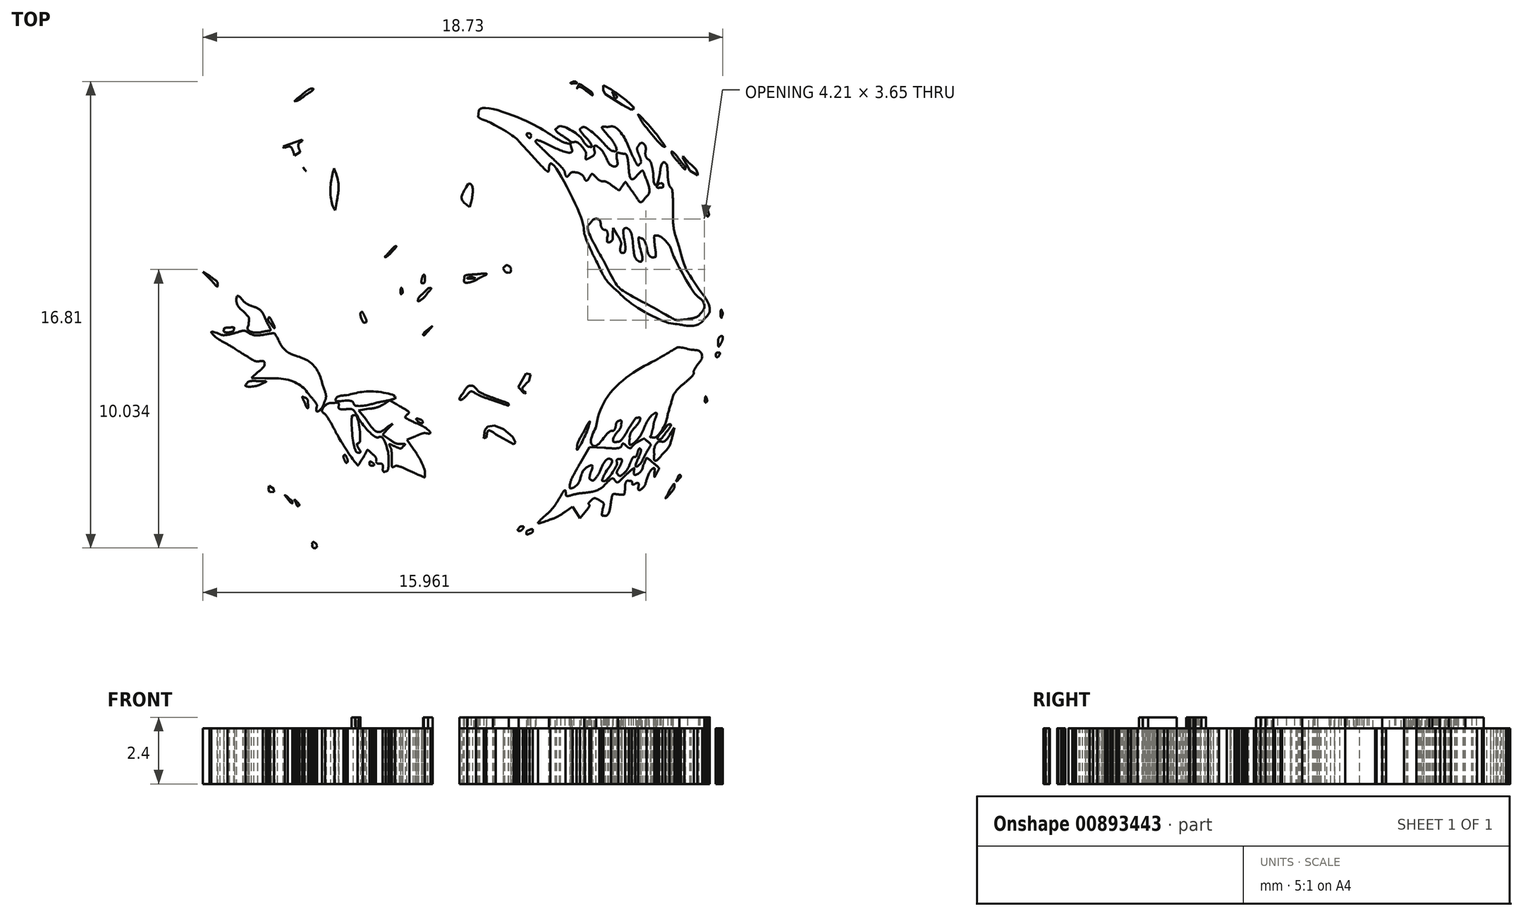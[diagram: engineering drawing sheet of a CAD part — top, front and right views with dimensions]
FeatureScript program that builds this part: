
annotation { "Feature Type Name" : "Feature", "Feature Type Description" : "" }
export const myFeature = defineFeature(function(context is Context, id is Id, definition is map)
    precondition{}
    {
        {
            var Q0;
            Q0=qCreatedBy(makeId("Top.planeOp"),FACE);
            var sketch = newSketch(context, id + "F0", { "sketchPlane" : qUnion([Q0])});
            skLineSegment(sketch, "E0", {"start": v(-1.28, 3.28) * mm, "end": v(-1.3, 2.97) * mm});
            skLineSegment(sketch, "E1", {"start": v(-1.3, 2.97) * mm, "end": v(-1.11, 3.15) * mm});
            skLineSegment(sketch, "E2", {"start": v(2.18, 4.65) * mm, "end": v(2.37, 4.86) * mm});
            skLineSegment(sketch, "E3", {"start": v(2.37, 4.86) * mm, "end": v(2.16, 5.12) * mm});
            skLineSegment(sketch, "E4", {"start": v(-1.79, -9.77) * mm, "end": v(-1.79, -9.77) * mm});
            skLineSegment(sketch, "E5", {"start": v(1.22, -9.04) * mm, "end": v(1.22, -9.04) * mm});
            skLineSegment(sketch, "E6", {"start": v(3.68, -7.03) * mm, "end": v(3.93, -6.85) * mm});
            skLineSegment(sketch, "E7", {"start": v(3.93, -6.85) * mm, "end": v(4.07, -7.06) * mm});
            skLineSegment(sketch, "E8", {"start": v(4.07, -7.06) * mm, "end": v(4.2, -7.27) * mm});
            skLineSegment(sketch, "E9", {"start": v(4.2, -7.27) * mm, "end": v(4.38, -7.05) * mm});
            skLineSegment(sketch, "E10", {"start": v(3.14, -7.31) * mm, "end": v(3.14, -7.31) * mm});
            skLineSegment(sketch, "E11", {"start": v(5.08, -4.73) * mm, "end": v(4.54, -4.7) * mm});
            skLineSegment(sketch, "E12", {"start": v(4.54, -4.7) * mm, "end": v(4.2, -5.3) * mm});
            skLineSegment(sketch, "E13", {"start": v(4.23, -5.78) * mm, "end": v(4.23, -5.78) * mm});
            skLineSegment(sketch, "E14", {"start": v(7.55, -4.24) * mm, "end": v(7.6, -4) * mm});
            skLineSegment(sketch, "E15", {"start": v(7.6, -4) * mm, "end": v(7.44, -4.26) * mm});
            skLineSegment(sketch, "E16", {"start": v(5.1, -4.32) * mm, "end": v(5.1, -4.32) * mm});
            skLineSegment(sketch, "E17", {"start": v(8.71, -2.98) * mm, "end": v(8.71, -2.98) * mm});
            skLineSegment(sketch, "E18", {"start": v(5.55, 2.93) * mm, "end": v(5.4, 3.2) * mm});
            skLineSegment(sketch, "E19", {"start": v(5.4, 3.2) * mm, "end": v(5.38, 2.98) * mm});
            skLineSegment(sketch, "E20", {"start": v(5.49, 4.23) * mm, "end": v(5.43, 4.51) * mm});
            skLineSegment(sketch, "E21", {"start": v(5.43, 4.51) * mm, "end": v(5.28, 4.32) * mm});
            skLineSegment(sketch, "E22", {"start": v(6.76, 3.08) * mm, "end": v(6.76, 3.08) * mm});
            skLineSegment(sketch, "E23", {"start": v(6.57, 4.3) * mm, "end": v(6.57, 4.3) * mm});
            skLineSegment(sketch, "E24", {"start": v(-1.13, -3.95) * mm, "end": v(-0.95, -4.13) * mm});
            skLineSegment(sketch, "E25", {"start": v(-0.95, -4.13) * mm, "end": v(-1.18, -4.32) * mm});
            skLineSegment(sketch, "E26", {"start": v(-1.8, -4.77) * mm, "end": v(-2.03, -4.44) * mm});
            skLineSegment(sketch, "E27", {"start": v(-2.03, -4.44) * mm, "end": v(-1.74, -4.32) * mm});
            skLineSegment(sketch, "E28", {"start": v(-3.4, -3.32) * mm, "end": v(-3.77, -3.38) * mm});
            skLineSegment(sketch, "E29", {"start": v(-3.77, -3.38) * mm, "end": v(-3.51, -3.7) * mm});
            skLineSegment(sketch, "E30", {"start": v(-2.74, -3.99) * mm, "end": v(-2.54, -3.86) * mm});
            skLineSegment(sketch, "E31", {"start": v(-2.54, -3.86) * mm, "end": v(-2.73, -4.06) * mm});
            skLineSegment(sketch, "E32", {"start": v(-2.73, -4.06) * mm, "end": v(-2.91, -4.26) * mm});
            skLineSegment(sketch, "E33", {"start": v(-2.91, -4.26) * mm, "end": v(-2.67, -4.42) * mm});
            skLineSegment(sketch, "E34", {"start": v(2.78, -4.13) * mm, "end": v(2.78, -4.13) * mm});
            skLineSegment(sketch, "E35", {"start": v(-1.29, -0.48) * mm, "end": v(-1.11, -0.33) * mm});
            skLineSegment(sketch, "E36", {"start": v(-1.11, -0.33) * mm, "end": v(-1.27, -0.52) * mm});
            skLineSegment(sketch, "E37", {"start": v(-1.27, -0.52) * mm, "end": v(-1.43, -0.7) * mm});
            skLineSegment(sketch, "E38", {"start": v(-1.43, -0.7) * mm, "end": v(-1.2, -0.66) * mm});
            skLineSegment(sketch, "E39", {"start": v(-2.96, -2.15) * mm, "end": v(-3.3, -2.5) * mm});
            skLineSegment(sketch, "E40", {"start": v(-3.3, -2.5) * mm, "end": v(-3.09, -2.6) * mm});
            skLineSegment(sketch, "E41", {"start": v(0.24, -4.1) * mm, "end": v(0.56, -4.33) * mm});
            skLineSegment(sketch, "E42", {"start": v(0.56, -4.33) * mm, "end": v(0.58, -4.03) * mm});
            skLineSegment(sketch, "E43", {"start": v(0.68, -3.73) * mm, "end": v(0.68, -3.73) * mm});
            skLineSegment(sketch, "E44", {"start": v(-7.4, -2) * mm, "end": v(-7.63, -2.21) * mm});
            skLineSegment(sketch, "E45", {"start": v(-7.63, -2.21) * mm, "end": v(-7.15, -2.23) * mm});
            skLineSegment(sketch, "E46", {"start": v(-5.01, -3.08) * mm, "end": v(-5.01, -3.08) * mm});
            skLineSegment(sketch, "E47", {"start": v(-3.12, -3.1) * mm, "end": v(-3.12, -3.1) * mm});
            skLineSegment(sketch, "E48", {"start": v(-3.34, -0.16) * mm, "end": v(-3.21, -0.45) * mm});
            skLineSegment(sketch, "E49", {"start": v(-3.21, -0.45) * mm, "end": v(-2.8, -0.12) * mm});
            skLineSegment(sketch, "E50", {"start": v(-5.75, 5.35) * mm, "end": v(-5.91, 5.54) * mm});
            skLineSegment(sketch, "E51", {"start": v(-5.91, 5.54) * mm, "end": v(-5.92, 5.17) * mm});
            skLineSegment(sketch, "E52", {"start": v(-4.3, -2.09) * mm, "end": v(-4.3, -2.09) * mm});
            skLineSegment(sketch, "E53", {"start": v(-1.3, 0.85) * mm, "end": v(-1.3, 0.85) * mm});
            skLineSegment(sketch, "E54", {"start": v(-2.2, 0.98) * mm, "end": v(-2.2, 0.98) * mm});
            skLineSegment(sketch, "E55", {"start": v(-9.12, 1.44) * mm, "end": v(-9.38, 1.61) * mm});
            skLineSegment(sketch, "E56", {"start": v(-9.38, 1.61) * mm, "end": v(-9.14, 1.37) * mm});
            skLineSegment(sketch, "E57", {"start": v(-9.14, 1.37) * mm, "end": v(-9.12, 1.44) * mm});
            skLineSegment(sketch, "E58", {"start": v(-5.72, 7.96) * mm, "end": v(-5.72, 7.96) * mm});
            skLineSegment(sketch, "E59", {"start": v(4.65, 8.03) * mm, "end": v(4.65, 8.03) * mm});
            skFitSpline(sketch, "E60", {"points": [v(-1.79, -9.77) * mm, v(-2.46, -9.65) * mm, v(-3.04, -9.54) * mm, v(-3.06, -9.5) * mm]});
            skFitSpline(sketch, "E61", {"points": [v(-3.06, -9.5) * mm, v(-3.12, -9.42) * mm, v(-3.76, -9.2) * mm, v(-3.94, -9.2) * mm]});
            skFitSpline(sketch, "E62", {"points": [v(-3.94, -9.2) * mm, v(-4.1, -9.2) * mm, v(-4.77, -8.83) * mm, v(-5.48, -8.36) * mm]});
            skFitSpline(sketch, "E63", {"points": [v(-5.48, -8.36) * mm, v(-6.03, -8) * mm, v(-6.95, -7.1) * mm, v(-7.14, -6.73) * mm]});
            skFitSpline(sketch, "E64", {"points": [v(-7.14, -6.73) * mm, v(-7.2, -6.6) * mm, v(-7.41, -6.36) * mm, v(-7.59, -6.21) * mm]});
            skFitSpline(sketch, "E65", {"points": [v(-7.59, -6.21) * mm, v(-7.76, -6.06) * mm, v(-7.9, -5.9) * mm, v(-7.9, -5.84) * mm]});
            skFitSpline(sketch, "E66", {"points": [v(-7.9, -5.84) * mm, v(-7.9, -5.79) * mm, v(-8.01, -5.62) * mm, v(-8.15, -5.48) * mm]});
            skFitSpline(sketch, "E67", {"points": [v(-8.15, -5.48) * mm, v(-8.28, -5.33) * mm, v(-8.38, -5.18) * mm, v(-8.38, -5.13) * mm]});
            skFitSpline(sketch, "E68", {"points": [v(-8.38, -5.13) * mm, v(-8.38, -5) * mm, v(-8.18, -5.05) * mm, v(-8.03, -5.21) * mm]});
            skFitSpline(sketch, "E69", {"points": [v(-8.03, -5.21) * mm, v(-7.83, -5.43) * mm, v(-7.76, -5.35) * mm, v(-7.83, -4.96) * mm]});
            skFitSpline(sketch, "E70", {"points": [v(-7.83, -4.96) * mm, v(-7.9, -4.6) * mm, v(-7.81, -4.47) * mm, v(-7.58, -4.6) * mm]});
            skFitSpline(sketch, "E71", {"points": [v(-7.58, -4.6) * mm, v(-7.5, -4.63) * mm, v(-7.38, -4.67) * mm, v(-7.31, -4.67) * mm]});
            skFitSpline(sketch, "E72", {"points": [v(-7.31, -4.67) * mm, v(-7.08, -4.67) * mm, v(-6.44, -4.34) * mm, v(-6.26, -4.13) * mm]});
            skFitSpline(sketch, "E73", {"points": [v(-6.26, -4.13) * mm, v(-6.16, -4.02) * mm, v(-5.98, -3.83) * mm, v(-5.87, -3.72) * mm]});
            skFitSpline(sketch, "E74", {"points": [v(-5.87, -3.72) * mm, v(-5.68, -3.53) * mm, v(-5.67, -3.49) * mm, v(-5.75, -3.29) * mm]});
            skFitSpline(sketch, "E75", {"points": [v(-5.75, -3.29) * mm, v(-5.8, -3.16) * mm, v(-5.96, -2.95) * mm, v(-6.09, -2.8) * mm]});
            skFitSpline(sketch, "E76", {"points": [v(-6.09, -2.8) * mm, v(-6.3, -2.57) * mm, v(-6.38, -2.54) * mm, v(-6.74, -2.53) * mm]});
            skFitSpline(sketch, "E77", {"points": [v(-6.74, -2.53) * mm, v(-6.97, -2.52) * mm, v(-7.37, -2.55) * mm, v(-7.64, -2.58) * mm]});
            skFitSpline(sketch, "E78", {"points": [v(-7.64, -2.58) * mm, v(-8.03, -2.63) * mm, v(-8.14, -2.62) * mm, v(-8.22, -2.52) * mm]});
            skFitSpline(sketch, "E79", {"points": [v(-8.22, -2.52) * mm, v(-8.3, -2.42) * mm, v(-8.3, -2.37) * mm, v(-8.18, -2.23) * mm]});
            skFitSpline(sketch, "E80", {"points": [v(-8.18, -2.23) * mm, v(-8.1, -2.14) * mm, v(-7.92, -2.02) * mm, v(-7.8, -1.95) * mm]});
            skFitSpline(sketch, "E81", {"points": [v(-7.8, -1.95) * mm, v(-7.57, -1.84) * mm, v(-7.57, -1.83) * mm, v(-7.7, -1.73) * mm]});
            skFitSpline(sketch, "E82", {"points": [v(-7.7, -1.73) * mm, v(-7.8, -1.67) * mm, v(-7.9, -1.62) * mm, v(-7.97, -1.62) * mm]});
            skFitSpline(sketch, "E83", {"points": [v(-7.97, -1.62) * mm, v(-8.07, -1.62) * mm, v(-8.94, -1.1) * mm, v(-9.02, -1) * mm]});
            skFitSpline(sketch, "E84", {"points": [v(-9.02, -1) * mm, v(-9.04, -0.97) * mm, v(-9.2, -0.87) * mm, v(-9.35, -0.77) * mm]});
            skFitSpline(sketch, "E85", {"points": [v(-9.35, -0.77) * mm, v(-9.8, -0.5) * mm, v(-9.68, -0.39) * mm, v(-8.94, -0.32) * mm]});
            skFitSpline(sketch, "E86", {"points": [v(-8.94, -0.32) * mm, v(-8.1, -0.25) * mm, v(-8.06, -0.21) * mm, v(-8.29, 0.18) * mm]});
            skFitSpline(sketch, "E87", {"points": [v(-8.29, 0.18) * mm, v(-8.38, 0.35) * mm, v(-8.47, 0.53) * mm, v(-8.47, 0.59) * mm]});
            skFitSpline(sketch, "E88", {"points": [v(-8.47, 0.59) * mm, v(-8.47, 0.64) * mm, v(-8.57, 0.76) * mm, v(-8.68, 0.84) * mm]});
            skFitSpline(sketch, "E89", {"points": [v(-8.68, 0.84) * mm, v(-8.9, 1) * mm, v(-8.9, 1) * mm, v(-8.79, 0.84) * mm]});
            skFitSpline(sketch, "E90", {"points": [v(-8.79, 0.84) * mm, v(-8.72, 0.76) * mm, v(-8.9, 0.92) * mm, v(-9.16, 1.2) * mm]});
            skFitSpline(sketch, "E91", {"points": [v(-9.16, 1.2) * mm, v(-9.64, 1.69) * mm, v(-9.78, 1.98) * mm, v(-9.54, 1.98) * mm]});
            skFitSpline(sketch, "E92", {"points": [v(-9.54, 1.98) * mm, v(-9.48, 1.98) * mm, v(-9.4, 1.94) * mm, v(-9.38, 1.9) * mm]});
            skFitSpline(sketch, "E93", {"points": [v(-9.38, 1.9) * mm, v(-9.3, 1.77) * mm, v(-9, 1.8) * mm, v(-9.05, 1.93) * mm]});
            skFitSpline(sketch, "E94", {"points": [v(-9.05, 1.93) * mm, v(-9.16, 2.21) * mm, v(-9.26, 3.06) * mm, v(-9.2, 3.2) * mm]});
            skFitSpline(sketch, "E95", {"points": [v(-9.2, 3.2) * mm, v(-9.15, 3.34) * mm, v(-9.02, 3.26) * mm, v(-9.02, 3.08) * mm]});
            skFitSpline(sketch, "E96", {"points": [v(-9.02, 3.08) * mm, v(-9.02, 3) * mm, v(-8.89, 2.82) * mm, v(-8.72, 2.67) * mm]});
            skFitSpline(sketch, "E97", {"points": [v(-8.72, 2.67) * mm, v(-8.33, 2.3) * mm, v(-8, 2.3) * mm, v(-7.67, 2.68) * mm]});
            skFitSpline(sketch, "E98", {"points": [v(-7.67, 2.68) * mm, v(-7.55, 2.82) * mm, v(-7.42, 2.92) * mm, v(-7.38, 2.9) * mm]});
            skFitSpline(sketch, "E99", {"points": [v(-7.38, 2.9) * mm, v(-7.33, 2.87) * mm, v(-7.3, 2.62) * mm, v(-7.29, 2.34) * mm]});
            skFitSpline(sketch, "E100", {"points": [v(-7.29, 2.34) * mm, v(-7.28, 2.06) * mm, v(-7.24, 1.75) * mm, v(-7.2, 1.64) * mm]});
            skFitSpline(sketch, "E101", {"points": [v(-7.2, 1.64) * mm, v(-7.12, 1.44) * mm, v(-6.66, 1.07) * mm, v(-6.58, 1.15) * mm]});
            skFitSpline(sketch, "E102", {"points": [v(-6.58, 1.15) * mm, v(-6.56, 1.17) * mm, v(-6.57, 1.4) * mm, v(-6.62, 1.64) * mm]});
            skFitSpline(sketch, "E103", {"points": [v(-6.62, 1.64) * mm, v(-6.67, 1.9) * mm, v(-6.72, 2.31) * mm, v(-6.73, 2.58) * mm]});
            skFitSpline(sketch, "E104", {"points": [v(-6.73, 2.58) * mm, v(-6.74, 2.9) * mm, v(-6.78, 3.04) * mm, v(-6.85, 3.02) * mm]});
            skFitSpline(sketch, "E105", {"points": [v(-6.85, 3.02) * mm, v(-6.9, 3) * mm, v(-6.96, 3.07) * mm, v(-7, 3.17) * mm]});
            skFitSpline(sketch, "E106", {"points": [v(-7, 3.17) * mm, v(-7.03, 3.27) * mm, v(-7.12, 3.42) * mm, v(-7.21, 3.52) * mm]});
            skFitSpline(sketch, "E107", {"points": [v(-7.21, 3.52) * mm, v(-7.3, 3.62) * mm, v(-7.35, 3.74) * mm, v(-7.32, 3.82) * mm]});
            skFitSpline(sketch, "E108", {"points": [v(-7.32, 3.82) * mm, v(-7.27, 3.95) * mm, v(-7.25, 3.94) * mm, v(-7.1, 3.8) * mm]});
            skFitSpline(sketch, "E109", {"points": [v(-7.1, 3.8) * mm, v(-6.67, 3.43) * mm, v(-6.63, 3.54) * mm, v(-6.96, 4.14) * mm]});
            skFitSpline(sketch, "E110", {"points": [v(-6.96, 4.14) * mm, v(-7.14, 4.47) * mm, v(-7.26, 4.75) * mm, v(-7.24, 4.77) * mm]});
            skFitSpline(sketch, "E111", {"points": [v(-7.24, 4.77) * mm, v(-7.22, 4.79) * mm, v(-7.13, 4.77) * mm, v(-7.05, 4.72) * mm]});
            skFitSpline(sketch, "E112", {"points": [v(-7.05, 4.72) * mm, v(-6.8, 4.6) * mm, v(-6.41, 4.62) * mm, v(-6.25, 4.78) * mm]});
            skFitSpline(sketch, "E113", {"points": [v(-6.25, 4.78) * mm, v(-6.07, 4.96) * mm, v(-5.97, 5.5) * mm, v(-6.08, 5.77) * mm]});
            skFitSpline(sketch, "E114", {"points": [v(-6.08, 5.77) * mm, v(-6.12, 5.89) * mm, v(-6.14, 6.01) * mm, v(-6.11, 6.05) * mm]});
            skFitSpline(sketch, "E115", {"points": [v(-6.11, 6.05) * mm, v(-6.03, 6.19) * mm, v(-5.92, 6.12) * mm, v(-5.87, 5.9) * mm]});
            skFitSpline(sketch, "E116", {"points": [v(-5.87, 5.9) * mm, v(-5.71, 5.28) * mm, v(-5.36, 5.17) * mm, v(-4.97, 5.63) * mm]});
            skFitSpline(sketch, "E117", {"points": [v(-4.97, 5.63) * mm, v(-4.74, 5.9) * mm, v(-4.73, 5.91) * mm, v(-4.73, 5.74) * mm]});
            skFitSpline(sketch, "E118", {"points": [v(-4.73, 5.74) * mm, v(-4.73, 5.63) * mm, v(-4.68, 5.43) * mm, v(-4.63, 5.28) * mm]});
            skFitSpline(sketch, "E119", {"points": [v(-4.63, 5.28) * mm, v(-4.55, 5.07) * mm, v(-4.55, 5) * mm, v(-4.64, 4.96) * mm]});
            skFitSpline(sketch, "E120", {"points": [v(-4.64, 4.96) * mm, v(-4.72, 4.9) * mm, v(-4.71, 4.88) * mm, v(-4.62, 4.85) * mm]});
            skFitSpline(sketch, "E121", {"points": [v(-4.62, 4.85) * mm, v(-4.55, 4.82) * mm, v(-4.49, 4.74) * mm, v(-4.49, 4.67) * mm]});
            skFitSpline(sketch, "E122", {"points": [v(-4.49, 4.67) * mm, v(-4.49, 4.6) * mm, v(-4.53, 4.57) * mm, v(-4.57, 4.6) * mm]});
            skFitSpline(sketch, "E123", {"points": [v(-4.57, 4.6) * mm, v(-4.61, 4.63) * mm, v(-4.63, 4.68) * mm, v(-4.6, 4.72) * mm]});
            skFitSpline(sketch, "E124", {"points": [v(-4.6, 4.72) * mm, v(-4.58, 4.76) * mm, v(-4.6, 4.8) * mm, v(-4.64, 4.8) * mm]});
            skFitSpline(sketch, "E125", {"points": [v(-4.64, 4.8) * mm, v(-4.7, 4.8) * mm, v(-4.72, 4.61) * mm, v(-4.72, 4.34) * mm]});
            skFitSpline(sketch, "E126", {"points": [v(-4.72, 4.34) * mm, v(-4.71, 3.98) * mm, v(-4.7, 3.93) * mm, v(-4.64, 4.09) * mm]});
            skFitSpline(sketch, "E127", {"points": [v(-4.64, 4.09) * mm, v(-4.59, 4.24) * mm, v(-4.58, 4.2) * mm, v(-4.6, 3.91) * mm]});
            skFitSpline(sketch, "E128", {"points": [v(-4.6, 3.91) * mm, v(-4.65, 3.5) * mm, v(-4.57, 3.44) * mm, v(-4.28, 3.7) * mm]});
            skFitSpline(sketch, "E129", {"points": [v(-4.28, 3.7) * mm, v(-4.06, 3.91) * mm, v(-3.97, 3.86) * mm, v(-3.9, 3.48) * mm]});
            skFitSpline(sketch, "E130", {"points": [v(-3.9, 3.48) * mm, v(-3.85, 3.12) * mm, v(-3.54, 2.41) * mm, v(-3.48, 2.48) * mm]});
            skFitSpline(sketch, "E131", {"points": [v(-3.48, 2.48) * mm, v(-3.45, 2.5) * mm, v(-3.34, 2.47) * mm, v(-3.24, 2.4) * mm]});
            skFitSpline(sketch, "E132", {"points": [v(-3.24, 2.4) * mm, v(-3.05, 2.28) * mm, v(-3.03, 2.29) * mm, v(-2.81, 2.5) * mm]});
            skFitSpline(sketch, "E133", {"points": [v(-2.81, 2.5) * mm, v(-2.69, 2.61) * mm, v(-2.58, 2.68) * mm, v(-2.58, 2.64) * mm]});
            skFitSpline(sketch, "E134", {"points": [v(-2.58, 2.64) * mm, v(-2.58, 2.53) * mm, v(-1.82, 3.37) * mm, v(-1.46, 3.9) * mm]});
            skFitSpline(sketch, "E135", {"points": [v(-1.46, 3.9) * mm, v(-1.27, 4.17) * mm, v(-1.07, 4.4) * mm, v(-1.01, 4.4) * mm]});
            skFitSpline(sketch, "E136", {"points": [v(-1.01, 4.4) * mm, v(-0.88, 4.4) * mm, v(-0.88, 4.4) * mm, v(-1.08, 3.96) * mm]});
            skFitSpline(sketch, "E137", {"points": [v(-1.08, 3.96) * mm, v(-1.17, 3.75) * mm, v(-1.26, 3.44) * mm, v(-1.28, 3.28) * mm]});
            skFitSpline(sketch, "E138", {"points": [v(-1.11, 3.15) * mm, v(-1, 3.25) * mm, v(-0.94, 3.36) * mm, v(-0.96, 3.38) * mm]});
            skFitSpline(sketch, "E139", {"points": [v(-0.96, 3.38) * mm, v(-1, 3.4) * mm, v(-1.03, 3.38) * mm, v(-1.05, 3.33) * mm]});
            skFitSpline(sketch, "E140", {"points": [v(-1.05, 3.33) * mm, v(-1.07, 3.27) * mm, v(-1.12, 3.23) * mm, v(-1.17, 3.23) * mm]});
            skFitSpline(sketch, "E141", {"points": [v(-1.17, 3.23) * mm, v(-1.22, 3.23) * mm, v(-1.02, 3.46) * mm, v(-0.73, 3.75) * mm]});
            skFitSpline(sketch, "E142", {"points": [v(-0.73, 3.75) * mm, v(-0.44, 4.03) * mm, v(-0.15, 4.39) * mm, v(-0.08, 4.53) * mm]});
            skFitSpline(sketch, "E143", {"points": [v(-0.08, 4.53) * mm, v(0, 4.68) * mm, v(0.1, 4.8) * mm, v(0.18, 4.8) * mm]});
            skFitSpline(sketch, "E144", {"points": [v(0.18, 4.8) * mm, v(0.27, 4.8) * mm, v(0.29, 4.77) * mm, v(0.23, 4.73) * mm]});
            skFitSpline(sketch, "E145", {"points": [v(0.23, 4.73) * mm, v(0.13, 4.67) * mm, v(-0.04, 4.37) * mm, v(-0.04, 4.27) * mm]});
            skFitSpline(sketch, "E146", {"points": [v(-0.04, 4.27) * mm, v(-0.03, 4.24) * mm, v(0.02, 4.28) * mm, v(0.08, 4.36) * mm]});
            skFitSpline(sketch, "E147", {"points": [v(0.08, 4.36) * mm, v(0.29, 4.62) * mm, v(0.38, 4.4) * mm, v(0.24, 3.97) * mm]});
            skFitSpline(sketch, "E148", {"points": [v(0.24, 3.97) * mm, v(0.07, 3.42) * mm, v(0.09, 3.24) * mm, v(0.31, 3.14) * mm]});
            skFitSpline(sketch, "E149", {"points": [v(0.31, 3.14) * mm, v(0.58, 3.02) * mm, v(0.92, 3.24) * mm, v(1.48, 3.87) * mm]});
            skFitSpline(sketch, "E150", {"points": [v(1.48, 3.87) * mm, v(1.71, 4.14) * mm, v(1.92, 4.38) * mm, v(1.95, 4.4) * mm]});
            skFitSpline(sketch, "E151", {"points": [v(1.95, 4.4) * mm, v(1.97, 4.43) * mm, v(2.07, 4.54) * mm, v(2.18, 4.65) * mm]});
            skFitSpline(sketch, "E152", {"points": [v(2.16, 5.12) * mm, v(1.77, 5.6) * mm, v(1.1, 6.12) * mm, v(0.88, 6.12) * mm]});
            skFitSpline(sketch, "E153", {"points": [v(0.88, 6.12) * mm, v(0.8, 6.12) * mm, v(0.65, 6.2) * mm, v(0.56, 6.28) * mm]});
            skFitSpline(sketch, "E154", {"points": [v(0.56, 6.28) * mm, v(0.38, 6.44) * mm, v(-0.36, 6.67) * mm, v(-1.39, 6.87) * mm]});
            skFitSpline(sketch, "E155", {"points": [v(-1.39, 6.87) * mm, v(-1.94, 6.98) * mm, v(-2.9, 6.98) * mm, v(-4.25, 6.87) * mm]});
            skFitSpline(sketch, "E156", {"points": [v(-4.25, 6.87) * mm, v(-4.64, 6.84) * mm, v(-5.54, 6.53) * mm, v(-5.7, 6.37) * mm]});
            skFitSpline(sketch, "E157", {"points": [v(-5.7, 6.37) * mm, v(-5.75, 6.32) * mm, v(-5.85, 6.28) * mm, v(-5.92, 6.28) * mm]});
            skFitSpline(sketch, "E158", {"points": [v(-5.92, 6.28) * mm, v(-5.99, 6.28) * mm, v(-6.18, 6.2) * mm, v(-6.34, 6.12) * mm]});
            skFitSpline(sketch, "E159", {"points": [v(-6.34, 6.12) * mm, v(-6.5, 6.04) * mm, v(-6.64, 5.98) * mm, v(-6.64, 6) * mm]});
            skFitSpline(sketch, "E160", {"points": [v(-6.64, 6) * mm, v(-6.64, 6.02) * mm, v(-6.91, 5.88) * mm, v(-7.25, 5.68) * mm]});
            skFitSpline(sketch, "E161", {"points": [v(-7.25, 5.68) * mm, v(-7.6, 5.48) * mm, v(-7.91, 5.32) * mm, v(-7.96, 5.3) * mm]});
            skFitSpline(sketch, "E162", {"points": [v(-7.96, 5.3) * mm, v(-8.02, 5.3) * mm, v(-8.13, 5.23) * mm, v(-8.22, 5.15) * mm]});
            skFitSpline(sketch, "E163", {"points": [v(-8.22, 5.15) * mm, v(-8.4, 5) * mm, v(-8.62, 5.03) * mm, v(-8.62, 5.21) * mm]});
            skFitSpline(sketch, "E164", {"points": [v(-8.62, 5.21) * mm, v(-8.62, 5.27) * mm, v(-8.57, 5.34) * mm, v(-8.5, 5.37) * mm]});
            skFitSpline(sketch, "E165", {"points": [v(-8.5, 5.37) * mm, v(-8.44, 5.4) * mm, v(-8.34, 5.51) * mm, v(-8.29, 5.63) * mm]});
            skFitSpline(sketch, "E166", {"points": [v(-8.29, 5.63) * mm, v(-8.15, 5.94) * mm, v(-6.9, 7.35) * mm, v(-6.34, 7.82) * mm]});
            skFitSpline(sketch, "E167", {"points": [v(-6.34, 7.82) * mm, v(-6.09, 8.03) * mm, v(-5.6, 8.34) * mm, v(-5.24, 8.5) * mm]});
            skFitSpline(sketch, "E168", {"points": [v(-5.24, 8.5) * mm, v(-4.9, 8.66) * mm, v(-4.43, 8.88) * mm, v(-4.21, 8.98) * mm]});
            skFitSpline(sketch, "E169", {"points": [v(-4.21, 8.98) * mm, v(-4, 9.08) * mm, v(-3.52, 9.25) * mm, v(-3.16, 9.37) * mm]});
            skFitSpline(sketch, "E170", {"points": [v(-3.16, 9.37) * mm, v(-2.8, 9.48) * mm, v(-2.49, 9.6) * mm, v(-2.46, 9.64) * mm]});
            skFitSpline(sketch, "E171", {"points": [v(-2.46, 9.64) * mm, v(-2.44, 9.68) * mm, v(-2.22, 9.73) * mm, v(-1.96, 9.76) * mm]});
            skFitSpline(sketch, "E172", {"points": [v(-1.96, 9.76) * mm, v(-1.71, 9.78) * mm, v(-1.24, 9.84) * mm, v(-0.91, 9.88) * mm]});
            skFitSpline(sketch, "E173", {"points": [v(-0.91, 9.88) * mm, v(0, 10) * mm, v(0.94, 10.01) * mm, v(1.04, 9.9) * mm]});
            skFitSpline(sketch, "E174", {"points": [v(1.04, 9.9) * mm, v(1.08, 9.85) * mm, v(1.33, 9.78) * mm, v(1.6, 9.76) * mm]});
            skFitSpline(sketch, "E175", {"points": [v(1.6, 9.76) * mm, v(2.12, 9.71) * mm, v(4.13, 8.98) * mm, v(4.42, 8.73) * mm]});
            skFitSpline(sketch, "E176", {"points": [v(4.42, 8.73) * mm, v(4.49, 8.67) * mm, v(4.59, 8.62) * mm, v(4.64, 8.62) * mm]});
            skFitSpline(sketch, "E177", {"points": [v(4.64, 8.62) * mm, v(4.69, 8.62) * mm, v(4.73, 8.6) * mm, v(4.73, 8.56) * mm]});
            skFitSpline(sketch, "E178", {"points": [v(4.73, 8.56) * mm, v(4.73, 8.53) * mm, v(4.86, 8.44) * mm, v(5.01, 8.36) * mm]});
            skFitSpline(sketch, "E179", {"points": [v(5.01, 8.36) * mm, v(5.19, 8.28) * mm, v(5.27, 8.2) * mm, v(5.24, 8.14) * mm]});
            skFitSpline(sketch, "E180", {"points": [v(5.24, 8.14) * mm, v(5.2, 8.09) * mm, v(5.22, 8.07) * mm, v(5.27, 8.1) * mm]});
            skFitSpline(sketch, "E181", {"points": [v(5.27, 8.1) * mm, v(5.38, 8.17) * mm, v(5.69, 8) * mm, v(5.69, 7.87) * mm]});
            skFitSpline(sketch, "E182", {"points": [v(5.69, 7.87) * mm, v(5.69, 7.77) * mm, v(5.91, 7.61) * mm, v(6.02, 7.64) * mm]});
            skFitSpline(sketch, "E183", {"points": [v(6.02, 7.64) * mm, v(6.1, 7.65) * mm, v(7.27, 6.53) * mm, v(7.8, 5.94) * mm]});
            skFitSpline(sketch, "E184", {"points": [v(7.8, 5.94) * mm, v(8.01, 5.7) * mm, v(8.18, 5.45) * mm, v(8.16, 5.4) * mm]});
            skFitSpline(sketch, "E185", {"points": [v(8.16, 5.4) * mm, v(8.15, 5.34) * mm, v(8.16, 5.33) * mm, v(8.2, 5.36) * mm]});
            skFitSpline(sketch, "E186", {"points": [v(8.2, 5.36) * mm, v(8.28, 5.44) * mm, v(8.47, 5.27) * mm, v(8.47, 5.1) * mm]});
            skFitSpline(sketch, "E187", {"points": [v(8.47, 5.1) * mm, v(8.47, 5.03) * mm, v(8.54, 4.88) * mm, v(8.63, 4.77) * mm]});
            skFitSpline(sketch, "E188", {"points": [v(8.63, 4.77) * mm, v(8.72, 4.65) * mm, v(8.8, 4.48) * mm, v(8.82, 4.38) * mm]});
            skFitSpline(sketch, "E189", {"points": [v(8.82, 4.38) * mm, v(8.83, 4.29) * mm, v(8.9, 4.12) * mm, v(8.96, 4.01) * mm]});
            skFitSpline(sketch, "E190", {"points": [v(8.96, 4.01) * mm, v(9.18, 3.7) * mm, v(9.4, 2.78) * mm, v(9.59, 1.55) * mm]});
            skFitSpline(sketch, "E191", {"points": [v(9.59, 1.55) * mm, v(9.68, 0.9) * mm, v(9.68, -0.37) * mm, v(9.57, -1.58) * mm]});
            skFitSpline(sketch, "E192", {"points": [v(9.57, -1.58) * mm, v(9.54, -2.05) * mm, v(9.5, -2.53) * mm, v(9.5, -2.63) * mm]});
            skFitSpline(sketch, "E193", {"points": [v(9.5, -2.63) * mm, v(9.5, -2.82) * mm, v(9.25, -3.66) * mm, v(9.1, -4) * mm]});
            skFitSpline(sketch, "E194", {"points": [v(9.1, -4) * mm, v(8.92, -4.36) * mm, v(8.65, -4.74) * mm, v(8.6, -4.69) * mm]});
            skFitSpline(sketch, "E195", {"points": [v(8.6, -4.69) * mm, v(8.56, -4.66) * mm, v(8.56, -4.69) * mm, v(8.59, -4.76) * mm]});
            skFitSpline(sketch, "E196", {"points": [v(8.59, -4.76) * mm, v(8.64, -4.88) * mm, v(8.1, -5.78) * mm, v(7.74, -6.2) * mm]});
            skFitSpline(sketch, "E197", {"points": [v(7.74, -6.2) * mm, v(7.64, -6.3) * mm, v(7.5, -6.5) * mm, v(7.43, -6.62) * mm]});
            skFitSpline(sketch, "E198", {"points": [v(7.43, -6.62) * mm, v(7.27, -6.9) * mm, v(6.45, -7.6) * mm, v(6.08, -7.76) * mm]});
            skFitSpline(sketch, "E199", {"points": [v(6.08, -7.76) * mm, v(5.93, -7.83) * mm, v(5.38, -8.1) * mm, v(4.85, -8.35) * mm]});
            skFitSpline(sketch, "E200", {"points": [v(4.85, -8.35) * mm, v(3.87, -8.82) * mm, v(2.98, -9.14) * mm, v(1.64, -9.48) * mm]});
            skFitSpline(sketch, "E201", {"points": [v(1.64, -9.48) * mm, v(0.95, -9.66) * mm, v(-0.54, -10) * mm, v(-0.55, -9.98) * mm]});
            skFitSpline(sketch, "E202", {"points": [v(-0.55, -9.98) * mm, v(-0.55, -9.97) * mm, v(-1.1, -9.88) * mm, v(-1.79, -9.77) * mm]});
            skFitSpline(sketch, "E203", {"points": [v(1.22, -9.04) * mm, v(2.37, -8.92) * mm, v(4.6, -8.1) * mm, v(5.55, -7.44) * mm]});
            skFitSpline(sketch, "E204", {"points": [v(5.55, -7.44) * mm, v(5.75, -7.3) * mm, v(5.88, -7.29) * mm, v(5.8, -7.41) * mm]});
            skFitSpline(sketch, "E205", {"points": [v(5.8, -7.41) * mm, v(5.76, -7.47) * mm, v(5.8, -7.47) * mm, v(5.9, -7.41) * mm]});
            skFitSpline(sketch, "E206", {"points": [v(5.9, -7.41) * mm, v(6, -7.36) * mm, v(6.1, -7.28) * mm, v(6.13, -7.23) * mm]});
            skFitSpline(sketch, "E207", {"points": [v(6.13, -7.23) * mm, v(6.17, -7.16) * mm, v(6.15, -7.17) * mm, v(6.06, -7.24) * mm]});
            skFitSpline(sketch, "E208", {"points": [v(6.06, -7.24) * mm, v(5.98, -7.3) * mm, v(5.9, -7.33) * mm, v(5.88, -7.3) * mm]});
            skFitSpline(sketch, "E209", {"points": [v(5.88, -7.3) * mm, v(5.85, -7.28) * mm, v(5.95, -7.19) * mm, v(6.1, -7.09) * mm]});
            skFitSpline(sketch, "E210", {"points": [v(6.1, -7.09) * mm, v(6.43, -6.87) * mm, v(7.43, -5.86) * mm, v(7.43, -5.75) * mm]});
            skFitSpline(sketch, "E211", {"points": [v(7.43, -5.75) * mm, v(7.43, -5.7) * mm, v(7.54, -5.54) * mm, v(7.67, -5.38) * mm]});
            skFitSpline(sketch, "E212", {"points": [v(7.67, -5.38) * mm, v(7.8, -5.22) * mm, v(7.94, -5) * mm, v(8, -4.88) * mm]});
            skFitSpline(sketch, "E213", {"points": [v(8, -4.88) * mm, v(8.05, -4.77) * mm, v(8.11, -4.69) * mm, v(8.14, -4.7) * mm]});
            skFitSpline(sketch, "E214", {"points": [v(8.14, -4.7) * mm, v(8.17, -4.72) * mm, v(8.2, -4.65) * mm, v(8.2, -4.54) * mm]});
            skFitSpline(sketch, "E215", {"points": [v(8.2, -4.54) * mm, v(8.2, -4.44) * mm, v(8.29, -4.22) * mm, v(8.37, -4.05) * mm]});
            skFitSpline(sketch, "E216", {"points": [v(8.37, -4.05) * mm, v(8.46, -3.88) * mm, v(8.56, -3.6) * mm, v(8.6, -3.44) * mm]});
            skFitSpline(sketch, "E217", {"points": [v(8.6, -3.44) * mm, v(8.64, -3.2) * mm, v(8.66, -3.17) * mm, v(8.71, -3.3) * mm]});
            skFitSpline(sketch, "E218", {"points": [v(8.71, -3.3) * mm, v(8.77, -3.45) * mm, v(8.77, -3.45) * mm, v(8.8, -3.3) * mm]});
            skFitSpline(sketch, "E219", {"points": [v(8.8, -3.3) * mm, v(8.8, -3.21) * mm, v(8.82, -2.98) * mm, v(8.83, -2.8) * mm]});
            skFitSpline(sketch, "E220", {"points": [v(8.83, -2.8) * mm, v(8.84, -2.6) * mm, v(8.87, -2.26) * mm, v(8.9, -2.05) * mm]});
            skFitSpline(sketch, "E221", {"points": [v(8.9, -2.05) * mm, v(9.06, -0.75) * mm, v(9.1, -0.01) * mm, v(9.06, 0.61) * mm]});
            skFitSpline(sketch, "E222", {"points": [v(9.06, 0.61) * mm, v(8.99, 1.6) * mm, v(8.98, 1.62) * mm, v(8.91, 1.73) * mm]});
            skFitSpline(sketch, "E223", {"points": [v(8.91, 1.73) * mm, v(8.88, 1.79) * mm, v(8.83, 2.02) * mm, v(8.81, 2.24) * mm]});
            skFitSpline(sketch, "E224", {"points": [v(8.81, 2.24) * mm, v(8.77, 2.79) * mm, v(8.74, 2.92) * mm, v(8.64, 3.18) * mm]});
            skFitSpline(sketch, "E225", {"points": [v(8.64, 3.18) * mm, v(8.59, 3.3) * mm, v(8.55, 3.44) * mm, v(8.55, 3.49) * mm]});
            skFitSpline(sketch, "E226", {"points": [v(8.55, 3.49) * mm, v(8.55, 3.66) * mm, v(7.9, 4.9) * mm, v(7.6, 5.3) * mm]});
            skFitSpline(sketch, "E227", {"points": [v(7.6, 5.3) * mm, v(6.66, 6.54) * mm, v(5.67, 7.31) * mm, v(3.58, 8.42) * mm]});
            skFitSpline(sketch, "E228", {"points": [v(3.58, 8.42) * mm, v(2.99, 8.74) * mm, v(2.53, 9.02) * mm, v(2.57, 9.06) * mm]});
            skFitSpline(sketch, "E229", {"points": [v(2.57, 9.06) * mm, v(2.6, 9.1) * mm, v(2.58, 9.1) * mm, v(2.53, 9.06) * mm]});
            skFitSpline(sketch, "E230", {"points": [v(2.53, 9.06) * mm, v(2.47, 9.03) * mm, v(2.38, 9.03) * mm, v(2.33, 9.06) * mm]});
            skFitSpline(sketch, "E231", {"points": [v(2.33, 9.06) * mm, v(2.28, 9.1) * mm, v(2.13, 9.13) * mm, v(2, 9.15) * mm]});
            skFitSpline(sketch, "E232", {"points": [v(2, 9.15) * mm, v(1.87, 9.16) * mm, v(1.72, 9.2) * mm, v(1.67, 9.25) * mm]});
            skFitSpline(sketch, "E233", {"points": [v(1.67, 9.25) * mm, v(1.62, 9.3) * mm, v(1.55, 9.3) * mm, v(1.52, 9.27) * mm]});
            skFitSpline(sketch, "E234", {"points": [v(1.52, 9.27) * mm, v(1.49, 9.24) * mm, v(1.44, 9.26) * mm, v(1.4, 9.31) * mm]});
            skFitSpline(sketch, "E235", {"points": [v(1.4, 9.31) * mm, v(1.36, 9.38) * mm, v(1, 9.4) * mm, v(0.04, 9.4) * mm]});
            skFitSpline(sketch, "E236", {"points": [v(0.04, 9.4) * mm, v(-0.68, 9.4) * mm, v(-1.42, 9.4) * mm, v(-1.61, 9.4) * mm]});
            skFitSpline(sketch, "E237", {"points": [v(-1.61, 9.4) * mm, v(-2.08, 9.41) * mm, v(-2.8, 9.21) * mm, v(-2.95, 9.04) * mm]});
            skFitSpline(sketch, "E238", {"points": [v(-2.95, 9.04) * mm, v(-3.02, 8.96) * mm, v(-3.05, 8.94) * mm, v(-3.02, 9) * mm]});
            skFitSpline(sketch, "E239", {"points": [v(-3.02, 9) * mm, v(-3, 9.05) * mm, v(-3, 9.1) * mm, v(-3.05, 9.1) * mm]});
            skFitSpline(sketch, "E240", {"points": [v(-3.05, 9.1) * mm, v(-3.1, 9.1) * mm, v(-3.14, 9.06) * mm, v(-3.14, 9.02) * mm]});
            skFitSpline(sketch, "E241", {"points": [v(-3.14, 9.02) * mm, v(-3.14, 8.98) * mm, v(-3.25, 8.93) * mm, v(-3.4, 8.9) * mm]});
            skFitSpline(sketch, "E242", {"points": [v(-3.4, 8.9) * mm, v(-3.53, 8.86) * mm, v(-3.7, 8.81) * mm, v(-3.77, 8.78) * mm]});
            skFitSpline(sketch, "E243", {"points": [v(-3.77, 8.78) * mm, v(-3.84, 8.74) * mm, v(-4.09, 8.62) * mm, v(-4.33, 8.5) * mm]});
            skFitSpline(sketch, "E244", {"points": [v(-4.33, 8.5) * mm, v(-5.13, 8.12) * mm, v(-6.52, 7.15) * mm, v(-7.14, 6.54) * mm]});
            skFitSpline(sketch, "E245", {"points": [v(-7.14, 6.54) * mm, v(-7.47, 6.2) * mm, v(-7.75, 5.9) * mm, v(-7.75, 5.87) * mm]});
            skFitSpline(sketch, "E246", {"points": [v(-7.75, 5.87) * mm, v(-7.75, 5.8) * mm, v(-7.5, 5.9) * mm, v(-7.18, 6.13) * mm]});
            skFitSpline(sketch, "E247", {"points": [v(-7.18, 6.13) * mm, v(-7.06, 6.21) * mm, v(-6.92, 6.28) * mm, v(-6.86, 6.28) * mm]});
            skFitSpline(sketch, "E248", {"points": [v(-6.86, 6.28) * mm, v(-6.8, 6.28) * mm, v(-6.63, 6.39) * mm, v(-6.48, 6.52) * mm]});
            skFitSpline(sketch, "E249", {"points": [v(-6.48, 6.52) * mm, v(-6.33, 6.64) * mm, v(-6.15, 6.75) * mm, v(-6.08, 6.75) * mm]});
            skFitSpline(sketch, "E250", {"points": [v(-6.08, 6.75) * mm, v(-6.01, 6.75) * mm, v(-5.87, 6.8) * mm, v(-5.75, 6.85) * mm]});
            skFitSpline(sketch, "E251", {"points": [v(-5.75, 6.85) * mm, v(-5.47, 7) * mm, v(-4.8, 7.2) * mm, v(-4.09, 7.33) * mm]});
            skFitSpline(sketch, "E252", {"points": [v(-4.09, 7.33) * mm, v(-3.42, 7.47) * mm, v(-1.55, 7.43) * mm, v(-1.16, 7.28) * mm]});
            skFitSpline(sketch, "E253", {"points": [v(-1.16, 7.28) * mm, v(-0.84, 7.15) * mm, v(-0.43, 7.07) * mm, v(-0.48, 7.14) * mm]});
            skFitSpline(sketch, "E254", {"points": [v(-0.48, 7.14) * mm, v(-0.5, 7.18) * mm, v(-0.33, 7.13) * mm, v(-0.1, 7.05) * mm]});
            skFitSpline(sketch, "E255", {"points": [v(-0.1, 7.05) * mm, v(0.13, 6.96) * mm, v(0.48, 6.84) * mm, v(0.68, 6.77) * mm]});
            skFitSpline(sketch, "E256", {"points": [v(0.68, 6.77) * mm, v(1.41, 6.52) * mm, v(2.22, 5.84) * mm, v(2.7, 5.08) * mm]});
            skFitSpline(sketch, "E257", {"points": [v(2.7, 5.08) * mm, v(2.8, 4.94) * mm, v(2.96, 4.72) * mm, v(3.08, 4.6) * mm]});
            skFitSpline(sketch, "E258", {"points": [v(3.08, 4.6) * mm, v(3.2, 4.47) * mm, v(3.3, 4.33) * mm, v(3.3, 4.28) * mm]});
            skFitSpline(sketch, "E259", {"points": [v(3.3, 4.28) * mm, v(3.3, 4.23) * mm, v(3.39, 4.11) * mm, v(3.5, 4.01) * mm]});
            skFitSpline(sketch, "E260", {"points": [v(3.5, 4.01) * mm, v(3.6, 3.91) * mm, v(3.7, 3.77) * mm, v(3.7, 3.69) * mm]});
            skFitSpline(sketch, "E261", {"points": [v(3.7, 3.69) * mm, v(3.7, 3.61) * mm, v(3.74, 3.53) * mm, v(3.79, 3.5) * mm]});
            skFitSpline(sketch, "E262", {"points": [v(3.79, 3.5) * mm, v(4, 3.36) * mm, v(4.42, 2.28) * mm, v(4.5, 1.6) * mm]});
            skFitSpline(sketch, "E263", {"points": [v(4.5, 1.6) * mm, v(4.55, 1.23) * mm, v(4.63, 0.88) * mm, v(4.67, 0.83) * mm]});
            skFitSpline(sketch, "E264", {"points": [v(4.67, 0.83) * mm, v(4.73, 0.76) * mm, v(4.72, 0.73) * mm, v(4.66, 0.73) * mm]});
            skFitSpline(sketch, "E265", {"points": [v(4.66, 0.73) * mm, v(4.61, 0.73) * mm, v(4.58, 0.61) * mm, v(4.58, 0.47) * mm]});
            skFitSpline(sketch, "E266", {"points": [v(4.58, 0.47) * mm, v(4.59, 0.24) * mm, v(4.6, 0.23) * mm, v(4.65, 0.42) * mm]});
            skFitSpline(sketch, "E267", {"points": [v(4.65, 0.42) * mm, v(4.74, 0.74) * mm, v(4.82, -0.75) * mm, v(4.74, -1.19) * mm]});
            skFitSpline(sketch, "E268", {"points": [v(4.74, -1.19) * mm, v(4.7, -1.4) * mm, v(4.55, -1.83) * mm, v(4.42, -2.13) * mm]});
            skFitSpline(sketch, "E269", {"points": [v(4.42, -2.13) * mm, v(4.29, -2.43) * mm, v(4.18, -2.72) * mm, v(4.18, -2.77) * mm]});
            skFitSpline(sketch, "E270", {"points": [v(4.18, -2.77) * mm, v(4.17, -3.08) * mm, v(3.04, -4.6) * mm, v(2.3, -5.3) * mm]});
            skFitSpline(sketch, "E271", {"points": [v(2.3, -5.3) * mm, v(1.6, -5.96) * mm, v(1.37, -6.15) * mm, v(1.33, -6.15) * mm]});
            skFitSpline(sketch, "E272", {"points": [v(1.33, -6.15) * mm, v(1.26, -6.15) * mm, v(0.41, -6.72) * mm, v(0.35, -6.8) * mm]});
            skFitSpline(sketch, "E273", {"points": [v(0.35, -6.8) * mm, v(0.32, -6.84) * mm, v(0.13, -6.94) * mm, v(-0.09, -7.01) * mm]});
            skFitSpline(sketch, "E274", {"points": [v(-0.09, -7.01) * mm, v(-1.38, -7.47) * mm, v(-1.7, -7.56) * mm, v(-2.13, -7.6) * mm]});
            skFitSpline(sketch, "E275", {"points": [v(-2.13, -7.6) * mm, v(-2.3, -7.6) * mm, v(-2.44, -7.63) * mm, v(-2.46, -7.65) * mm]});
            skFitSpline(sketch, "E276", {"points": [v(-2.46, -7.65) * mm, v(-2.5, -7.68) * mm, v(-2.96, -7.66) * mm, v(-3.58, -7.61) * mm]});
            skFitSpline(sketch, "E277", {"points": [v(-3.58, -7.61) * mm, v(-3.7, -7.6) * mm, v(-3.91, -7.55) * mm, v(-4.04, -7.5) * mm]});
            skFitSpline(sketch, "E278", {"points": [v(-4.04, -7.5) * mm, v(-4.16, -7.45) * mm, v(-4.33, -7.4) * mm, v(-4.42, -7.4) * mm]});
            skFitSpline(sketch, "E279", {"points": [v(-4.42, -7.4) * mm, v(-4.64, -7.4) * mm, v(-6.06, -7.04) * mm, v(-6.47, -6.88) * mm]});
            skFitSpline(sketch, "E280", {"points": [v(-6.47, -6.88) * mm, v(-6.73, -6.78) * mm, v(-6.44, -7.02) * mm, v(-5.82, -7.42) * mm]});
            skFitSpline(sketch, "E281", {"points": [v(-5.82, -7.42) * mm, v(-4.91, -8.01) * mm, v(-3.4, -8.72) * mm, v(-2.76, -8.86) * mm]});
            skFitSpline(sketch, "E282", {"points": [v(-2.76, -8.86) * mm, v(-2, -9.02) * mm, v(-1.47, -9.11) * mm, v(-1.15, -9.14) * mm]});
            skFitSpline(sketch, "E283", {"points": [v(-1.15, -9.14) * mm, v(-0.77, -9.18) * mm, v(0.42, -9.13) * mm, v(1.22, -9.04) * mm]});
            skFitSpline(sketch, "E284", {"points": [v(0.57, -8.28) * mm, v(0.55, -8.24) * mm, v(0.66, -8.15) * mm, v(0.82, -8.08) * mm]});
            skFitSpline(sketch, "E285", {"points": [v(0.82, -8.08) * mm, v(1.23, -7.88) * mm, v(1.24, -7.88) * mm, v(1.84, -7.47) * mm]});
            skFitSpline(sketch, "E286", {"points": [v(1.84, -7.47) * mm, v(2.37, -7.11) * mm, v(2.75, -6.78) * mm, v(2.63, -6.78) * mm]});
            skFitSpline(sketch, "E287", {"points": [v(2.63, -6.78) * mm, v(2.6, -6.78) * mm, v(2.72, -6.6) * mm, v(2.92, -6.37) * mm]});
            skFitSpline(sketch, "E288", {"points": [v(2.92, -6.37) * mm, v(3.33, -5.88) * mm, v(3.56, -5.51) * mm, v(3.7, -5.1) * mm]});
            skFitSpline(sketch, "E289", {"points": [v(3.7, -5.1) * mm, v(3.76, -4.92) * mm, v(3.88, -4.6) * mm, v(3.98, -4.4) * mm]});
            skFitSpline(sketch, "E290", {"points": [v(3.98, -4.4) * mm, v(4.08, -4.18) * mm, v(4.2, -3.88) * mm, v(4.26, -3.73) * mm]});
            skFitSpline(sketch, "E291", {"points": [v(4.26, -3.73) * mm, v(4.38, -3.42) * mm, v(4.45, -3.32) * mm, v(4.73, -3.08) * mm]});
            skFitSpline(sketch, "E292", {"points": [v(4.73, -3.08) * mm, v(4.93, -2.9) * mm, v(5.03, -2.8) * mm, v(5.57, -2.24) * mm]});
            skFitSpline(sketch, "E293", {"points": [v(5.57, -2.24) * mm, v(6.15, -1.63) * mm, v(7.46, -0.9) * mm, v(7.95, -0.9) * mm]});
            skFitSpline(sketch, "E294", {"points": [v(7.95, -0.9) * mm, v(8.76, -0.91) * mm, v(8.96, -1.77) * mm, v(8.3, -2.38) * mm]});
            skFitSpline(sketch, "E295", {"points": [v(8.3, -2.38) * mm, v(7.6, -3) * mm, v(7.65, -2.9) * mm, v(7.7, -3.56) * mm]});
            skFitSpline(sketch, "E296", {"points": [v(7.7, -3.56) * mm, v(7.74, -3.89) * mm, v(7.76, -4.3) * mm, v(7.76, -4.48) * mm]});
            skFitSpline(sketch, "E297", {"points": [v(7.76, -4.48) * mm, v(7.77, -4.8) * mm, v(7.59, -5.25) * mm, v(7.36, -5.45) * mm]});
            skFitSpline(sketch, "E298", {"points": [v(7.36, -5.45) * mm, v(7.28, -5.51) * mm, v(7.16, -5.68) * mm, v(7.07, -5.82) * mm]});
            skFitSpline(sketch, "E299", {"points": [v(7.07, -5.82) * mm, v(7, -5.96) * mm, v(6.9, -6.07) * mm, v(6.86, -6.07) * mm]});
            skFitSpline(sketch, "E300", {"points": [v(6.86, -6.07) * mm, v(6.75, -6.07) * mm, v(6.16, -6.65) * mm, v(6.16, -6.76) * mm]});
            skFitSpline(sketch, "E301", {"points": [v(6.16, -6.76) * mm, v(6.16, -6.81) * mm, v(6.13, -6.86) * mm, v(6.08, -6.86) * mm]});
            skFitSpline(sketch, "E302", {"points": [v(6.08, -6.86) * mm, v(6.04, -6.86) * mm, v(6, -6.82) * mm, v(6, -6.78) * mm]});
            skFitSpline(sketch, "E303", {"points": [v(6, -6.78) * mm, v(6, -6.74) * mm, v(5.97, -6.7) * mm, v(5.92, -6.7) * mm]});
            skFitSpline(sketch, "E304", {"points": [v(5.92, -6.7) * mm, v(5.88, -6.7) * mm, v(5.84, -6.75) * mm, v(5.84, -6.8) * mm]});
            skFitSpline(sketch, "E305", {"points": [v(5.84, -6.8) * mm, v(5.84, -6.86) * mm, v(5.77, -6.99) * mm, v(5.67, -7.08) * mm]});
            skFitSpline(sketch, "E306", {"points": [v(5.67, -7.08) * mm, v(5.54, -7.23) * mm, v(5.5, -7.24) * mm, v(5.43, -7.16) * mm]});
            skFitSpline(sketch, "E307", {"points": [v(5.43, -7.16) * mm, v(5.38, -7.08) * mm, v(5.37, -7.1) * mm, v(5.4, -7.22) * mm]});
            skFitSpline(sketch, "E308", {"points": [v(5.4, -7.22) * mm, v(5.43, -7.32) * mm, v(5.4, -7.42) * mm, v(5.33, -7.48) * mm]});
            skFitSpline(sketch, "E309", {"points": [v(5.33, -7.48) * mm, v(5.25, -7.54) * mm, v(5.2, -7.55) * mm, v(5.2, -7.5) * mm]});
            skFitSpline(sketch, "E310", {"points": [v(5.2, -7.5) * mm, v(5.2, -7.45) * mm, v(5.14, -7.42) * mm, v(5.05, -7.43) * mm]});
            skFitSpline(sketch, "E311", {"points": [v(5.05, -7.43) * mm, v(4.96, -7.43) * mm, v(4.9, -7.48) * mm, v(4.9, -7.53) * mm]});
            skFitSpline(sketch, "E312", {"points": [v(4.9, -7.53) * mm, v(4.9, -7.58) * mm, v(4.78, -7.7) * mm, v(4.65, -7.8) * mm]});
            skFitSpline(sketch, "E313", {"points": [v(4.65, -7.8) * mm, v(4.45, -7.94) * mm, v(4.4, -7.94) * mm, v(4.37, -7.85) * mm]});
            skFitSpline(sketch, "E314", {"points": [v(4.37, -7.85) * mm, v(4.34, -7.78) * mm, v(4.36, -7.66) * mm, v(4.4, -7.57) * mm]});
            skFitSpline(sketch, "E315", {"points": [v(4.4, -7.57) * mm, v(4.55, -7.31) * mm, v(4.5, -7.27) * mm, v(4.31, -7.5) * mm]});
            skFitSpline(sketch, "E316", {"points": [v(4.31, -7.5) * mm, v(4.21, -7.6) * mm, v(3.98, -7.74) * mm, v(3.8, -7.8) * mm]});
            skFitSpline(sketch, "E317", {"points": [v(3.8, -7.8) * mm, v(3.6, -7.86) * mm, v(3.42, -7.96) * mm, v(3.37, -8.04) * mm]});
            skFitSpline(sketch, "E318", {"points": [v(3.37, -8.04) * mm, v(3.28, -8.21) * mm, v(3.06, -8.23) * mm, v(3.06, -8.07) * mm]});
            skFitSpline(sketch, "E319", {"points": [v(3.06, -8.07) * mm, v(3.06, -8.01) * mm, v(3.16, -7.89) * mm, v(3.27, -7.8) * mm]});
            skFitSpline(sketch, "E320", {"points": [v(3.27, -7.8) * mm, v(3.63, -7.52) * mm, v(3.42, -7.54) * mm, v(2.89, -7.82) * mm]});
            skFitSpline(sketch, "E321", {"points": [v(2.89, -7.82) * mm, v(2.5, -8.03) * mm, v(2.19, -8.13) * mm, v(1.6, -8.22) * mm]});
            skFitSpline(sketch, "E322", {"points": [v(1.6, -8.22) * mm, v(0.73, -8.36) * mm, v(0.62, -8.37) * mm, v(0.57, -8.28) * mm]});
            skFitSpline(sketch, "E323", {"points": [v(2.5, -7.71) * mm, v(2.5, -7.67) * mm, v(2.45, -7.66) * mm, v(2.39, -7.69) * mm]});
            skFitSpline(sketch, "E324", {"points": [v(2.39, -7.69) * mm, v(2.32, -7.71) * mm, v(2.27, -7.76) * mm, v(2.27, -7.8) * mm]});
            skFitSpline(sketch, "E325", {"points": [v(2.27, -7.8) * mm, v(2.27, -7.84) * mm, v(2.32, -7.85) * mm, v(2.39, -7.82) * mm]});
            skFitSpline(sketch, "E326", {"points": [v(2.39, -7.82) * mm, v(2.45, -7.8) * mm, v(2.5, -7.75) * mm, v(2.5, -7.71) * mm]});
            skFitSpline(sketch, "E327", {"points": [v(2.15, -7.64) * mm, v(2.17, -7.6) * mm, v(2.16, -7.56) * mm, v(2.12, -7.56) * mm]});
            skFitSpline(sketch, "E328", {"points": [v(2.12, -7.56) * mm, v(2.07, -7.56) * mm, v(2.02, -7.6) * mm, v(1.99, -7.64) * mm]});
            skFitSpline(sketch, "E329", {"points": [v(1.99, -7.64) * mm, v(1.96, -7.68) * mm, v(1.98, -7.72) * mm, v(2.02, -7.72) * mm]});
            skFitSpline(sketch, "E330", {"points": [v(2.02, -7.72) * mm, v(2.06, -7.72) * mm, v(2.12, -7.68) * mm, v(2.15, -7.64) * mm]});
            skFitSpline(sketch, "E331", {"points": [v(3.14, -7.31) * mm, v(3.3, -7.26) * mm, v(3.53, -7.13) * mm, v(3.68, -7.03) * mm]});
            skFitSpline(sketch, "E332", {"points": [v(4.38, -7.05) * mm, v(4.48, -6.93) * mm, v(4.55, -6.8) * mm, v(4.53, -6.77) * mm]});
            skFitSpline(sketch, "E333", {"points": [v(4.53, -6.77) * mm, v(4.51, -6.74) * mm, v(4.55, -6.68) * mm, v(4.6, -6.63) * mm]});
            skFitSpline(sketch, "E334", {"points": [v(4.6, -6.63) * mm, v(4.7, -6.55) * mm, v(4.76, -6.55) * mm, v(4.9, -6.62) * mm]});
            skFitSpline(sketch, "E335", {"points": [v(4.9, -6.62) * mm, v(5.03, -6.7) * mm, v(5.06, -6.76) * mm, v(5.02, -6.94) * mm]});
            skFitSpline(sketch, "E336", {"points": [v(5.02, -6.94) * mm, v(5, -7.07) * mm, v(5, -7.17) * mm, v(5.04, -7.17) * mm]});
            skFitSpline(sketch, "E337", {"points": [v(5.04, -7.17) * mm, v(5.16, -7.17) * mm, v(5.27, -6.98) * mm, v(5.32, -6.68) * mm]});
            skFitSpline(sketch, "E338", {"points": [v(5.32, -6.68) * mm, v(5.37, -6.43) * mm, v(5.4, -6.4) * mm, v(5.59, -6.41) * mm]});
            skFitSpline(sketch, "E339", {"points": [v(5.59, -6.41) * mm, v(5.78, -6.42) * mm, v(5.8, -6.4) * mm, v(5.83, -6.17) * mm]});
            skFitSpline(sketch, "E340", {"points": [v(5.83, -6.17) * mm, v(5.84, -6.01) * mm, v(5.9, -5.92) * mm, v(5.97, -5.92) * mm]});
            skFitSpline(sketch, "E341", {"points": [v(5.97, -5.92) * mm, v(6.03, -5.92) * mm, v(6.08, -5.95) * mm, v(6.08, -6) * mm]});
            skFitSpline(sketch, "E342", {"points": [v(6.08, -6) * mm, v(6.08, -6.04) * mm, v(6.14, -6.05) * mm, v(6.2, -6.02) * mm]});
            skFitSpline(sketch, "E343", {"points": [v(6.2, -6.02) * mm, v(6.27, -6) * mm, v(6.32, -6.02) * mm, v(6.32, -6.07) * mm]});
            skFitSpline(sketch, "E344", {"points": [v(6.32, -6.07) * mm, v(6.32, -6.25) * mm, v(6.5, -6.14) * mm, v(6.6, -5.88) * mm]});
            skFitSpline(sketch, "E345", {"points": [v(6.6, -5.88) * mm, v(6.74, -5.57) * mm, v(6.88, -5.46) * mm, v(6.88, -5.66) * mm]});
            skFitSpline(sketch, "E346", {"points": [v(6.88, -5.66) * mm, v(6.89, -5.78) * mm, v(6.9, -5.77) * mm, v(6.97, -5.63) * mm]});
            skFitSpline(sketch, "E347", {"points": [v(6.97, -5.63) * mm, v(7.05, -5.48) * mm, v(7.03, -5.43) * mm, v(6.87, -5.3) * mm]});
            skFitSpline(sketch, "E348", {"points": [v(6.87, -5.3) * mm, v(6.62, -5.1) * mm, v(6.6, -5.1) * mm, v(6.48, -5.37) * mm]});
            skFitSpline(sketch, "E349", {"points": [v(6.48, -5.37) * mm, v(6.38, -5.6) * mm, v(6.16, -5.7) * mm, v(6.16, -5.51) * mm]});
            skFitSpline(sketch, "E350", {"points": [v(6.16, -5.51) * mm, v(6.16, -5.46) * mm, v(6.03, -5.55) * mm, v(5.86, -5.7) * mm]});
            skFitSpline(sketch, "E351", {"points": [v(5.86, -5.7) * mm, v(5.63, -5.93) * mm, v(5.54, -5.98) * mm, v(5.46, -5.9) * mm]});
            skFitSpline(sketch, "E352", {"points": [v(5.46, -5.9) * mm, v(5.39, -5.83) * mm, v(5.32, -5.85) * mm, v(5.15, -6.01) * mm]});
            skFitSpline(sketch, "E353", {"points": [v(5.15, -6.01) * mm, v(4.94, -6.2) * mm, v(4.66, -6.31) * mm, v(4.3, -6.36) * mm]});
            skFitSpline(sketch, "E354", {"points": [v(4.3, -6.36) * mm, v(4.2, -6.37) * mm, v(4.04, -6.4) * mm, v(3.92, -6.43) * mm]});
            skFitSpline(sketch, "E355", {"points": [v(3.92, -6.43) * mm, v(3.76, -6.47) * mm, v(3.7, -6.45) * mm, v(3.69, -6.35) * mm]});
            skFitSpline(sketch, "E356", {"points": [v(3.69, -6.35) * mm, v(3.67, -6.26) * mm, v(3.6, -6.31) * mm, v(3.46, -6.55) * mm]});
            skFitSpline(sketch, "E357", {"points": [v(3.46, -6.55) * mm, v(3.35, -6.73) * mm, v(3.14, -7) * mm, v(2.99, -7.14) * mm]});
            skFitSpline(sketch, "E358", {"points": [v(2.99, -7.14) * mm, v(2.69, -7.43) * mm, v(2.7, -7.45) * mm, v(3.14, -7.31) * mm]});
            skFitSpline(sketch, "E359", {"points": [v(4.23, -5.78) * mm, v(4.36, -5.51) * mm, v(4.64, -5.36) * mm, v(4.6, -5.59) * mm]});
            skFitSpline(sketch, "E360", {"points": [v(4.6, -5.59) * mm, v(4.58, -5.64) * mm, v(4.56, -5.72) * mm, v(4.55, -5.77) * mm]});
            skFitSpline(sketch, "E361", {"points": [v(4.55, -5.77) * mm, v(4.54, -5.82) * mm, v(4.57, -5.87) * mm, v(4.63, -5.9) * mm]});
            skFitSpline(sketch, "E362", {"points": [v(4.63, -5.9) * mm, v(4.68, -5.91) * mm, v(4.81, -5.77) * mm, v(4.93, -5.57) * mm]});
            skFitSpline(sketch, "E363", {"points": [v(4.93, -5.57) * mm, v(5.19, -5.14) * mm, v(5.35, -5.17) * mm, v(5.13, -5.6) * mm]});
            skFitSpline(sketch, "E364", {"points": [v(5.13, -5.6) * mm, v(5.04, -5.78) * mm, v(5, -5.92) * mm, v(5.04, -5.92) * mm]});
            skFitSpline(sketch, "E365", {"points": [v(5.04, -5.92) * mm, v(5.12, -5.92) * mm, v(5.53, -5.33) * mm, v(5.53, -5.22) * mm]});
            skFitSpline(sketch, "E366", {"points": [v(5.53, -5.22) * mm, v(5.53, -5.17) * mm, v(5.56, -5.14) * mm, v(5.6, -5.14) * mm]});
            skFitSpline(sketch, "E367", {"points": [v(5.6, -5.14) * mm, v(5.7, -5.14) * mm, v(5.7, -5.26) * mm, v(5.6, -5.46) * mm]});
            skFitSpline(sketch, "E368", {"points": [v(5.6, -5.46) * mm, v(5.55, -5.55) * mm, v(5.53, -5.64) * mm, v(5.55, -5.66) * mm]});
            skFitSpline(sketch, "E369", {"points": [v(5.55, -5.66) * mm, v(5.64, -5.74) * mm, v(5.9, -5.52) * mm, v(6, -5.3) * mm]});
            skFitSpline(sketch, "E370", {"points": [v(6, -5.3) * mm, v(6.06, -5.17) * mm, v(6.13, -5.06) * mm, v(6.17, -5.06) * mm]});
            skFitSpline(sketch, "E371", {"points": [v(6.17, -5.06) * mm, v(6.2, -5.06) * mm, v(6.25, -4.99) * mm, v(6.28, -4.9) * mm]});
            skFitSpline(sketch, "E372", {"points": [v(6.28, -4.9) * mm, v(6.31, -4.8) * mm, v(6.35, -4.75) * mm, v(6.38, -4.77) * mm]});
            skFitSpline(sketch, "E373", {"points": [v(6.38, -4.77) * mm, v(6.4, -4.8) * mm, v(6.38, -4.92) * mm, v(6.33, -5.05) * mm]});
            skFitSpline(sketch, "E374", {"points": [v(6.33, -5.05) * mm, v(6.21, -5.4) * mm, v(6.33, -5.35) * mm, v(6.56, -4.96) * mm]});
            skFitSpline(sketch, "E375", {"points": [v(6.56, -4.96) * mm, v(6.75, -4.65) * mm, v(6.76, -4.62) * mm, v(6.64, -4.5) * mm]});
            skFitSpline(sketch, "E376", {"points": [v(6.64, -4.5) * mm, v(6.52, -4.4) * mm, v(6.5, -4.4) * mm, v(6.32, -4.5) * mm]});
            skFitSpline(sketch, "E377", {"points": [v(6.32, -4.5) * mm, v(6.2, -4.57) * mm, v(6.1, -4.66) * mm, v(6.07, -4.7) * mm]});
            skFitSpline(sketch, "E378", {"points": [v(6.07, -4.7) * mm, v(6.04, -4.74) * mm, v(5.96, -4.73) * mm, v(5.88, -4.67) * mm]});
            skFitSpline(sketch, "E379", {"points": [v(5.88, -4.67) * mm, v(5.78, -4.58) * mm, v(5.74, -4.58) * mm, v(5.7, -4.66) * mm]});
            skFitSpline(sketch, "E380", {"points": [v(5.7, -4.66) * mm, v(5.65, -4.72) * mm, v(5.46, -4.75) * mm, v(5.08, -4.73) * mm]});
            skFitSpline(sketch, "E381", {"points": [v(4.2, -5.3) * mm, v(4.02, -5.62) * mm, v(3.87, -5.92) * mm, v(3.86, -5.98) * mm]});
            skFitSpline(sketch, "E382", {"points": [v(3.86, -5.98) * mm, v(3.85, -6.19) * mm, v(4.1, -6.06) * mm, v(4.23, -5.78) * mm]});
            skFitSpline(sketch, "E383", {"points": [v(7.17, -4.96) * mm, v(7.37, -4.75) * mm, v(7.47, -4.54) * mm, v(7.55, -4.24) * mm]});
            skFitSpline(sketch, "E384", {"points": [v(7.44, -4.26) * mm, v(7.35, -4.4) * mm, v(7.22, -4.51) * mm, v(7.16, -4.51) * mm]});
            skFitSpline(sketch, "E385", {"points": [v(7.16, -4.51) * mm, v(7.02, -4.51) * mm, v(6.88, -4.75) * mm, v(6.88, -4.97) * mm]});
            skFitSpline(sketch, "E386", {"points": [v(6.88, -4.97) * mm, v(6.88, -5.18) * mm, v(6.97, -5.18) * mm, v(7.17, -4.96) * mm]});
            skFitSpline(sketch, "E387", {"points": [v(4.53, -3.89) * mm, v(4.56, -3.78) * mm, v(4.47, -3.9) * mm, v(4.34, -4.14) * mm]});
            skFitSpline(sketch, "E388", {"points": [v(4.34, -4.14) * mm, v(4.2, -4.39) * mm, v(4.1, -4.63) * mm, v(4.1, -4.69) * mm]});
            skFitSpline(sketch, "E389", {"points": [v(4.1, -4.69) * mm, v(4.1, -4.8) * mm, v(4.45, -4.15) * mm, v(4.53, -3.89) * mm]});
            skFitSpline(sketch, "E390", {"points": [v(5.1, -4.32) * mm, v(5.2, -4.2) * mm, v(5.33, -4.12) * mm, v(5.37, -4.12) * mm]});
            skFitSpline(sketch, "E391", {"points": [v(5.37, -4.12) * mm, v(5.4, -4.12) * mm, v(5.46, -4.05) * mm, v(5.49, -3.96) * mm]});
            skFitSpline(sketch, "E392", {"points": [v(5.49, -3.96) * mm, v(5.54, -3.8) * mm, v(5.69, -3.75) * mm, v(5.68, -3.9) * mm]});
            skFitSpline(sketch, "E393", {"points": [v(5.68, -3.9) * mm, v(5.68, -3.96) * mm, v(5.63, -4.07) * mm, v(5.56, -4.15) * mm]});
            skFitSpline(sketch, "E394", {"points": [v(5.56, -4.15) * mm, v(5.42, -4.35) * mm, v(5.41, -4.51) * mm, v(5.56, -4.51) * mm]});
            skFitSpline(sketch, "E395", {"points": [v(5.56, -4.51) * mm, v(5.62, -4.51) * mm, v(5.79, -4.32) * mm, v(5.93, -4.08) * mm]});
            skFitSpline(sketch, "E396", {"points": [v(5.93, -4.08) * mm, v(6.08, -3.85) * mm, v(6.23, -3.65) * mm, v(6.26, -3.65) * mm]});
            skFitSpline(sketch, "E397", {"points": [v(6.26, -3.65) * mm, v(6.37, -3.65) * mm, v(6.32, -3.82) * mm, v(6.16, -4.02) * mm]});
            skFitSpline(sketch, "E398", {"points": [v(6.16, -4.02) * mm, v(6.07, -4.13) * mm, v(6, -4.29) * mm, v(6, -4.37) * mm]});
            skFitSpline(sketch, "E399", {"points": [v(6, -4.37) * mm, v(6, -4.62) * mm, v(6.3, -4.4) * mm, v(6.54, -3.96) * mm]});
            skFitSpline(sketch, "E400", {"points": [v(6.54, -3.96) * mm, v(6.74, -3.61) * mm, v(6.96, -3.47) * mm, v(6.89, -3.74) * mm]});
            skFitSpline(sketch, "E401", {"points": [v(6.89, -3.74) * mm, v(6.87, -3.8) * mm, v(6.85, -3.93) * mm, v(6.83, -4.04) * mm]});
            skFitSpline(sketch, "E402", {"points": [v(6.83, -4.04) * mm, v(6.8, -4.14) * mm, v(6.77, -4.26) * mm, v(6.75, -4.3) * mm]});
            skFitSpline(sketch, "E403", {"points": [v(6.75, -4.3) * mm, v(6.73, -4.33) * mm, v(6.74, -4.35) * mm, v(6.79, -4.35) * mm]});
            skFitSpline(sketch, "E404", {"points": [v(6.79, -4.35) * mm, v(6.93, -4.35) * mm, v(7.27, -3.88) * mm, v(7.36, -3.55) * mm]});
            skFitSpline(sketch, "E405", {"points": [v(7.36, -3.55) * mm, v(7.41, -3.37) * mm, v(7.49, -3.1) * mm, v(7.53, -2.97) * mm]});
            skFitSpline(sketch, "E406", {"points": [v(7.53, -2.97) * mm, v(7.57, -2.83) * mm, v(7.76, -2.58) * mm, v(7.96, -2.41) * mm]});
            skFitSpline(sketch, "E407", {"points": [v(7.96, -2.41) * mm, v(8.15, -2.24) * mm, v(8.3, -2.07) * mm, v(8.3, -2.02) * mm]});
            skFitSpline(sketch, "E408", {"points": [v(8.3, -2.02) * mm, v(8.3, -1.97) * mm, v(8.37, -1.84) * mm, v(8.43, -1.74) * mm]});
            skFitSpline(sketch, "E409", {"points": [v(8.43, -1.74) * mm, v(8.6, -1.48) * mm, v(8.52, -1.26) * mm, v(8.22, -1.2) * mm]});
            skFitSpline(sketch, "E410", {"points": [v(8.22, -1.2) * mm, v(7.78, -1.11) * mm, v(7.67, -1.14) * mm, v(6.92, -1.58) * mm]});
            skFitSpline(sketch, "E411", {"points": [v(6.92, -1.58) * mm, v(5.87, -2.2) * mm, v(5.04, -3.14) * mm, v(4.77, -4) * mm]});
            skFitSpline(sketch, "E412", {"points": [v(4.77, -4) * mm, v(4.6, -4.55) * mm, v(4.74, -4.67) * mm, v(5.1, -4.32) * mm]});
            skFitSpline(sketch, "E413", {"points": [v(7.29, -4.19) * mm, v(7.42, -4.03) * mm, v(7.48, -3.89) * mm, v(7.4, -3.89) * mm]});
            skFitSpline(sketch, "E414", {"points": [v(7.4, -3.89) * mm, v(7.38, -3.89) * mm, v(7.29, -4) * mm, v(7.2, -4.12) * mm]});
            skFitSpline(sketch, "E415", {"points": [v(7.2, -4.12) * mm, v(7, -4.39) * mm, v(7.06, -4.44) * mm, v(7.29, -4.19) * mm]});
            skFitSpline(sketch, "E416", {"points": [v(8.71, -2.98) * mm, v(8.72, -2.89) * mm, v(8.73, -2.87) * mm, v(8.76, -2.93) * mm]});
            skFitSpline(sketch, "E417", {"points": [v(8.76, -2.93) * mm, v(8.78, -2.99) * mm, v(8.78, -3.06) * mm, v(8.75, -3.08) * mm]});
            skFitSpline(sketch, "E418", {"points": [v(8.75, -3.08) * mm, v(8.73, -3.1) * mm, v(8.7, -3.06) * mm, v(8.71, -2.98) * mm]});
            skFitSpline(sketch, "E419", {"points": [v(7.78, -0.28) * mm, v(7.3, -0.2) * mm, v(6.04, 0.48) * mm, v(5.57, 0.9) * mm]});
            skFitSpline(sketch, "E420", {"points": [v(5.57, 0.9) * mm, v(5.27, 1.17) * mm, v(5.06, 1.46) * mm, v(4.79, 2) * mm]});
            skFitSpline(sketch, "E421", {"points": [v(4.79, 2) * mm, v(4.59, 2.4) * mm, v(4.39, 2.88) * mm, v(4.35, 3.04) * mm]});
            skFitSpline(sketch, "E422", {"points": [v(4.35, 3.04) * mm, v(4.19, 3.7) * mm, v(3.16, 5.52) * mm, v(3.08, 5.28) * mm]});
            skFitSpline(sketch, "E423", {"points": [v(3.08, 5.28) * mm, v(3.06, 5.22) * mm, v(2.6, 5.66) * mm, v(1.99, 6.32) * mm]});
            skFitSpline(sketch, "E424", {"points": [v(1.99, 6.32) * mm, v(1.89, 6.43) * mm, v(1.02, 6.96) * mm, v(0.74, 7.08) * mm]});
            skFitSpline(sketch, "E425", {"points": [v(0.74, 7.08) * mm, v(0.62, 7.13) * mm, v(0.53, 7.21) * mm, v(0.55, 7.25) * mm]});
            skFitSpline(sketch, "E426", {"points": [v(0.55, 7.25) * mm, v(0.63, 7.5) * mm, v(2.23, 7.06) * mm, v(3.14, 6.56) * mm]});
            skFitSpline(sketch, "E427", {"points": [v(3.14, 6.56) * mm, v(3.67, 6.26) * mm, v(3.89, 6.25) * mm, v(3.51, 6.55) * mm]});
            skFitSpline(sketch, "E428", {"points": [v(3.51, 6.55) * mm, v(3.37, 6.66) * mm, v(3.32, 6.75) * mm, v(3.37, 6.78) * mm]});
            skFitSpline(sketch, "E429", {"points": [v(3.37, 6.78) * mm, v(3.5, 6.86) * mm, v(4.16, 6.52) * mm, v(4.33, 6.3) * mm]});
            skFitSpline(sketch, "E430", {"points": [v(4.33, 6.3) * mm, v(4.41, 6.2) * mm, v(4.5, 6.12) * mm, v(4.52, 6.12) * mm]});
            skFitSpline(sketch, "E431", {"points": [v(4.52, 6.12) * mm, v(4.63, 6.12) * mm, v(4.56, 6.28) * mm, v(4.37, 6.5) * mm]});
            skFitSpline(sketch, "E432", {"points": [v(4.37, 6.5) * mm, v(4.26, 6.63) * mm, v(4.2, 6.76) * mm, v(4.24, 6.78) * mm]});
            skFitSpline(sketch, "E433", {"points": [v(4.24, 6.78) * mm, v(4.33, 6.83) * mm, v(4.84, 6.47) * mm, v(5.12, 6.17) * mm]});
            skFitSpline(sketch, "E434", {"points": [v(5.12, 6.17) * mm, v(5.23, 6.06) * mm, v(5.35, 5.97) * mm, v(5.38, 5.97) * mm]});
            skFitSpline(sketch, "E435", {"points": [v(5.38, 5.97) * mm, v(5.51, 5.97) * mm, v(5.44, 6.23) * mm, v(5.25, 6.48) * mm]});
            skFitSpline(sketch, "E436", {"points": [v(5.25, 6.48) * mm, v(5, 6.79) * mm, v(5, 6.83) * mm, v(5.2, 6.83) * mm]});
            skFitSpline(sketch, "E437", {"points": [v(5.2, 6.83) * mm, v(5.44, 6.83) * mm, v(5.8, 6.44) * mm, v(6.04, 5.9) * mm]});
            skFitSpline(sketch, "E438", {"points": [v(6.04, 5.9) * mm, v(6.19, 5.6) * mm, v(6.3, 5.44) * mm, v(6.35, 5.5) * mm]});
            skFitSpline(sketch, "E439", {"points": [v(6.35, 5.5) * mm, v(6.4, 5.54) * mm, v(6.39, 5.66) * mm, v(6.33, 5.82) * mm]});
            skFitSpline(sketch, "E440", {"points": [v(6.33, 5.82) * mm, v(6.27, 5.98) * mm, v(6.27, 6.1) * mm, v(6.31, 6.15) * mm]});
            skFitSpline(sketch, "E441", {"points": [v(6.31, 6.15) * mm, v(6.42, 6.26) * mm, v(6.56, 6.14) * mm, v(6.56, 5.93) * mm]});
            skFitSpline(sketch, "E442", {"points": [v(6.56, 5.93) * mm, v(6.56, 5.83) * mm, v(6.61, 5.7) * mm, v(6.67, 5.66) * mm]});
            skFitSpline(sketch, "E443", {"points": [v(6.67, 5.66) * mm, v(6.73, 5.6) * mm, v(6.8, 5.4) * mm, v(6.84, 5.18) * mm]});
            skFitSpline(sketch, "E444", {"points": [v(6.84, 5.18) * mm, v(6.9, 4.75) * mm, v(6.96, 4.74) * mm, v(7.08, 5.16) * mm]});
            skFitSpline(sketch, "E445", {"points": [v(7.08, 5.16) * mm, v(7.19, 5.54) * mm, v(7.3, 5.52) * mm, v(7.36, 5.1) * mm]});
            skFitSpline(sketch, "E446", {"points": [v(7.36, 5.1) * mm, v(7.38, 4.91) * mm, v(7.43, 4.7) * mm, v(7.48, 4.64) * mm]});
            skFitSpline(sketch, "E447", {"points": [v(7.48, 4.64) * mm, v(7.52, 4.57) * mm, v(7.55, 4.22) * mm, v(7.56, 3.86) * mm]});
            skFitSpline(sketch, "E448", {"points": [v(7.56, 3.86) * mm, v(7.56, 3.37) * mm, v(7.62, 3) * mm, v(7.77, 2.52) * mm]});
            skFitSpline(sketch, "E449", {"points": [v(7.77, 2.52) * mm, v(8, 1.76) * mm, v(8.1, 1.57) * mm, v(8.5, 0.97) * mm]});
            skFitSpline(sketch, "E450", {"points": [v(8.5, 0.97) * mm, v(8.8, 0.53) * mm, v(8.87, 0.16) * mm, v(8.69, -0.07) * mm]});
            skFitSpline(sketch, "E451", {"points": [v(8.69, -0.07) * mm, v(8.53, -0.25) * mm, v(8.15, -0.34) * mm, v(7.78, -0.28) * mm]});
            skFitSpline(sketch, "E452", {"points": [v(8.52, 0.09) * mm, v(8.67, 0.28) * mm, v(8.65, 0.52) * mm, v(8.47, 0.7) * mm]});
            skFitSpline(sketch, "E453", {"points": [v(8.47, 0.7) * mm, v(8.31, 0.87) * mm, v(7.68, 1.96) * mm, v(7.5, 2.37) * mm]});
            skFitSpline(sketch, "E454", {"points": [v(7.5, 2.37) * mm, v(7.42, 2.57) * mm, v(7.06, 2.9) * mm, v(6.93, 2.91) * mm]});
            skFitSpline(sketch, "E455", {"points": [v(6.93, 2.91) * mm, v(6.89, 2.92) * mm, v(6.88, 2.74) * mm, v(6.9, 2.53) * mm]});
            skFitSpline(sketch, "E456", {"points": [v(6.9, 2.53) * mm, v(6.93, 2.31) * mm, v(6.92, 2.14) * mm, v(6.9, 2.14) * mm]});
            skFitSpline(sketch, "E457", {"points": [v(6.9, 2.14) * mm, v(6.77, 2.14) * mm, v(6.66, 2.27) * mm, v(6.6, 2.52) * mm]});
            skFitSpline(sketch, "E458", {"points": [v(6.6, 2.52) * mm, v(6.55, 2.67) * mm, v(6.47, 2.8) * mm, v(6.4, 2.82) * mm]});
            skFitSpline(sketch, "E459", {"points": [v(6.4, 2.82) * mm, v(6.32, 2.85) * mm, v(6.31, 2.78) * mm, v(6.36, 2.49) * mm]});
            skFitSpline(sketch, "E460", {"points": [v(6.36, 2.49) * mm, v(6.43, 2) * mm, v(6.25, 2.04) * mm, v(6.12, 2.55) * mm]});
            skFitSpline(sketch, "E461", {"points": [v(6.12, 2.55) * mm, v(5.97, 3.14) * mm, v(5.8, 3.17) * mm, v(5.83, 2.6) * mm]});
            skFitSpline(sketch, "E462", {"points": [v(5.83, 2.6) * mm, v(5.84, 2.43) * mm, v(5.8, 2.3) * mm, v(5.76, 2.3) * mm]});
            skFitSpline(sketch, "E463", {"points": [v(5.76, 2.3) * mm, v(5.69, 2.3) * mm, v(5.65, 2.4) * mm, v(5.68, 2.58) * mm]});
            skFitSpline(sketch, "E464", {"points": [v(5.68, 2.58) * mm, v(5.69, 2.64) * mm, v(5.63, 2.8) * mm, v(5.55, 2.93) * mm]});
            skFitSpline(sketch, "E465", {"points": [v(5.38, 2.98) * mm, v(5.35, 2.73) * mm, v(5.2, 2.68) * mm, v(5.2, 2.92) * mm]});
            skFitSpline(sketch, "E466", {"points": [v(5.2, 2.92) * mm, v(5.2, 3) * mm, v(5.16, 3.1) * mm, v(5.1, 3.12) * mm]});
            skFitSpline(sketch, "E467", {"points": [v(5.1, 3.12) * mm, v(5.04, 3.14) * mm, v(4.97, 3.23) * mm, v(4.95, 3.31) * mm]});
            skFitSpline(sketch, "E468", {"points": [v(4.95, 3.31) * mm, v(4.9, 3.48) * mm, v(4.71, 3.51) * mm, v(4.59, 3.37) * mm]});
            skFitSpline(sketch, "E469", {"points": [v(4.59, 3.37) * mm, v(4.48, 3.24) * mm, v(4.67, 2.7) * mm, v(5.09, 1.94) * mm]});
            skFitSpline(sketch, "E470", {"points": [v(5.09, 1.94) * mm, v(5.5, 1.18) * mm, v(5.75, 0.93) * mm, v(6.68, 0.41) * mm]});
            skFitSpline(sketch, "E471", {"points": [v(6.68, 0.41) * mm, v(7.54, -0.07) * mm, v(7.7, -0.13) * mm, v(8.07, -0.09) * mm]});
            skFitSpline(sketch, "E472", {"points": [v(8.07, -0.09) * mm, v(8.26, -0.06) * mm, v(8.47, 0.02) * mm, v(8.52, 0.09) * mm]});
            skFitSpline(sketch, "E473", {"points": [v(6.76, 3.08) * mm, v(6.82, 3.17) * mm, v(7.02, 3.15) * mm, v(7.31, 3.03) * mm]});
            skFitSpline(sketch, "E474", {"points": [v(7.31, 3.03) * mm, v(7.47, 2.97) * mm, v(7.47, 2.97) * mm, v(7.33, 3.1) * mm]});
            skFitSpline(sketch, "E475", {"points": [v(7.33, 3.1) * mm, v(7.26, 3.18) * mm, v(7.2, 3.28) * mm, v(7.2, 3.33) * mm]});
            skFitSpline(sketch, "E476", {"points": [v(7.2, 3.33) * mm, v(7.2, 3.45) * mm, v(6.79, 3.86) * mm, v(6.66, 3.86) * mm]});
            skFitSpline(sketch, "E477", {"points": [v(6.66, 3.86) * mm, v(6.6, 3.86) * mm, v(6.56, 3.77) * mm, v(6.56, 3.66) * mm]});
            skFitSpline(sketch, "E478", {"points": [v(6.56, 3.66) * mm, v(6.56, 3.54) * mm, v(6.51, 3.46) * mm, v(6.44, 3.46) * mm]});
            skFitSpline(sketch, "E479", {"points": [v(6.44, 3.46) * mm, v(6.36, 3.46) * mm, v(6.32, 3.54) * mm, v(6.32, 3.68) * mm]});
            skFitSpline(sketch, "E480", {"points": [v(6.32, 3.68) * mm, v(6.32, 3.97) * mm, v(6.2, 4.13) * mm, v(6.07, 4.04) * mm]});
            skFitSpline(sketch, "E481", {"points": [v(6.07, 4.04) * mm, v(6.01, 4) * mm, v(5.87, 3.97) * mm, v(5.75, 3.96) * mm]});
            skFitSpline(sketch, "E482", {"points": [v(5.75, 3.96) * mm, v(5.57, 3.95) * mm, v(5.53, 4) * mm, v(5.49, 4.23) * mm]});
            skFitSpline(sketch, "E483", {"points": [v(5.28, 4.32) * mm, v(5.14, 4.14) * mm, v(5.13, 4.14) * mm, v(5.13, 4.29) * mm]});
            skFitSpline(sketch, "E484", {"points": [v(5.13, 4.29) * mm, v(5.13, 4.37) * mm, v(5.09, 4.5) * mm, v(5.04, 4.56) * mm]});
            skFitSpline(sketch, "E485", {"points": [v(5.04, 4.56) * mm, v(4.98, 4.65) * mm, v(4.97, 4.63) * mm, v(5, 4.47) * mm]});
            skFitSpline(sketch, "E486", {"points": [v(5, 4.47) * mm, v(5.03, 4.35) * mm, v(5.07, 4.2) * mm, v(5.1, 4.14) * mm]});
            skFitSpline(sketch, "E487", {"points": [v(5.1, 4.14) * mm, v(5.12, 4.07) * mm, v(5.1, 4.01) * mm, v(5.07, 4.01) * mm]});
            skFitSpline(sketch, "E488", {"points": [v(5.07, 4.01) * mm, v(5.02, 4.01) * mm, v(4.94, 4.19) * mm, v(4.9, 4.4) * mm]});
            skFitSpline(sketch, "E489", {"points": [v(4.9, 4.4) * mm, v(4.84, 4.62) * mm, v(4.76, 4.8) * mm, v(4.72, 4.8) * mm]});
            skFitSpline(sketch, "E490", {"points": [v(4.72, 4.8) * mm, v(4.68, 4.8) * mm, v(4.68, 4.73) * mm, v(4.73, 4.64) * mm]});
            skFitSpline(sketch, "E491", {"points": [v(4.73, 4.64) * mm, v(4.79, 4.54) * mm, v(4.79, 4.47) * mm, v(4.73, 4.44) * mm]});
            skFitSpline(sketch, "E492", {"points": [v(4.73, 4.44) * mm, v(4.68, 4.41) * mm, v(4.67, 4.32) * mm, v(4.7, 4.24) * mm]});
            skFitSpline(sketch, "E493", {"points": [v(4.7, 4.24) * mm, v(4.72, 4.16) * mm, v(4.7, 4.09) * mm, v(4.66, 4.09) * mm]});
            skFitSpline(sketch, "E494", {"points": [v(4.66, 4.09) * mm, v(4.62, 4.09) * mm, v(4.54, 4.23) * mm, v(4.5, 4.4) * mm]});
            skFitSpline(sketch, "E495", {"points": [v(4.5, 4.4) * mm, v(4.4, 4.72) * mm, v(4.1, 4.98) * mm, v(3.94, 4.87) * mm]});
            skFitSpline(sketch, "E496", {"points": [v(3.94, 4.87) * mm, v(3.86, 4.83) * mm, v(3.9, 4.67) * mm, v(4.13, 4.22) * mm]});
            skFitSpline(sketch, "E497", {"points": [v(4.13, 4.22) * mm, v(4.28, 3.9) * mm, v(4.41, 3.58) * mm, v(4.42, 3.53) * mm]});
            skFitSpline(sketch, "E498", {"points": [v(4.42, 3.53) * mm, v(4.42, 3.46) * mm, v(4.46, 3.47) * mm, v(4.52, 3.56) * mm]});
            skFitSpline(sketch, "E499", {"points": [v(4.52, 3.56) * mm, v(4.64, 3.72) * mm, v(4.85, 3.74) * mm, v(4.93, 3.62) * mm]});
            skFitSpline(sketch, "E500", {"points": [v(4.93, 3.62) * mm, v(4.96, 3.57) * mm, v(5.03, 3.55) * mm, v(5.1, 3.57) * mm]});
            skFitSpline(sketch, "E501", {"points": [v(5.1, 3.57) * mm, v(5.15, 3.6) * mm, v(5.29, 3.54) * mm, v(5.4, 3.45) * mm]});
            skFitSpline(sketch, "E502", {"points": [v(5.4, 3.45) * mm, v(5.51, 3.37) * mm, v(5.64, 3.32) * mm, v(5.7, 3.35) * mm]});
            skFitSpline(sketch, "E503", {"points": [v(5.7, 3.35) * mm, v(5.74, 3.38) * mm, v(5.86, 3.32) * mm, v(5.97, 3.23) * mm]});
            skFitSpline(sketch, "E504", {"points": [v(5.97, 3.23) * mm, v(6.12, 3.09) * mm, v(6.18, 3.07) * mm, v(6.27, 3.14) * mm]});
            skFitSpline(sketch, "E505", {"points": [v(6.27, 3.14) * mm, v(6.35, 3.21) * mm, v(6.4, 3.2) * mm, v(6.48, 3.11) * mm]});
            skFitSpline(sketch, "E506", {"points": [v(6.48, 3.11) * mm, v(6.6, 2.97) * mm, v(6.69, 2.96) * mm, v(6.76, 3.08) * mm]});
            skFitSpline(sketch, "E507", {"points": [v(7.33, 4.18) * mm, v(7.28, 4.57) * mm, v(7.25, 4.6) * mm, v(7.06, 4.48) * mm]});
            skFitSpline(sketch, "E508", {"points": [v(7.06, 4.48) * mm, v(6.9, 4.38) * mm, v(6.9, 4.38) * mm, v(7.07, 4.09) * mm]});
            skFitSpline(sketch, "E509", {"points": [v(7.07, 4.09) * mm, v(7.27, 3.72) * mm, v(7.39, 3.77) * mm, v(7.33, 4.18) * mm]});
            skFitSpline(sketch, "E510", {"points": [v(6.57, 4.3) * mm, v(6.69, 4.44) * mm, v(6.68, 4.71) * mm, v(6.55, 5.05) * mm]});
            skFitSpline(sketch, "E511", {"points": [v(6.55, 5.05) * mm, v(6.47, 5.25) * mm, v(6.45, 5.26) * mm, v(6.32, 5.15) * mm]});
            skFitSpline(sketch, "E512", {"points": [v(6.32, 5.15) * mm, v(6.1, 4.95) * mm, v(6.02, 5) * mm, v(5.95, 5.44) * mm]});
            skFitSpline(sketch, "E513", {"points": [v(5.95, 5.44) * mm, v(5.9, 5.78) * mm, v(5.85, 5.85) * mm, v(5.7, 5.87) * mm]});
            skFitSpline(sketch, "E514", {"points": [v(5.7, 5.87) * mm, v(5.56, 5.9) * mm, v(5.53, 5.86) * mm, v(5.53, 5.7) * mm]});
            skFitSpline(sketch, "E515", {"points": [v(5.53, 5.7) * mm, v(5.53, 5.43) * mm, v(5.33, 5.44) * mm, v(5.15, 5.71) * mm]});
            skFitSpline(sketch, "E516", {"points": [v(5.15, 5.71) * mm, v(4.94, 6.04) * mm, v(4.73, 6.15) * mm, v(4.73, 5.93) * mm]});
            skFitSpline(sketch, "E517", {"points": [v(4.73, 5.93) * mm, v(4.73, 5.87) * mm, v(4.66, 5.78) * mm, v(4.57, 5.73) * mm]});
            skFitSpline(sketch, "E518", {"points": [v(4.57, 5.73) * mm, v(4.45, 5.67) * mm, v(4.41, 5.67) * mm, v(4.41, 5.76) * mm]});
            skFitSpline(sketch, "E519", {"points": [v(4.41, 5.76) * mm, v(4.41, 5.92) * mm, v(4.1, 6.28) * mm, v(3.97, 6.28) * mm]});
            skFitSpline(sketch, "E520", {"points": [v(3.97, 6.28) * mm, v(3.9, 6.28) * mm, v(3.86, 6.22) * mm, v(3.87, 6.15) * mm]});
            skFitSpline(sketch, "E521", {"points": [v(3.87, 6.15) * mm, v(3.91, 5.93) * mm, v(3.64, 5.94) * mm, v(3.13, 6.16) * mm]});
            skFitSpline(sketch, "E522", {"points": [v(3.13, 6.16) * mm, v(2.87, 6.28) * mm, v(2.64, 6.36) * mm, v(2.62, 6.34) * mm]});
            skFitSpline(sketch, "E523", {"points": [v(2.62, 6.34) * mm, v(2.6, 6.32) * mm, v(2.81, 6.08) * mm, v(3.1, 5.8) * mm]});
            skFitSpline(sketch, "E524", {"points": [v(3.1, 5.8) * mm, v(3.38, 5.54) * mm, v(3.64, 5.25) * mm, v(3.66, 5.17) * mm]});
            skFitSpline(sketch, "E525", {"points": [v(3.66, 5.17) * mm, v(3.7, 5.06) * mm, v(3.74, 5.04) * mm, v(3.81, 5.1) * mm]});
            skFitSpline(sketch, "E526", {"points": [v(3.81, 5.1) * mm, v(3.93, 5.2) * mm, v(4.28, 5.1) * mm, v(4.37, 4.95) * mm]});
            skFitSpline(sketch, "E527", {"points": [v(4.37, 4.95) * mm, v(4.41, 4.9) * mm, v(4.46, 4.9) * mm, v(4.53, 5) * mm]});
            skFitSpline(sketch, "E528", {"points": [v(4.53, 5) * mm, v(4.63, 5.14) * mm, v(4.65, 5.14) * mm, v(4.8, 5) * mm]});
            skFitSpline(sketch, "E529", {"points": [v(4.8, 5) * mm, v(4.87, 4.93) * mm, v(4.99, 4.87) * mm, v(5.04, 4.87) * mm]});
            skFitSpline(sketch, "E530", {"points": [v(5.04, 4.87) * mm, v(5.1, 4.87) * mm, v(5.25, 4.8) * mm, v(5.38, 4.7) * mm]});
            skFitSpline(sketch, "E531", {"points": [v(5.38, 4.7) * mm, v(5.6, 4.55) * mm, v(5.62, 4.55) * mm, v(5.72, 4.69) * mm]});
            skFitSpline(sketch, "E532", {"points": [v(5.72, 4.69) * mm, v(5.84, 4.85) * mm, v(5.86, 4.83) * mm, v(6.21, 4.34) * mm]});
            skFitSpline(sketch, "E533", {"points": [v(6.21, 4.34) * mm, v(6.36, 4.13) * mm, v(6.43, 4.13) * mm, v(6.57, 4.3) * mm]});
            skFitSpline(sketch, "E534", {"points": [v(7.2, 4.72) * mm, v(7.2, 4.76) * mm, v(7.16, 4.8) * mm, v(7.12, 4.8) * mm]});
            skFitSpline(sketch, "E535", {"points": [v(7.12, 4.8) * mm, v(7.08, 4.8) * mm, v(7.02, 4.76) * mm, v(7, 4.72) * mm]});
            skFitSpline(sketch, "E536", {"points": [v(7, 4.72) * mm, v(6.97, 4.67) * mm, v(7, 4.64) * mm, v(7.07, 4.64) * mm]});
            skFitSpline(sketch, "E537", {"points": [v(7.07, 4.64) * mm, v(7.14, 4.64) * mm, v(7.2, 4.67) * mm, v(7.2, 4.72) * mm]});
            skFitSpline(sketch, "E538", {"points": [v(2.43, 6.51) * mm, v(2.43, 6.56) * mm, v(2.39, 6.6) * mm, v(2.34, 6.6) * mm]});
            skFitSpline(sketch, "E539", {"points": [v(2.34, 6.6) * mm, v(2.3, 6.6) * mm, v(2.28, 6.56) * mm, v(2.3, 6.51) * mm]});
            skFitSpline(sketch, "E540", {"points": [v(2.3, 6.51) * mm, v(2.33, 6.47) * mm, v(2.37, 6.44) * mm, v(2.4, 6.44) * mm]});
            skFitSpline(sketch, "E541", {"points": [v(2.4, 6.44) * mm, v(2.41, 6.44) * mm, v(2.43, 6.47) * mm, v(2.43, 6.51) * mm]});
            skFitSpline(sketch, "E542", {"points": [v(-5.28, -8.27) * mm, v(-5.28, -8.23) * mm, v(-5.32, -8.17) * mm, v(-5.36, -8.15) * mm]});
            skFitSpline(sketch, "E543", {"points": [v(-5.36, -8.15) * mm, v(-5.4, -8.12) * mm, v(-5.44, -8.15) * mm, v(-5.44, -8.22) * mm]});
            skFitSpline(sketch, "E544", {"points": [v(-5.44, -8.22) * mm, v(-5.44, -8.29) * mm, v(-5.4, -8.34) * mm, v(-5.36, -8.34) * mm]});
            skFitSpline(sketch, "E545", {"points": [v(-5.36, -8.34) * mm, v(-5.32, -8.34) * mm, v(-5.28, -8.3) * mm, v(-5.28, -8.27) * mm]});
            skFitSpline(sketch, "E546", {"points": [v(-1.67, -7.16) * mm, v(-1.34, -7.07) * mm, v(-0.82, -6.86) * mm, v(-0.75, -6.78) * mm]});
            skFitSpline(sketch, "E547", {"points": [v(-0.75, -6.78) * mm, v(-0.73, -6.75) * mm, v(-0.54, -6.65) * mm, v(-0.34, -6.55) * mm]});
            skFitSpline(sketch, "E548", {"points": [v(-0.34, -6.55) * mm, v(-0.13, -6.45) * mm, v(0.04, -6.34) * mm, v(0.04, -6.3) * mm]});
            skFitSpline(sketch, "E549", {"points": [v(0.04, -6.3) * mm, v(0.04, -6.26) * mm, v(0.08, -6.23) * mm, v(0.12, -6.23) * mm]});
            skFitSpline(sketch, "E550", {"points": [v(0.12, -6.23) * mm, v(0.26, -6.23) * mm, v(1.3, -5.53) * mm, v(1.67, -5.18) * mm]});
            skFitSpline(sketch, "E551", {"points": [v(1.67, -5.18) * mm, v(2.03, -4.86) * mm, v(2.1, -4.75) * mm, v(1.95, -4.75) * mm]});
            skFitSpline(sketch, "E552", {"points": [v(1.95, -4.75) * mm, v(1.84, -4.75) * mm, v(1.22, -4.34) * mm, v(1.1, -4.2) * mm]});
            skFitSpline(sketch, "E553", {"points": [v(1.1, -4.2) * mm, v(0.93, -3.99) * mm, v(1.07, -4.01) * mm, v(1.37, -4.25) * mm]});
            skFitSpline(sketch, "E554", {"points": [v(1.37, -4.25) * mm, v(1.82, -4.6) * mm, v(1.92, -4.64) * mm, v(1.74, -4.41) * mm]});
            skFitSpline(sketch, "E555", {"points": [v(1.74, -4.41) * mm, v(1.53, -4.13) * mm, v(1.18, -3.94) * mm, v(1, -4) * mm]});
            skFitSpline(sketch, "E556", {"points": [v(1, -4) * mm, v(0.87, -4.04) * mm, v(0.84, -4.12) * mm, v(0.84, -4.42) * mm]});
            skFitSpline(sketch, "E557", {"points": [v(0.84, -4.42) * mm, v(0.84, -4.9) * mm, v(0.77, -4.96) * mm, v(0.59, -4.67) * mm]});
            skFitSpline(sketch, "E558", {"points": [v(0.59, -4.67) * mm, v(0.32, -4.24) * mm, v(-0.67, -3.65) * mm, v(-1.12, -3.65) * mm]});
            skFitSpline(sketch, "E559", {"points": [v(-1.12, -3.65) * mm, v(-1.36, -3.65) * mm, v(-1.36, -3.7) * mm, v(-1.13, -3.95) * mm]});
            skFitSpline(sketch, "E560", {"points": [v(-1.18, -4.32) * mm, v(-1.3, -4.43) * mm, v(-1.47, -4.51) * mm, v(-1.56, -4.51) * mm]});
            skFitSpline(sketch, "E561", {"points": [v(-1.56, -4.51) * mm, v(-1.71, -4.51) * mm, v(-1.7, -4.52) * mm, v(-1.52, -4.88) * mm]});
            skFitSpline(sketch, "E562", {"points": [v(-1.52, -4.88) * mm, v(-1.4, -5.09) * mm, v(-1.25, -5.42) * mm, v(-1.18, -5.63) * mm]});
            skFitSpline(sketch, "E563", {"points": [v(-1.18, -5.63) * mm, v(-1.1, -5.84) * mm, v(-0.94, -6.1) * mm, v(-0.82, -6.22) * mm]});
            skFitSpline(sketch, "E564", {"points": [v(-0.82, -6.22) * mm, v(-0.66, -6.37) * mm, v(-0.62, -6.46) * mm, v(-0.67, -6.54) * mm]});
            skFitSpline(sketch, "E565", {"points": [v(-0.67, -6.54) * mm, v(-0.73, -6.64) * mm, v(-0.75, -6.64) * mm, v(-0.8, -6.52) * mm]});
            skFitSpline(sketch, "E566", {"points": [v(-0.8, -6.52) * mm, v(-0.83, -6.45) * mm, v(-0.88, -6.39) * mm, v(-0.92, -6.39) * mm]});
            skFitSpline(sketch, "E567", {"points": [v(-0.92, -6.39) * mm, v(-0.97, -6.39) * mm, v(-1.08, -6.3) * mm, v(-1.17, -6.2) * mm]});
            skFitSpline(sketch, "E568", {"points": [v(-1.17, -6.2) * mm, v(-1.34, -6.01) * mm, v(-1.97, -5.67) * mm, v(-2.32, -5.57) * mm]});
            skFitSpline(sketch, "E569", {"points": [v(-2.32, -5.57) * mm, v(-2.44, -5.53) * mm, v(-2.57, -5.59) * mm, v(-2.77, -5.77) * mm]});
            skFitSpline(sketch, "E570", {"points": [v(-2.77, -5.77) * mm, v(-2.93, -5.9) * mm, v(-3.06, -6.06) * mm, v(-3.06, -6.12) * mm]});
            skFitSpline(sketch, "E571", {"points": [v(-3.06, -6.12) * mm, v(-3.06, -6.18) * mm, v(-3.1, -6.23) * mm, v(-3.14, -6.23) * mm]});
            skFitSpline(sketch, "E572", {"points": [v(-3.14, -6.23) * mm, v(-3.18, -6.23) * mm, v(-3.22, -6.11) * mm, v(-3.22, -5.96) * mm]});
            skFitSpline(sketch, "E573", {"points": [v(-3.22, -5.96) * mm, v(-3.22, -5.5) * mm, v(-3.28, -5.43) * mm, v(-3.53, -5.56) * mm]});
            skFitSpline(sketch, "E574", {"points": [v(-3.53, -5.56) * mm, v(-3.65, -5.63) * mm, v(-3.82, -5.66) * mm, v(-3.91, -5.63) * mm]});
            skFitSpline(sketch, "E575", {"points": [v(-3.91, -5.63) * mm, v(-4, -5.61) * mm, v(-4.1, -5.63) * mm, v(-4.13, -5.68) * mm]});
            skFitSpline(sketch, "E576", {"points": [v(-4.13, -5.68) * mm, v(-4.23, -5.85) * mm, v(-4.3, -5.75) * mm, v(-4.4, -5.27) * mm]});
            skFitSpline(sketch, "E577", {"points": [v(-4.4, -5.27) * mm, v(-4.52, -4.75) * mm, v(-4.9, -3.86) * mm, v(-5.04, -3.77) * mm]});
            skFitSpline(sketch, "E578", {"points": [v(-5.04, -3.77) * mm, v(-5.17, -3.7) * mm, v(-5.99, -4.11) * mm, v(-6.04, -4.3) * mm]});
            skFitSpline(sketch, "E579", {"points": [v(-6.04, -4.3) * mm, v(-6.1, -4.48) * mm, v(-6.62, -5.06) * mm, v(-6.73, -5.06) * mm]});
            skFitSpline(sketch, "E580", {"points": [v(-6.73, -5.06) * mm, v(-6.78, -5.06) * mm, v(-6.94, -5.16) * mm, v(-7.1, -5.29) * mm]});
            skFitSpline(sketch, "E581", {"points": [v(-7.1, -5.29) * mm, v(-7.32, -5.45) * mm, v(-7.46, -5.5) * mm, v(-7.6, -5.48) * mm]});
            skFitSpline(sketch, "E582", {"points": [v(-7.6, -5.48) * mm, v(-7.77, -5.44) * mm, v(-7.76, -5.46) * mm, v(-7.5, -5.71) * mm]});
            skFitSpline(sketch, "E583", {"points": [v(-7.5, -5.71) * mm, v(-7.34, -5.86) * mm, v(-7.23, -6) * mm, v(-7.26, -6.04) * mm]});
            skFitSpline(sketch, "E584", {"points": [v(-7.26, -6.04) * mm, v(-7.29, -6.06) * mm, v(-7.28, -6.08) * mm, v(-7.23, -6.07) * mm]});
            skFitSpline(sketch, "E585", {"points": [v(-7.23, -6.07) * mm, v(-7.07, -6.04) * mm, v(-6.95, -6.08) * mm, v(-6.99, -6.15) * mm]});
            skFitSpline(sketch, "E586", {"points": [v(-6.99, -6.15) * mm, v(-7.02, -6.19) * mm, v(-7, -6.25) * mm, v(-6.94, -6.28) * mm]});
            skFitSpline(sketch, "E587", {"points": [v(-6.94, -6.28) * mm, v(-6.88, -6.31) * mm, v(-6.87, -6.3) * mm, v(-6.91, -6.23) * mm]});
            skFitSpline(sketch, "E588", {"points": [v(-6.91, -6.23) * mm, v(-6.96, -6.16) * mm, v(-6.95, -6.14) * mm, v(-6.87, -6.17) * mm]});
            skFitSpline(sketch, "E589", {"points": [v(-6.87, -6.17) * mm, v(-6.8, -6.2) * mm, v(-6.45, -6.34) * mm, v(-6.08, -6.5) * mm]});
            skFitSpline(sketch, "E590", {"points": [v(-6.08, -6.5) * mm, v(-5.7, -6.65) * mm, v(-5.44, -6.78) * mm, v(-5.48, -6.78) * mm]});
            skFitSpline(sketch, "E591", {"points": [v(-5.48, -6.78) * mm, v(-5.69, -6.79) * mm, v(-4.58, -7.1) * mm, v(-4, -7.2) * mm]});
            skFitSpline(sketch, "E592", {"points": [v(-4, -7.2) * mm, v(-3.3, -7.32) * mm, v(-2.24, -7.3) * mm, v(-1.67, -7.16) * mm]});
            skFitSpline(sketch, "E593", {"points": [v(-5.99, -6.68) * mm, v(-6.07, -6.6) * mm, v(-6.08, -6.61) * mm, v(-6.03, -6.72) * mm]});
            skFitSpline(sketch, "E594", {"points": [v(-6.03, -6.72) * mm, v(-6, -6.8) * mm, v(-5.96, -6.84) * mm, v(-5.94, -6.82) * mm]});
            skFitSpline(sketch, "E595", {"points": [v(-5.94, -6.82) * mm, v(-5.91, -6.8) * mm, v(-5.94, -6.73) * mm, v(-5.99, -6.68) * mm]});
            skFitSpline(sketch, "E596", {"points": [v(-6.16, -6.67) * mm, v(-6.16, -6.65) * mm, v(-6.22, -6.6) * mm, v(-6.3, -6.53) * mm]});
            skFitSpline(sketch, "E597", {"points": [v(-6.3, -6.53) * mm, v(-6.42, -6.44) * mm, v(-6.43, -6.44) * mm, v(-6.33, -6.56) * mm]});
            skFitSpline(sketch, "E598", {"points": [v(-6.33, -6.56) * mm, v(-6.22, -6.7) * mm, v(-6.16, -6.73) * mm, v(-6.16, -6.67) * mm]});
            skFitSpline(sketch, "E599", {"points": [v(7.6, -6.12) * mm, v(7.6, -6.03) * mm, v(7.49, -6.16) * mm, v(7.35, -6.43) * mm]});
            skFitSpline(sketch, "E600", {"points": [v(7.35, -6.43) * mm, v(7.28, -6.55) * mm, v(7.3, -6.54) * mm, v(7.43, -6.4) * mm]});
            skFitSpline(sketch, "E601", {"points": [v(7.43, -6.4) * mm, v(7.52, -6.3) * mm, v(7.6, -6.17) * mm, v(7.6, -6.12) * mm]});
            skFitSpline(sketch, "E602", {"points": [v(7.82, -5.72) * mm, v(7.8, -5.7) * mm, v(7.75, -5.74) * mm, v(7.72, -5.82) * mm]});
            skFitSpline(sketch, "E603", {"points": [v(7.72, -5.82) * mm, v(7.67, -5.93) * mm, v(7.68, -5.94) * mm, v(7.76, -5.86) * mm]});
            skFitSpline(sketch, "E604", {"points": [v(7.76, -5.86) * mm, v(7.82, -5.8) * mm, v(7.84, -5.74) * mm, v(7.82, -5.72) * mm]});
            skFitSpline(sketch, "E605", {"points": [v(-1.39, -5.7) * mm, v(-1.39, -5.56) * mm, v(-1.61, -5.06) * mm, v(-1.8, -4.77) * mm]});
            skFitSpline(sketch, "E606", {"points": [v(-1.74, -4.32) * mm, v(-1.58, -4.25) * mm, v(-1.42, -4.2) * mm, v(-1.38, -4.2) * mm]});
            skFitSpline(sketch, "E607", {"points": [v(-1.38, -4.2) * mm, v(-1.19, -4.2) * mm, v(-1.35, -4.02) * mm, v(-1.71, -3.84) * mm]});
            skFitSpline(sketch, "E608", {"points": [v(-1.71, -3.84) * mm, v(-2.03, -3.68) * mm, v(-2.1, -3.62) * mm, v(-2.03, -3.54) * mm]});
            skFitSpline(sketch, "E609", {"points": [v(-2.03, -3.54) * mm, v(-1.96, -3.46) * mm, v(-2.02, -3.39) * mm, v(-2.3, -3.23) * mm]});
            skFitSpline(sketch, "E610", {"points": [v(-2.3, -3.23) * mm, v(-2.64, -3.03) * mm, v(-2.67, -3.03) * mm, v(-2.85, -3.15) * mm]});
            skFitSpline(sketch, "E611", {"points": [v(-2.85, -3.15) * mm, v(-2.96, -3.21) * mm, v(-3.21, -3.3) * mm, v(-3.4, -3.32) * mm]});
            skFitSpline(sketch, "E612", {"points": [v(-3.51, -3.7) * mm, v(-3.21, -4.09) * mm, v(-3.02, -4.16) * mm, v(-2.74, -3.99) * mm]});
            skFitSpline(sketch, "E613", {"points": [v(-2.67, -4.42) * mm, v(-2.54, -4.51) * mm, v(-2.36, -4.59) * mm, v(-2.26, -4.59) * mm]});
            skFitSpline(sketch, "E614", {"points": [v(-2.26, -4.59) * mm, v(-2.12, -4.59) * mm, v(-2.1, -4.61) * mm, v(-2.17, -4.68) * mm]});
            skFitSpline(sketch, "E615", {"points": [v(-2.17, -4.68) * mm, v(-2.24, -4.75) * mm, v(-2.3, -4.75) * mm, v(-2.47, -4.68) * mm]});
            skFitSpline(sketch, "E616", {"points": [v(-2.47, -4.68) * mm, v(-2.65, -4.6) * mm, v(-2.67, -4.6) * mm, v(-2.63, -4.71) * mm]});
            skFitSpline(sketch, "E617", {"points": [v(-2.63, -4.71) * mm, v(-2.6, -4.78) * mm, v(-2.58, -4.97) * mm, v(-2.58, -5.14) * mm]});
            skFitSpline(sketch, "E618", {"points": [v(-2.58, -5.14) * mm, v(-2.58, -5.36) * mm, v(-2.55, -5.43) * mm, v(-2.47, -5.4) * mm]});
            skFitSpline(sketch, "E619", {"points": [v(-2.47, -5.4) * mm, v(-2.42, -5.38) * mm, v(-2.17, -5.45) * mm, v(-1.94, -5.56) * mm]});
            skFitSpline(sketch, "E620", {"points": [v(-1.94, -5.56) * mm, v(-1.47, -5.77) * mm, v(-1.39, -5.79) * mm, v(-1.39, -5.7) * mm]});
            skFitSpline(sketch, "E621", {"points": [v(-2.7, -5.24) * mm, v(-2.71, -4.91) * mm, v(-2.93, -4.35) * mm, v(-3.05, -4.35) * mm]});
            skFitSpline(sketch, "E622", {"points": [v(-3.05, -4.35) * mm, v(-3.15, -4.35) * mm, v(-3.67, -3.83) * mm, v(-3.83, -3.56) * mm]});
            skFitSpline(sketch, "E623", {"points": [v(-3.83, -3.56) * mm, v(-3.94, -3.39) * mm, v(-4.02, -3.34) * mm, v(-4.23, -3.34) * mm]});
            skFitSpline(sketch, "E624", {"points": [v(-4.23, -3.34) * mm, v(-4.41, -3.34) * mm, v(-4.49, -3.3) * mm, v(-4.49, -3.22) * mm]});
            skFitSpline(sketch, "E625", {"points": [v(-4.49, -3.22) * mm, v(-4.49, -3.13) * mm, v(-4.55, -3.1) * mm, v(-4.67, -3.12) * mm]});
            skFitSpline(sketch, "E626", {"points": [v(-4.67, -3.12) * mm, v(-4.9, -3.15) * mm, v(-5.09, -3.39) * mm, v(-4.98, -3.52) * mm]});
            skFitSpline(sketch, "E627", {"points": [v(-4.98, -3.52) * mm, v(-4.94, -3.57) * mm, v(-4.78, -3.82) * mm, v(-4.64, -4.08) * mm]});
            skFitSpline(sketch, "E628", {"points": [v(-4.64, -4.08) * mm, v(-4.44, -4.44) * mm, v(-3.98, -5.15) * mm, v(-3.81, -5.35) * mm]});
            skFitSpline(sketch, "E629", {"points": [v(-3.81, -5.35) * mm, v(-3.8, -5.37) * mm, v(-3.72, -5.25) * mm, v(-3.62, -5.1) * mm]});
            skFitSpline(sketch, "E630", {"points": [v(-3.62, -5.1) * mm, v(-3.46, -4.81) * mm, v(-3.45, -4.8) * mm, v(-3.3, -4.94) * mm]});
            skFitSpline(sketch, "E631", {"points": [v(-3.3, -4.94) * mm, v(-3.2, -5.02) * mm, v(-3.14, -5.13) * mm, v(-3.14, -5.19) * mm]});
            skFitSpline(sketch, "E632", {"points": [v(-3.14, -5.19) * mm, v(-3.14, -5.25) * mm, v(-3.08, -5.3) * mm, v(-3.02, -5.3) * mm]});
            skFitSpline(sketch, "E633", {"points": [v(-3.02, -5.3) * mm, v(-2.95, -5.3) * mm, v(-2.9, -5.36) * mm, v(-2.9, -5.46) * mm]});
            skFitSpline(sketch, "E634", {"points": [v(-2.9, -5.46) * mm, v(-2.9, -5.55) * mm, v(-2.86, -5.6) * mm, v(-2.8, -5.58) * mm]});
            skFitSpline(sketch, "E635", {"points": [v(-2.8, -5.58) * mm, v(-2.74, -5.56) * mm, v(-2.7, -5.42) * mm, v(-2.7, -5.24) * mm]});
            skFitSpline(sketch, "E636", {"points": [v(-3.89, -4.8) * mm, v(-3.96, -4.56) * mm, v(-4, -3.57) * mm, v(-3.94, -3.57) * mm]});
            skFitSpline(sketch, "E637", {"points": [v(-3.94, -3.57) * mm, v(-3.86, -3.57) * mm, v(-3.73, -4.5) * mm, v(-3.8, -4.57) * mm]});
            skFitSpline(sketch, "E638", {"points": [v(-3.8, -4.57) * mm, v(-3.83, -4.59) * mm, v(-3.81, -4.68) * mm, v(-3.77, -4.76) * mm]});
            skFitSpline(sketch, "E639", {"points": [v(-3.77, -4.76) * mm, v(-3.71, -4.86) * mm, v(-3.72, -4.9) * mm, v(-3.77, -4.9) * mm]});
            skFitSpline(sketch, "E640", {"points": [v(-3.77, -4.9) * mm, v(-3.82, -4.9) * mm, v(-3.87, -4.86) * mm, v(-3.89, -4.8) * mm]});
            skFitSpline(sketch, "E641", {"points": [v(-3.22, -5.34) * mm, v(-3.22, -5.32) * mm, v(-3.25, -5.28) * mm, v(-3.3, -5.25) * mm]});
            skFitSpline(sketch, "E642", {"points": [v(-3.3, -5.25) * mm, v(-3.34, -5.23) * mm, v(-3.38, -5.24) * mm, v(-3.38, -5.29) * mm]});
            skFitSpline(sketch, "E643", {"points": [v(-3.38, -5.29) * mm, v(-3.38, -5.33) * mm, v(-3.34, -5.37) * mm, v(-3.3, -5.37) * mm]});
            skFitSpline(sketch, "E644", {"points": [v(-3.3, -5.37) * mm, v(-3.25, -5.37) * mm, v(-3.22, -5.36) * mm, v(-3.22, -5.34) * mm]});
            skFitSpline(sketch, "E645", {"points": [v(-4.2, -5.09) * mm, v(-4.23, -5.02) * mm, v(-4.27, -4.98) * mm, v(-4.3, -5) * mm]});
            skFitSpline(sketch, "E646", {"points": [v(-4.3, -5) * mm, v(-4.32, -5.02) * mm, v(-4.31, -5.1) * mm, v(-4.28, -5.17) * mm]});
            skFitSpline(sketch, "E647", {"points": [v(-4.28, -5.17) * mm, v(-4.25, -5.24) * mm, v(-4.21, -5.28) * mm, v(-4.2, -5.26) * mm]});
            skFitSpline(sketch, "E648", {"points": [v(-4.2, -5.26) * mm, v(-4.17, -5.24) * mm, v(-4.17, -5.16) * mm, v(-4.2, -5.09) * mm]});
            skFitSpline(sketch, "E649", {"points": [v(2.78, -4.13) * mm, v(3.09, -3.82) * mm, v(3.22, -3.63) * mm, v(3.18, -3.56) * mm]});
            skFitSpline(sketch, "E650", {"points": [v(3.18, -3.56) * mm, v(3.14, -3.5) * mm, v(3.14, -3.48) * mm, v(3.18, -3.5) * mm]});
            skFitSpline(sketch, "E651", {"points": [v(3.18, -3.5) * mm, v(3.25, -3.57) * mm, v(3.46, -3.4) * mm, v(3.41, -3.32) * mm]});
            skFitSpline(sketch, "E652", {"points": [v(3.41, -3.32) * mm, v(3.4, -3.3) * mm, v(3.47, -3.14) * mm, v(3.58, -2.98) * mm]});
            skFitSpline(sketch, "E653", {"points": [v(3.58, -2.98) * mm, v(3.68, -2.83) * mm, v(3.8, -2.57) * mm, v(3.83, -2.41) * mm]});
            skFitSpline(sketch, "E654", {"points": [v(3.83, -2.41) * mm, v(3.86, -2.25) * mm, v(3.93, -1.99) * mm, v(4, -1.81) * mm]});
            skFitSpline(sketch, "E655", {"points": [v(4, -1.81) * mm, v(4.15, -1.4) * mm, v(4.17, -1.28) * mm, v(4.22, -0.17) * mm]});
            skFitSpline(sketch, "E656", {"points": [v(4.22, -0.17) * mm, v(4.28, 0.87) * mm, v(4.18, 1.73) * mm, v(3.94, 2.24) * mm]});
            skFitSpline(sketch, "E657", {"points": [v(3.94, 2.24) * mm, v(3.86, 2.42) * mm, v(3.77, 2.65) * mm, v(3.74, 2.75) * mm]});
            skFitSpline(sketch, "E658", {"points": [v(3.74, 2.75) * mm, v(3.6, 3.17) * mm, v(3.13, 4) * mm, v(2.84, 4.3) * mm]});
            skFitSpline(sketch, "E659", {"points": [v(2.84, 4.3) * mm, v(2.47, 4.69) * mm, v(2.54, 4.73) * mm, v(1.83, 3.68) * mm]});
            skFitSpline(sketch, "E660", {"points": [v(1.83, 3.68) * mm, v(1.72, 3.52) * mm, v(1.63, 3.34) * mm, v(1.63, 3.27) * mm]});
            skFitSpline(sketch, "E661", {"points": [v(1.63, 3.27) * mm, v(1.63, 3.14) * mm, v(1.87, 3) * mm, v(2.08, 3) * mm]});
            skFitSpline(sketch, "E662", {"points": [v(2.08, 3) * mm, v(2.16, 3) * mm, v(2.33, 2.94) * mm, v(2.46, 2.88) * mm]});
            skFitSpline(sketch, "E663", {"points": [v(2.46, 2.88) * mm, v(2.58, 2.81) * mm, v(2.73, 2.76) * mm, v(2.8, 2.76) * mm]});
            skFitSpline(sketch, "E664", {"points": [v(2.8, 2.76) * mm, v(2.95, 2.76) * mm, v(2.93, 2.6) * mm, v(2.76, 2.55) * mm]});
            skFitSpline(sketch, "E665", {"points": [v(2.76, 2.55) * mm, v(2.54, 2.48) * mm, v(1.96, 2.19) * mm, v(1.77, 2.04) * mm]});
            skFitSpline(sketch, "E666", {"points": [v(1.77, 2.04) * mm, v(1.6, 1.91) * mm, v(1.6, 1.91) * mm, v(1.75, 1.75) * mm]});
            skFitSpline(sketch, "E667", {"points": [v(1.75, 1.75) * mm, v(1.84, 1.65) * mm, v(1.9, 1.47) * mm, v(1.9, 1.31) * mm]});
            skFitSpline(sketch, "E668", {"points": [v(1.9, 1.31) * mm, v(1.9, 0.98) * mm, v(1.46, 0.5) * mm, v(0.92, 0.22) * mm]});
            skFitSpline(sketch, "E669", {"points": [v(0.92, 0.22) * mm, v(0.49, 0) * mm, v(0.33, -0.16) * mm, v(0.16, -0.54) * mm]});
            skFitSpline(sketch, "E670", {"points": [v(0.16, -0.54) * mm, v(-0.02, -0.97) * mm, v(0, -1.07) * mm, v(0.33, -1.2) * mm]});
            skFitSpline(sketch, "E671", {"points": [v(0.33, -1.2) * mm, v(0.59, -1.3) * mm, v(0.66, -1.3) * mm, v(1.02, -1.18) * mm]});
            skFitSpline(sketch, "E672", {"points": [v(1.02, -1.18) * mm, v(1.25, -1.11) * mm, v(1.53, -1) * mm, v(1.65, -0.94) * mm]});
            skFitSpline(sketch, "E673", {"points": [v(1.65, -0.94) * mm, v(1.84, -0.84) * mm, v(1.87, -0.84) * mm, v(1.87, -0.94) * mm]});
            skFitSpline(sketch, "E674", {"points": [v(1.87, -0.94) * mm, v(1.87, -1) * mm, v(1.8, -1.13) * mm, v(1.72, -1.24) * mm]});
            skFitSpline(sketch, "E675", {"points": [v(1.72, -1.24) * mm, v(1.46, -1.57) * mm, v(1.13, -2.17) * mm, v(1.19, -2.22) * mm]});
            skFitSpline(sketch, "E676", {"points": [v(1.19, -2.22) * mm, v(1.21, -2.25) * mm, v(1.36, -2.21) * mm, v(1.52, -2.14) * mm]});
            skFitSpline(sketch, "E677", {"points": [v(1.52, -2.14) * mm, v(1.67, -2.07) * mm, v(1.85, -2) * mm, v(1.92, -2) * mm]});
            skFitSpline(sketch, "E678", {"points": [v(1.92, -2) * mm, v(2, -2) * mm, v(2.17, -1.93) * mm, v(2.32, -1.84) * mm]});
            skFitSpline(sketch, "E679", {"points": [v(2.32, -1.84) * mm, v(2.59, -1.68) * mm, v(2.78, -1.7) * mm, v(2.6, -1.86) * mm]});
            skFitSpline(sketch, "E680", {"points": [v(2.6, -1.86) * mm, v(2.56, -1.91) * mm, v(2.53, -2) * mm, v(2.55, -2.04) * mm]});
            skFitSpline(sketch, "E681", {"points": [v(2.55, -2.04) * mm, v(2.57, -2.1) * mm, v(2.48, -2.24) * mm, v(2.34, -2.36) * mm]});
            skFitSpline(sketch, "E682", {"points": [v(2.34, -2.36) * mm, v(2.1, -2.59) * mm, v(2.09, -2.5) * mm, v(2.33, -2.22) * mm]});
            skFitSpline(sketch, "E683", {"points": [v(2.33, -2.22) * mm, v(2.4, -2.14) * mm, v(2.42, -2.09) * mm, v(2.36, -2.09) * mm]});
            skFitSpline(sketch, "E684", {"points": [v(2.36, -2.09) * mm, v(2.22, -2.09) * mm, v(2.02, -2.44) * mm, v(2.07, -2.58) * mm]});
            skFitSpline(sketch, "E685", {"points": [v(2.07, -2.58) * mm, v(2.13, -2.74) * mm, v(2.52, -2.87) * mm, v(2.92, -2.87) * mm]});
            skFitSpline(sketch, "E686", {"points": [v(2.92, -2.87) * mm, v(3.2, -2.87) * mm, v(3.23, -2.89) * mm, v(3.14, -2.99) * mm]});
            skFitSpline(sketch, "E687", {"points": [v(3.14, -2.99) * mm, v(3.09, -3.05) * mm, v(3, -3.1) * mm, v(2.93, -3.1) * mm]});
            skFitSpline(sketch, "E688", {"points": [v(2.93, -3.1) * mm, v(2.87, -3.1) * mm, v(2.83, -3.14) * mm, v(2.84, -3.2) * mm]});
            skFitSpline(sketch, "E689", {"points": [v(2.84, -3.2) * mm, v(2.85, -3.24) * mm, v(2.75, -3.31) * mm, v(2.61, -3.35) * mm]});
            skFitSpline(sketch, "E690", {"points": [v(2.61, -3.35) * mm, v(2.37, -3.41) * mm, v(1.95, -3.81) * mm, v(1.95, -3.97) * mm]});
            skFitSpline(sketch, "E691", {"points": [v(1.95, -3.97) * mm, v(1.95, -4.11) * mm, v(2.18, -4.59) * mm, v(2.25, -4.59) * mm]});
            skFitSpline(sketch, "E692", {"points": [v(2.25, -4.59) * mm, v(2.28, -4.59) * mm, v(2.52, -4.38) * mm, v(2.78, -4.13) * mm]});
            skFitSpline(sketch, "E693", {"points": [v(0.68, -3.73) * mm, v(0.72, -3.73) * mm, v(0.77, -3.76) * mm, v(0.8, -3.8) * mm]});
            skFitSpline(sketch, "E694", {"points": [v(0.8, -3.8) * mm, v(0.82, -3.84) * mm, v(0.9, -3.86) * mm, v(0.96, -3.83) * mm]});
            skFitSpline(sketch, "E695", {"points": [v(0.96, -3.83) * mm, v(1.02, -3.81) * mm, v(1.24, -3.89) * mm, v(1.44, -4) * mm]});
            skFitSpline(sketch, "E696", {"points": [v(1.44, -4) * mm, v(1.77, -4.2) * mm, v(1.8, -4.2) * mm, v(1.76, -4.06) * mm]});
            skFitSpline(sketch, "E697", {"points": [v(1.76, -4.06) * mm, v(1.72, -3.94) * mm, v(1.8, -3.81) * mm, v(2.16, -3.5) * mm]});
            skFitSpline(sketch, "E698", {"points": [v(2.16, -3.5) * mm, v(2.4, -3.28) * mm, v(2.6, -3.08) * mm, v(2.58, -3.07) * mm]});
            skFitSpline(sketch, "E699", {"points": [v(2.58, -3.07) * mm, v(2.56, -3.05) * mm, v(2.41, -2.99) * mm, v(2.25, -2.92) * mm]});
            skFitSpline(sketch, "E700", {"points": [v(2.25, -2.92) * mm, v(1.9, -2.78) * mm, v(1.8, -2.6) * mm, v(1.94, -2.38) * mm]});
            skFitSpline(sketch, "E701", {"points": [v(1.94, -2.38) * mm, v(2, -2.3) * mm, v(2.02, -2.2) * mm, v(2, -2.18) * mm]});
            skFitSpline(sketch, "E702", {"points": [v(2, -2.18) * mm, v(1.93, -2.12) * mm, v(1.33, -2.33) * mm, v(1.22, -2.45) * mm]});
            skFitSpline(sketch, "E703", {"points": [v(1.22, -2.45) * mm, v(1.09, -2.62) * mm, v(0.92, -2.58) * mm, v(0.94, -2.38) * mm]});
            skFitSpline(sketch, "E704", {"points": [v(0.94, -2.38) * mm, v(0.94, -2.28) * mm, v(1.08, -1.98) * mm, v(1.24, -1.72) * mm]});
            skFitSpline(sketch, "E705", {"points": [v(1.24, -1.72) * mm, v(1.59, -1.15) * mm, v(1.55, -1.13) * mm, v(0.84, -1.38) * mm]});
            skFitSpline(sketch, "E706", {"points": [v(0.84, -1.38) * mm, v(0.6, -1.47) * mm, v(0.38, -1.54) * mm, v(0.35, -1.54) * mm]});
            skFitSpline(sketch, "E707", {"points": [v(0.35, -1.54) * mm, v(0.26, -1.54) * mm, v(-0.13, -1.11) * mm, v(-0.2, -0.95) * mm]});
            skFitSpline(sketch, "E708", {"points": [v(-0.2, -0.95) * mm, v(-0.23, -0.87) * mm, v(-0.22, -0.71) * mm, v(-0.18, -0.6) * mm]});
            skFitSpline(sketch, "E709", {"points": [v(-0.18, -0.6) * mm, v(-0.07, -0.32) * mm, v(0.61, 0.34) * mm, v(0.8, 0.34) * mm]});
            skFitSpline(sketch, "E710", {"points": [v(0.8, 0.34) * mm, v(1.04, 0.34) * mm, v(1.62, 0.89) * mm, v(1.68, 1.16) * mm]});
            skFitSpline(sketch, "E711", {"points": [v(1.68, 1.16) * mm, v(1.72, 1.38) * mm, v(1.7, 1.42) * mm, v(1.48, 1.5) * mm]});
            skFitSpline(sketch, "E712", {"points": [v(1.48, 1.5) * mm, v(1.22, 1.61) * mm, v(1.17, 1.7) * mm, v(1.33, 1.77) * mm]});
            skFitSpline(sketch, "E713", {"points": [v(1.33, 1.77) * mm, v(1.45, 1.82) * mm, v(1.13, 1.85) * mm, v(0.84, 1.82) * mm]});
            skFitSpline(sketch, "E714", {"points": [v(0.84, 1.82) * mm, v(0.73, 1.81) * mm, v(0.57, 1.8) * mm, v(0.48, 1.79) * mm]});
            skFitSpline(sketch, "E715", {"points": [v(0.48, 1.79) * mm, v(0.4, 1.78) * mm, v(0.26, 1.8) * mm, v(0.2, 1.83) * mm]});
            skFitSpline(sketch, "E716", {"points": [v(0.2, 1.83) * mm, v(0.1, 1.88) * mm, v(0, 1.83) * mm, v(-0.12, 1.7) * mm]});
            skFitSpline(sketch, "E717", {"points": [v(-0.12, 1.7) * mm, v(-0.3, 1.52) * mm, v(-0.3, 1.5) * mm, v(-0.15, 1.5) * mm]});
            skFitSpline(sketch, "E718", {"points": [v(-0.15, 1.5) * mm, v(-0.05, 1.5) * mm, v(-0.08, 1.47) * mm, v(-0.25, 1.4) * mm]});
            skFitSpline(sketch, "E719", {"points": [v(-0.25, 1.4) * mm, v(-0.53, 1.3) * mm, v(-1.33, 0.6) * mm, v(-1.28, 0.5) * mm]});
            skFitSpline(sketch, "E720", {"points": [v(-1.28, 0.5) * mm, v(-1.26, 0.47) * mm, v(-1.06, 0.4) * mm, v(-0.84, 0.34) * mm]});
            skFitSpline(sketch, "E721", {"points": [v(-0.84, 0.34) * mm, v(-0.62, 0.28) * mm, v(-0.44, 0.2) * mm, v(-0.44, 0.17) * mm]});
            skFitSpline(sketch, "E722", {"points": [v(-0.44, 0.17) * mm, v(-0.44, 0.07) * mm, v(0.02, 0.09) * mm, v(0.23, 0.19) * mm]});
            skFitSpline(sketch, "E723", {"points": [v(0.23, 0.19) * mm, v(0.37, 0.26) * mm, v(0.37, 0.25) * mm, v(0.2, 0.1) * mm]});
            skFitSpline(sketch, "E724", {"points": [v(0.2, 0.1) * mm, v(-0.05, -0.1) * mm, v(-0.17, -0.1) * mm, v(-0.7, 0.1) * mm]});
            skFitSpline(sketch, "E725", {"points": [v(-0.7, 0.1) * mm, v(-0.96, 0.21) * mm, v(-1.2, 0.26) * mm, v(-1.37, 0.23) * mm]});
            skFitSpline(sketch, "E726", {"points": [v(-1.37, 0.23) * mm, v(-1.51, 0.2) * mm, v(-1.63, 0.22) * mm, v(-1.63, 0.26) * mm]});
            skFitSpline(sketch, "E727", {"points": [v(-1.63, 0.26) * mm, v(-1.63, 0.4) * mm, v(-1.77, 0.34) * mm, v(-2.13, 0.02) * mm]});
            skFitSpline(sketch, "E728", {"points": [v(-2.13, 0.02) * mm, v(-2.33, -0.16) * mm, v(-2.53, -0.28) * mm, v(-2.57, -0.26) * mm]});
            skFitSpline(sketch, "E729", {"points": [v(-2.57, -0.26) * mm, v(-2.6, -0.23) * mm, v(-2.7, -0.29) * mm, v(-2.79, -0.38) * mm]});
            skFitSpline(sketch, "E730", {"points": [v(-2.79, -0.38) * mm, v(-2.93, -0.53) * mm, v(-2.93, -0.54) * mm, v(-2.79, -0.64) * mm]});
            skFitSpline(sketch, "E731", {"points": [v(-2.79, -0.64) * mm, v(-2.58, -0.8) * mm, v(-2.02, -0.86) * mm, v(-1.76, -0.76) * mm]});
            skFitSpline(sketch, "E732", {"points": [v(-1.76, -0.76) * mm, v(-1.63, -0.71) * mm, v(-1.56, -0.7) * mm, v(-1.59, -0.76) * mm]});
            skFitSpline(sketch, "E733", {"points": [v(-1.59, -0.76) * mm, v(-1.62, -0.8) * mm, v(-1.58, -0.81) * mm, v(-1.51, -0.79) * mm]});
            skFitSpline(sketch, "E734", {"points": [v(-1.51, -0.79) * mm, v(-1.45, -0.76) * mm, v(-1.4, -0.71) * mm, v(-1.43, -0.68) * mm]});
            skFitSpline(sketch, "E735", {"points": [v(-1.43, -0.68) * mm, v(-1.45, -0.65) * mm, v(-1.39, -0.56) * mm, v(-1.29, -0.48) * mm]});
            skFitSpline(sketch, "E736", {"points": [v(-1.2, -0.66) * mm, v(-0.37, -0.5) * mm, v(-0.33, -0.5) * mm, v(-0.39, -0.6) * mm]});
            skFitSpline(sketch, "E737", {"points": [v(-0.39, -0.6) * mm, v(-0.42, -0.64) * mm, v(-0.54, -0.68) * mm, v(-0.66, -0.68) * mm]});
            skFitSpline(sketch, "E738", {"points": [v(-0.66, -0.68) * mm, v(-0.86, -0.68) * mm, v(-1.55, -0.94) * mm, v(-1.55, -1.02) * mm]});
            skFitSpline(sketch, "E739", {"points": [v(-1.55, -1.02) * mm, v(-1.55, -1.06) * mm, v(-0.93, -0.93) * mm, v(-0.8, -0.87) * mm]});
            skFitSpline(sketch, "E740", {"points": [v(-0.8, -0.87) * mm, v(-0.75, -0.84) * mm, v(-0.8, -0.9) * mm, v(-0.91, -0.98) * mm]});
            skFitSpline(sketch, "E741", {"points": [v(-0.91, -0.98) * mm, v(-1.02, -1.07) * mm, v(-1.26, -1.2) * mm, v(-1.45, -1.28) * mm]});
            skFitSpline(sketch, "E742", {"points": [v(-1.45, -1.28) * mm, v(-1.63, -1.36) * mm, v(-1.79, -1.45) * mm, v(-1.79, -1.48) * mm]});
            skFitSpline(sketch, "E743", {"points": [v(-1.79, -1.48) * mm, v(-1.79, -1.52) * mm, v(-1.63, -1.62) * mm, v(-1.45, -1.7) * mm]});
            skFitSpline(sketch, "E744", {"points": [v(-1.45, -1.7) * mm, v(-1.11, -1.85) * mm, v(-1.11, -1.85) * mm, v(-1.36, -1.85) * mm]});
            skFitSpline(sketch, "E745", {"points": [v(-1.36, -1.85) * mm, v(-1.5, -1.85) * mm, v(-1.7, -1.78) * mm, v(-1.8, -1.7) * mm]});
            skFitSpline(sketch, "E746", {"points": [v(-1.8, -1.7) * mm, v(-1.92, -1.61) * mm, v(-2.05, -1.54) * mm, v(-2.1, -1.54) * mm]});
            skFitSpline(sketch, "E747", {"points": [v(-2.1, -1.54) * mm, v(-2.26, -1.54) * mm, v(-2.61, -1.8) * mm, v(-2.96, -2.15) * mm]});
            skFitSpline(sketch, "E748", {"points": [v(-3.09, -2.6) * mm, v(-2.97, -2.67) * mm, v(-2.8, -2.71) * mm, v(-2.69, -2.71) * mm]});
            skFitSpline(sketch, "E749", {"points": [v(-2.69, -2.71) * mm, v(-2.52, -2.71) * mm, v(-2.5, -2.7) * mm, v(-2.6, -2.6) * mm]});
            skFitSpline(sketch, "E750", {"points": [v(-2.6, -2.6) * mm, v(-2.66, -2.54) * mm, v(-2.8, -2.48) * mm, v(-2.9, -2.46) * mm]});
            skFitSpline(sketch, "E751", {"points": [v(-2.9, -2.46) * mm, v(-3.01, -2.44) * mm, v(-2.69, -2.42) * mm, v(-2.18, -2.42) * mm]});
            skFitSpline(sketch, "E752", {"points": [v(-2.18, -2.42) * mm, v(-0.71, -2.42) * mm, v(-0.76, -2.42) * mm, v(-0.66, -2.2) * mm]});
            skFitSpline(sketch, "E753", {"points": [v(-0.66, -2.2) * mm, v(-0.6, -2.06) * mm, v(-0.5, -2) * mm, v(-0.34, -2) * mm]});
            skFitSpline(sketch, "E754", {"points": [v(-0.34, -2) * mm, v(-0.22, -2) * mm, v(0.01, -1.96) * mm, v(0.17, -1.9) * mm]});
            skFitSpline(sketch, "E755", {"points": [v(0.17, -1.9) * mm, v(0.32, -1.83) * mm, v(0.42, -1.81) * mm, v(0.4, -1.86) * mm]});
            skFitSpline(sketch, "E756", {"points": [v(0.4, -1.86) * mm, v(0.33, -1.96) * mm, v(-0.2, -2.17) * mm, v(-0.27, -2.13) * mm]});
            skFitSpline(sketch, "E757", {"points": [v(-0.27, -2.13) * mm, v(-0.34, -2.09) * mm, v(-0.67, -2.3) * mm, v(-0.67, -2.4) * mm]});
            skFitSpline(sketch, "E758", {"points": [v(-0.67, -2.4) * mm, v(-0.67, -2.43) * mm, v(-0.53, -2.49) * mm, v(-0.35, -2.52) * mm]});
            skFitSpline(sketch, "E759", {"points": [v(-0.35, -2.52) * mm, v(-0.16, -2.55) * mm, v(-0.05, -2.6) * mm, v(-0.1, -2.64) * mm]});
            skFitSpline(sketch, "E760", {"points": [v(-0.1, -2.64) * mm, v(-0.13, -2.68) * mm, v(-0.28, -2.68) * mm, v(-0.44, -2.63) * mm]});
            skFitSpline(sketch, "E761", {"points": [v(-0.44, -2.63) * mm, v(-0.77, -2.54) * mm, v(-1.3, -2.53) * mm, v(-1.3, -2.62) * mm]});
            skFitSpline(sketch, "E762", {"points": [v(-1.3, -2.62) * mm, v(-1.3, -2.73) * mm, v(-1.02, -2.95) * mm, v(-0.78, -3.02) * mm]});
            skFitSpline(sketch, "E763", {"points": [v(-0.78, -3.02) * mm, v(-0.58, -3.08) * mm, v(-0.57, -3.1) * mm, v(-0.74, -3.1) * mm]});
            skFitSpline(sketch, "E764", {"points": [v(-0.74, -3.1) * mm, v(-0.94, -3.1) * mm, v(-1.39, -2.88) * mm, v(-1.39, -2.77) * mm]});
            skFitSpline(sketch, "E765", {"points": [v(-1.39, -2.77) * mm, v(-1.39, -2.7) * mm, v(-1.87, -2.74) * mm, v(-2.33, -2.84) * mm]});
            skFitSpline(sketch, "E766", {"points": [v(-2.33, -2.84) * mm, v(-2.5, -2.87) * mm, v(-2.46, -2.9) * mm, v(-2.04, -3.18) * mm]});
            skFitSpline(sketch, "E767", {"points": [v(-2.04, -3.18) * mm, v(-1.64, -3.44) * mm, v(-1.5, -3.5) * mm, v(-1.16, -3.5) * mm]});
            skFitSpline(sketch, "E768", {"points": [v(-1.16, -3.5) * mm, v(-0.77, -3.5) * mm, v(-0.44, -3.6) * mm, v(-0.2, -3.78) * mm]});
            skFitSpline(sketch, "E769", {"points": [v(-0.2, -3.78) * mm, v(-0.13, -3.84) * mm, v(0.07, -3.98) * mm, v(0.24, -4.1) * mm]});
            skFitSpline(sketch, "E770", {"points": [v(0.58, -4.03) * mm, v(0.6, -3.86) * mm, v(0.64, -3.73) * mm, v(0.68, -3.73) * mm]});
            skFitSpline(sketch, "E771", {"points": [v(1.07, -3.02) * mm, v(0.83, -2.94) * mm, v(0.56, -2.83) * mm, v(0.46, -2.78) * mm]});
            skFitSpline(sketch, "E772", {"points": [v(0.46, -2.78) * mm, v(0.31, -2.7) * mm, v(0.25, -2.71) * mm, v(0.14, -2.82) * mm]});
            skFitSpline(sketch, "E773", {"points": [v(0.14, -2.82) * mm, v(-0.08, -3) * mm, v(-0.14, -2.98) * mm, v(0, -2.75) * mm]});
            skFitSpline(sketch, "E774", {"points": [v(0, -2.75) * mm, v(0.15, -2.53) * mm, v(0.33, -2.5) * mm, v(0.51, -2.66) * mm]});
            skFitSpline(sketch, "E775", {"points": [v(0.51, -2.66) * mm, v(0.58, -2.72) * mm, v(0.86, -2.85) * mm, v(1.13, -2.95) * mm]});
            skFitSpline(sketch, "E776", {"points": [v(1.13, -2.95) * mm, v(1.4, -3.05) * mm, v(1.63, -3.14) * mm, v(1.63, -3.15) * mm]});
            skFitSpline(sketch, "E777", {"points": [v(1.63, -3.15) * mm, v(1.63, -3.2) * mm, v(1.53, -3.18) * mm, v(1.07, -3.02) * mm]});
            skFitSpline(sketch, "E778", {"points": [v(0.04, 1.38) * mm, v(0.04, 1.46) * mm, v(0.16, 1.5) * mm, v(0.44, 1.52) * mm]});
            skFitSpline(sketch, "E779", {"points": [v(0.44, 1.52) * mm, v(0.66, 1.54) * mm, v(0.84, 1.54) * mm, v(0.84, 1.53) * mm]});
            skFitSpline(sketch, "E780", {"points": [v(0.84, 1.53) * mm, v(0.84, 1.52) * mm, v(0.73, 1.46) * mm, v(0.6, 1.4) * mm]});
            skFitSpline(sketch, "E781", {"points": [v(0.6, 1.4) * mm, v(0.3, 1.25) * mm, v(0.04, 1.24) * mm, v(0.04, 1.38) * mm]});
            skFitSpline(sketch, "E782", {"points": [v(0.38, 1.4) * mm, v(0.32, 1.43) * mm, v(0.24, 1.43) * mm, v(0.18, 1.4) * mm]});
            skFitSpline(sketch, "E783", {"points": [v(0.18, 1.4) * mm, v(0.13, 1.38) * mm, v(0.17, 1.37) * mm, v(0.28, 1.37) * mm]});
            skFitSpline(sketch, "E784", {"points": [v(0.28, 1.37) * mm, v(0.39, 1.37) * mm, v(0.43, 1.38) * mm, v(0.38, 1.4) * mm]});
            skFitSpline(sketch, "E785", {"points": [v(-1.47, -3.78) * mm, v(-1.47, -3.76) * mm, v(-1.52, -3.72) * mm, v(-1.6, -3.7) * mm]});
            skFitSpline(sketch, "E786", {"points": [v(-1.6, -3.7) * mm, v(-1.66, -3.67) * mm, v(-1.7, -3.69) * mm, v(-1.67, -3.73) * mm]});
            skFitSpline(sketch, "E787", {"points": [v(-1.67, -3.73) * mm, v(-1.62, -3.8) * mm, v(-1.47, -3.84) * mm, v(-1.47, -3.78) * mm]});
            skFitSpline(sketch, "E788", {"points": [v(-5.01, -3.08) * mm, v(-4.95, -2.92) * mm, v(-4.97, -2.75) * mm, v(-5.08, -2.43) * mm]});
            skFitSpline(sketch, "E789", {"points": [v(-5.08, -2.43) * mm, v(-5.24, -1.98) * mm, v(-5.59, -1.6) * mm, v(-6.03, -1.42) * mm]});
            skFitSpline(sketch, "E790", {"points": [v(-6.03, -1.42) * mm, v(-6.3, -1.3) * mm, v(-6.55, -1.06) * mm, v(-6.7, -0.77) * mm]});
            skFitSpline(sketch, "E791", {"points": [v(-6.7, -0.77) * mm, v(-6.8, -0.61) * mm, v(-6.84, -0.6) * mm, v(-7.16, -0.65) * mm]});
            skFitSpline(sketch, "E792", {"points": [v(-7.16, -0.65) * mm, v(-7.4, -0.68) * mm, v(-7.59, -0.66) * mm, v(-7.71, -0.6) * mm]});
            skFitSpline(sketch, "E793", {"points": [v(-7.71, -0.6) * mm, v(-7.86, -0.52) * mm, v(-7.97, -0.52) * mm, v(-8.25, -0.6) * mm]});
            skFitSpline(sketch, "E794", {"points": [v(-8.25, -0.6) * mm, v(-8.45, -0.65) * mm, v(-8.68, -0.67) * mm, v(-8.77, -0.64) * mm]});
            skFitSpline(sketch, "E795", {"points": [v(-8.77, -0.64) * mm, v(-9.08, -0.55) * mm, v(-8.95, -0.72) * mm, v(-8.5, -1) * mm]});
            skFitSpline(sketch, "E796", {"points": [v(-8.5, -1) * mm, v(-8.26, -1.14) * mm, v(-7.94, -1.35) * mm, v(-7.78, -1.44) * mm]});
            skFitSpline(sketch, "E797", {"points": [v(-7.78, -1.44) * mm, v(-7.63, -1.54) * mm, v(-7.45, -1.62) * mm, v(-7.4, -1.62) * mm]});
            skFitSpline(sketch, "E798", {"points": [v(-7.4, -1.62) * mm, v(-7.18, -1.62) * mm, v(-7.18, -1.78) * mm, v(-7.4, -2) * mm]});
            skFitSpline(sketch, "E799", {"points": [v(-7.15, -2.23) * mm, v(-6.47, -2.25) * mm, v(-5.86, -2.49) * mm, v(-5.54, -2.84) * mm]});
            skFitSpline(sketch, "E800", {"points": [v(-5.54, -2.84) * mm, v(-5.4, -3) * mm, v(-5.28, -3.18) * mm, v(-5.28, -3.24) * mm]});
            skFitSpline(sketch, "E801", {"points": [v(-5.28, -3.24) * mm, v(-5.28, -3.42) * mm, v(-5.1, -3.3) * mm, v(-5.01, -3.08) * mm]});
            skFitSpline(sketch, "E802", {"points": [v(-5.6, -3.11) * mm, v(-5.6, -3.03) * mm, v(-5.65, -2.95) * mm, v(-5.71, -2.92) * mm]});
            skFitSpline(sketch, "E803", {"points": [v(-5.71, -2.92) * mm, v(-5.8, -2.89) * mm, v(-5.8, -2.92) * mm, v(-5.73, -3.07) * mm]});
            skFitSpline(sketch, "E804", {"points": [v(-5.73, -3.07) * mm, v(-5.62, -3.3) * mm, v(-5.6, -3.3) * mm, v(-5.6, -3.11) * mm]});
            skFitSpline(sketch, "E805", {"points": [v(-3.12, -3.1) * mm, v(-2.42, -2.9) * mm, v(-3.26, -2.7) * mm, v(-4.2, -2.84) * mm]});
            skFitSpline(sketch, "E806", {"points": [v(-4.2, -2.84) * mm, v(-4.54, -2.9) * mm, v(-4.6, -3.03) * mm, v(-4.26, -3.03) * mm]});
            skFitSpline(sketch, "E807", {"points": [v(-4.26, -3.03) * mm, v(-4.13, -3.03) * mm, v(-4, -3.06) * mm, v(-3.97, -3.1) * mm]});
            skFitSpline(sketch, "E808", {"points": [v(-3.97, -3.1) * mm, v(-3.9, -3.2) * mm, v(-3.5, -3.2) * mm, v(-3.12, -3.1) * mm]});
            skFitSpline(sketch, "E809", {"points": [v(-3.37, -2.26) * mm, v(-3.18, -2.1) * mm, v(-2.86, -1.84) * mm, v(-2.66, -1.7) * mm]});
            skFitSpline(sketch, "E810", {"points": [v(-2.66, -1.7) * mm, v(-2.46, -1.55) * mm, v(-2.3, -1.4) * mm, v(-2.28, -1.36) * mm]});
            skFitSpline(sketch, "E811", {"points": [v(-2.28, -1.36) * mm, v(-2.26, -1.33) * mm, v(-2.14, -1.3) * mm, v(-2, -1.3) * mm]});
            skFitSpline(sketch, "E812", {"points": [v(-2, -1.3) * mm, v(-1.76, -1.3) * mm, v(-1.76, -1.3) * mm, v(-1.93, -1.2) * mm]});
            skFitSpline(sketch, "E813", {"points": [v(-1.93, -1.2) * mm, v(-2.02, -1.16) * mm, v(-2.1, -1.1) * mm, v(-2.1, -1.05) * mm]});
            skFitSpline(sketch, "E814", {"points": [v(-2.1, -1.05) * mm, v(-2.1, -1.01) * mm, v(-2.17, -1) * mm, v(-2.25, -1.03) * mm]});
            skFitSpline(sketch, "E815", {"points": [v(-2.25, -1.03) * mm, v(-2.33, -1.05) * mm, v(-2.5, -1.02) * mm, v(-2.65, -0.95) * mm]});
            skFitSpline(sketch, "E816", {"points": [v(-2.65, -0.95) * mm, v(-2.98, -0.79) * mm, v(-3.07, -0.83) * mm, v(-3.39, -1.28) * mm]});
            skFitSpline(sketch, "E817", {"points": [v(-3.39, -1.28) * mm, v(-3.53, -1.49) * mm, v(-3.8, -1.84) * mm, v(-3.99, -2.07) * mm]});
            skFitSpline(sketch, "E818", {"points": [v(-3.99, -2.07) * mm, v(-4.18, -2.3) * mm, v(-4.33, -2.5) * mm, v(-4.33, -2.52) * mm]});
            skFitSpline(sketch, "E819", {"points": [v(-4.33, -2.52) * mm, v(-4.33, -2.54) * mm, v(-4.2, -2.56) * mm, v(-4.02, -2.56) * mm]});
            skFitSpline(sketch, "E820", {"points": [v(-4.02, -2.56) * mm, v(-3.78, -2.56) * mm, v(-3.64, -2.5) * mm, v(-3.37, -2.26) * mm]});
            skFitSpline(sketch, "E821", {"points": [v(-7.23, -2.4) * mm, v(-7.1, -2.35) * mm, v(-7.15, -2.33) * mm, v(-7.4, -2.33) * mm]});
            skFitSpline(sketch, "E822", {"points": [v(-7.4, -2.33) * mm, v(-7.59, -2.32) * mm, v(-7.76, -2.36) * mm, v(-7.79, -2.4) * mm]});
            skFitSpline(sketch, "E823", {"points": [v(-7.79, -2.4) * mm, v(-7.85, -2.5) * mm, v(-7.46, -2.5) * mm, v(-7.23, -2.4) * mm]});
            skFitSpline(sketch, "E824", {"points": [v(-4.3, -2.09) * mm, v(-4, -1.72) * mm, v(-3.52, -0.97) * mm, v(-3.43, -0.74) * mm]});
            skFitSpline(sketch, "E825", {"points": [v(-3.43, -0.74) * mm, v(-3.4, -0.65) * mm, v(-3.46, -0.52) * mm, v(-3.6, -0.36) * mm]});
            skFitSpline(sketch, "E826", {"points": [v(-3.6, -0.36) * mm, v(-3.82, -0.1) * mm, v(-3.84, 0.14) * mm, v(-3.7, 0.88) * mm]});
            skFitSpline(sketch, "E827", {"points": [v(-3.7, 0.88) * mm, v(-3.59, 1.43) * mm, v(-3.46, 1.57) * mm, v(-3.52, 1.07) * mm]});
            skFitSpline(sketch, "E828", {"points": [v(-3.52, 1.07) * mm, v(-3.54, 0.83) * mm, v(-3.53, 0.72) * mm, v(-3.48, 0.75) * mm]});
            skFitSpline(sketch, "E829", {"points": [v(-3.48, 0.75) * mm, v(-3.43, 0.79) * mm, v(-3.4, 0.69) * mm, v(-3.43, 0.47) * mm]});
            skFitSpline(sketch, "E830", {"points": [v(-3.43, 0.47) * mm, v(-3.45, 0.27) * mm, v(-3.42, 0.03) * mm, v(-3.34, -0.16) * mm]});
            skFitSpline(sketch, "E831", {"points": [v(-2.8, -0.12) * mm, v(-2.57, 0.06) * mm, v(-2.37, 0.22) * mm, v(-2.35, 0.24) * mm]});
            skFitSpline(sketch, "E832", {"points": [v(-2.35, 0.24) * mm, v(-2.33, 0.25) * mm, v(-2.32, 0.63) * mm, v(-2.33, 1.08) * mm]});
            skFitSpline(sketch, "E833", {"points": [v(-2.33, 1.08) * mm, v(-2.35, 1.95) * mm, v(-2.3, 2.15) * mm, v(-2, 2.3) * mm]});
            skFitSpline(sketch, "E834", {"points": [v(-2, 2.3) * mm, v(-1.83, 2.39) * mm, v(-1.83, 2.39) * mm, v(-2.02, 2.19) * mm]});
            skFitSpline(sketch, "E835", {"points": [v(-2.02, 2.19) * mm, v(-2.17, 2.03) * mm, v(-2.2, 1.9) * mm, v(-2.2, 1.63) * mm]});
            skFitSpline(sketch, "E836", {"points": [v(-2.2, 1.63) * mm, v(-2.19, 1.44) * mm, v(-2.15, 1.2) * mm, v(-2.1, 1.08) * mm]});
            skFitSpline(sketch, "E837", {"points": [v(-2.1, 1.08) * mm, v(-2.06, 0.97) * mm, v(-2.05, 0.77) * mm, v(-2.07, 0.63) * mm]});
            skFitSpline(sketch, "E838", {"points": [v(-2.07, 0.63) * mm, v(-2.1, 0.45) * mm, v(-2.1, 0.4) * mm, v(-2.04, 0.48) * mm]});
            skFitSpline(sketch, "E839", {"points": [v(-2.04, 0.48) * mm, v(-2, 0.55) * mm, v(-1.92, 0.57) * mm, v(-1.86, 0.53) * mm]});
            skFitSpline(sketch, "E840", {"points": [v(-1.86, 0.53) * mm, v(-1.8, 0.5) * mm, v(-1.77, 0.5) * mm, v(-1.8, 0.53) * mm]});
            skFitSpline(sketch, "E841", {"points": [v(-1.8, 0.53) * mm, v(-1.84, 0.57) * mm, v(-1.82, 0.65) * mm, v(-1.77, 0.7) * mm]});
            skFitSpline(sketch, "E842", {"points": [v(-1.77, 0.7) * mm, v(-1.65, 0.85) * mm, v(-1.63, 0.94) * mm, v(-1.6, 1.64) * mm]});
            skFitSpline(sketch, "E843", {"points": [v(-1.6, 1.64) * mm, v(-1.58, 2.23) * mm, v(-1.47, 2.45) * mm, v(-1.11, 2.62) * mm]});
            skFitSpline(sketch, "E844", {"points": [v(-1.11, 2.62) * mm, v(-0.97, 2.68) * mm, v(-0.97, 2.68) * mm, v(-1.13, 2.55) * mm]});
            skFitSpline(sketch, "E845", {"points": [v(-1.13, 2.55) * mm, v(-1.37, 2.35) * mm, v(-1.48, 2.03) * mm, v(-1.39, 1.78) * mm]});
            skFitSpline(sketch, "E846", {"points": [v(-1.39, 1.78) * mm, v(-1.34, 1.67) * mm, v(-1.3, 1.47) * mm, v(-1.3, 1.35) * mm]});
            skFitSpline(sketch, "E847", {"points": [v(-1.3, 1.35) * mm, v(-1.3, 1.05) * mm, v(-1.24, 1.06) * mm, v(-0.92, 1.39) * mm]});
            skFitSpline(sketch, "E848", {"points": [v(-0.92, 1.39) * mm, v(-0.7, 1.62) * mm, v(-0.65, 1.73) * mm, v(-0.6, 2.17) * mm]});
            skFitSpline(sketch, "E849", {"points": [v(-0.6, 2.17) * mm, v(-0.57, 2.5) * mm, v(-0.5, 2.73) * mm, v(-0.4, 2.82) * mm]});
            skFitSpline(sketch, "E850", {"points": [v(-0.4, 2.82) * mm, v(-0.28, 2.95) * mm, v(-0.28, 2.94) * mm, v(-0.4, 2.7) * mm]});
            skFitSpline(sketch, "E851", {"points": [v(-0.4, 2.7) * mm, v(-0.47, 2.56) * mm, v(-0.51, 2.4) * mm, v(-0.5, 2.36) * mm]});
            skFitSpline(sketch, "E852", {"points": [v(-0.5, 2.36) * mm, v(-0.48, 2.3) * mm, v(-0.4, 2.39) * mm, v(-0.33, 2.54) * mm]});
            skFitSpline(sketch, "E853", {"points": [v(-0.33, 2.54) * mm, v(-0.26, 2.7) * mm, v(-0.15, 2.86) * mm, v(-0.09, 2.91) * mm]});
            skFitSpline(sketch, "E854", {"points": [v(-0.09, 2.91) * mm, v(0, 2.97) * mm, v(-0.02, 2.91) * mm, v(-0.12, 2.7) * mm]});
            skFitSpline(sketch, "E855", {"points": [v(-0.12, 2.7) * mm, v(-0.26, 2.45) * mm, v(-0.34, 1.98) * mm, v(-0.24, 1.98) * mm]});
            skFitSpline(sketch, "E856", {"points": [v(-0.24, 1.98) * mm, v(-0.22, 1.98) * mm, v(-0.07, 2.12) * mm, v(0.1, 2.3) * mm]});
            skFitSpline(sketch, "E857", {"points": [v(0.1, 2.3) * mm, v(0.39, 2.58) * mm, v(0.44, 2.6) * mm, v(0.58, 2.52) * mm]});
            skFitSpline(sketch, "E858", {"points": [v(0.58, 2.52) * mm, v(0.71, 2.44) * mm, v(0.78, 2.44) * mm, v(0.96, 2.56) * mm]});
            skFitSpline(sketch, "E859", {"points": [v(0.96, 2.56) * mm, v(1.16, 2.7) * mm, v(1.17, 2.7) * mm, v(1.09, 2.55) * mm]});
            skFitSpline(sketch, "E860", {"points": [v(1.09, 2.55) * mm, v(1.04, 2.47) * mm, v(0.86, 2.36) * mm, v(0.68, 2.3) * mm]});
            skFitSpline(sketch, "E861", {"points": [v(0.68, 2.3) * mm, v(0.5, 2.23) * mm, v(0.35, 2.14) * mm, v(0.36, 2.1) * mm]});
            skFitSpline(sketch, "E862", {"points": [v(0.36, 2.1) * mm, v(0.37, 2.07) * mm, v(0.33, 2) * mm, v(0.27, 1.97) * mm]});
            skFitSpline(sketch, "E863", {"points": [v(0.27, 1.97) * mm, v(0.16, 1.9) * mm, v(0.76, 1.95) * mm, v(0.99, 2.03) * mm]});
            skFitSpline(sketch, "E864", {"points": [v(0.99, 2.03) * mm, v(1.05, 2.05) * mm, v(1.13, 2.02) * mm, v(1.17, 1.96) * mm]});
            skFitSpline(sketch, "E865", {"points": [v(1.17, 1.96) * mm, v(1.21, 1.9) * mm, v(1.23, 1.93) * mm, v(1.21, 2.05) * mm]});
            skFitSpline(sketch, "E866", {"points": [v(1.21, 2.05) * mm, v(1.2, 2.15) * mm, v(1.24, 2.25) * mm, v(1.3, 2.27) * mm]});
            skFitSpline(sketch, "E867", {"points": [v(1.3, 2.27) * mm, v(1.36, 2.3) * mm, v(1.38, 2.26) * mm, v(1.34, 2.16) * mm]});
            skFitSpline(sketch, "E868", {"points": [v(1.34, 2.16) * mm, v(1.28, 2.03) * mm, v(1.3, 2.03) * mm, v(1.48, 2.14) * mm]});
            skFitSpline(sketch, "E869", {"points": [v(1.48, 2.14) * mm, v(1.58, 2.2) * mm, v(1.84, 2.32) * mm, v(2.05, 2.4) * mm]});
            skFitSpline(sketch, "E870", {"points": [v(2.05, 2.4) * mm, v(2.26, 2.48) * mm, v(2.43, 2.56) * mm, v(2.43, 2.6) * mm]});
            skFitSpline(sketch, "E871", {"points": [v(2.43, 2.6) * mm, v(2.43, 2.67) * mm, v(1.74, 3) * mm, v(1.56, 3) * mm]});
            skFitSpline(sketch, "E872", {"points": [v(1.56, 3) * mm, v(1.31, 3) * mm, v(1.32, 3.07) * mm, v(1.63, 3.63) * mm]});
            skFitSpline(sketch, "E873", {"points": [v(1.63, 3.63) * mm, v(1.94, 4.18) * mm, v(1.94, 4.4) * mm, v(1.64, 3.9) * mm]});
            skFitSpline(sketch, "E874", {"points": [v(1.64, 3.9) * mm, v(1.42, 3.55) * mm, v(0.9, 3.1) * mm, v(0.65, 3.03) * mm]});
            skFitSpline(sketch, "E875", {"points": [v(0.65, 3.03) * mm, v(0.54, 3) * mm, v(0.37, 3) * mm, v(0.27, 3) * mm]});
            skFitSpline(sketch, "E876", {"points": [v(0.27, 3) * mm, v(0.1, 3.03) * mm, v(0.08, 3.07) * mm, v(0.07, 3.5) * mm]});
            skFitSpline(sketch, "E877", {"points": [v(0.07, 3.5) * mm, v(0.06, 3.76) * mm, v(0.05, 4) * mm, v(0.05, 4.05) * mm]});
            skFitSpline(sketch, "E878", {"points": [v(0.05, 4.05) * mm, v(0.05, 4.1) * mm, v(-0.24, 3.84) * mm, v(-0.6, 3.48) * mm]});
            skFitSpline(sketch, "E879", {"points": [v(-0.6, 3.48) * mm, v(-1.06, 3) * mm, v(-1.28, 2.84) * mm, v(-1.43, 2.84) * mm]});
            skFitSpline(sketch, "E880", {"points": [v(-1.43, 2.84) * mm, v(-1.66, 2.84) * mm, v(-1.67, 2.89) * mm, v(-1.5, 3.22) * mm]});
            skFitSpline(sketch, "E881", {"points": [v(-1.5, 3.22) * mm, v(-1.43, 3.35) * mm, v(-1.4, 3.5) * mm, v(-1.41, 3.56) * mm]});
            skFitSpline(sketch, "E882", {"points": [v(-1.41, 3.56) * mm, v(-1.43, 3.62) * mm, v(-1.53, 3.49) * mm, v(-1.62, 3.28) * mm]});
            skFitSpline(sketch, "E883", {"points": [v(-1.62, 3.28) * mm, v(-1.8, 2.86) * mm, v(-2.64, 1.96) * mm, v(-3.01, 1.78) * mm]});
            skFitSpline(sketch, "E884", {"points": [v(-3.01, 1.78) * mm, v(-3.26, 1.66) * mm, v(-3.26, 1.66) * mm, v(-3.56, 1.99) * mm]});
            skFitSpline(sketch, "E885", {"points": [v(-3.56, 1.99) * mm, v(-3.73, 2.18) * mm, v(-3.9, 2.46) * mm, v(-3.94, 2.66) * mm]});
            skFitSpline(sketch, "E886", {"points": [v(-3.94, 2.66) * mm, v(-4, 2.84) * mm, v(-4.06, 3) * mm, v(-4.1, 3) * mm]});
            skFitSpline(sketch, "E887", {"points": [v(-4.1, 3) * mm, v(-4.14, 3) * mm, v(-4.17, 3.1) * mm, v(-4.17, 3.23) * mm]});
            skFitSpline(sketch, "E888", {"points": [v(-4.17, 3.23) * mm, v(-4.17, 3.5) * mm, v(-4.27, 3.53) * mm, v(-4.49, 3.31) * mm]});
            skFitSpline(sketch, "E889", {"points": [v(-4.49, 3.31) * mm, v(-4.64, 3.16) * mm, v(-4.64, 3.16) * mm, v(-4.76, 3.33) * mm]});
            skFitSpline(sketch, "E890", {"points": [v(-4.76, 3.33) * mm, v(-4.86, 3.46) * mm, v(-4.87, 3.66) * mm, v(-4.83, 4.42) * mm]});
            skFitSpline(sketch, "E891", {"points": [v(-4.83, 4.42) * mm, v(-4.8, 5.1) * mm, v(-4.8, 5.34) * mm, v(-4.87, 5.34) * mm]});
            skFitSpline(sketch, "E892", {"points": [v(-4.87, 5.34) * mm, v(-4.93, 5.34) * mm, v(-4.97, 5.31) * mm, v(-4.97, 5.28) * mm]});
            skFitSpline(sketch, "E893", {"points": [v(-4.97, 5.28) * mm, v(-4.97, 5.24) * mm, v(-5.01, 5.15) * mm, v(-5.07, 5.08) * mm]});
            skFitSpline(sketch, "E894", {"points": [v(-5.07, 5.08) * mm, v(-5.16, 4.96) * mm, v(-5.2, 4.95) * mm, v(-5.38, 5.05) * mm]});
            skFitSpline(sketch, "E895", {"points": [v(-5.38, 5.05) * mm, v(-5.5, 5.1) * mm, v(-5.67, 5.24) * mm, v(-5.75, 5.35) * mm]});
            skFitSpline(sketch, "E896", {"points": [v(-5.92, 5.17) * mm, v(-5.92, 4.87) * mm, v(-5.96, 4.78) * mm, v(-6.13, 4.64) * mm]});
            skFitSpline(sketch, "E897", {"points": [v(-6.13, 4.64) * mm, v(-6.24, 4.55) * mm, v(-6.44, 4.48) * mm, v(-6.57, 4.48) * mm]});
            skFitSpline(sketch, "E898", {"points": [v(-6.57, 4.48) * mm, v(-6.75, 4.48) * mm, v(-6.8, 4.45) * mm, v(-6.8, 4.3) * mm]});
            skFitSpline(sketch, "E899", {"points": [v(-6.8, 4.3) * mm, v(-6.8, 4.1) * mm, v(-6.53, 3.65) * mm, v(-6.26, 3.4) * mm]});
            skFitSpline(sketch, "E900", {"points": [v(-6.26, 3.4) * mm, v(-6.1, 3.26) * mm, v(-6.08, 3.2) * mm, v(-6.16, 3.1) * mm]});
            skFitSpline(sketch, "E901", {"points": [v(-6.16, 3.1) * mm, v(-6.22, 3.04) * mm, v(-6.32, 3.01) * mm, v(-6.4, 3.03) * mm]});
            skFitSpline(sketch, "E902", {"points": [v(-6.4, 3.03) * mm, v(-6.51, 3.07) * mm, v(-6.52, 3.02) * mm, v(-6.46, 2.55) * mm]});
            skFitSpline(sketch, "E903", {"points": [v(-6.46, 2.55) * mm, v(-6.38, 1.88) * mm, v(-6.36, 1.76) * mm, v(-6.3, 1.7) * mm]});
            skFitSpline(sketch, "E904", {"points": [v(-6.3, 1.7) * mm, v(-6.27, 1.67) * mm, v(-6.29, 1.59) * mm, v(-6.33, 1.52) * mm]});
            skFitSpline(sketch, "E905", {"points": [v(-6.33, 1.52) * mm, v(-6.4, 1.42) * mm, v(-6.38, 1.32) * mm, v(-6.28, 1.15) * mm]});
            skFitSpline(sketch, "E906", {"points": [v(-6.28, 1.15) * mm, v(-6.2, 1.03) * mm, v(-6.17, 1) * mm, v(-6.2, 1.08) * mm]});
            skFitSpline(sketch, "E907", {"points": [v(-6.2, 1.08) * mm, v(-6.23, 1.17) * mm, v(-6.27, 1.3) * mm, v(-6.3, 1.4) * mm]});
            skFitSpline(sketch, "E908", {"points": [v(-6.3, 1.4) * mm, v(-6.32, 1.51) * mm, v(-6.3, 1.5) * mm, v(-6.21, 1.35) * mm]});
            skFitSpline(sketch, "E909", {"points": [v(-6.21, 1.35) * mm, v(-6, 0.97) * mm, v(-5.99, 0.76) * mm, v(-6.19, 0.67) * mm]});
            skFitSpline(sketch, "E910", {"points": [v(-6.19, 0.67) * mm, v(-6.34, 0.6) * mm, v(-6.4, 0.61) * mm, v(-6.5, 0.72) * mm]});
            skFitSpline(sketch, "E911", {"points": [v(-6.5, 0.72) * mm, v(-6.56, 0.79) * mm, v(-6.76, 0.93) * mm, v(-6.94, 1.03) * mm]});
            skFitSpline(sketch, "E912", {"points": [v(-6.94, 1.03) * mm, v(-7.3, 1.24) * mm, v(-7.42, 1.46) * mm, v(-7.49, 2) * mm]});
            skFitSpline(sketch, "E913", {"points": [v(-7.49, 2) * mm, v(-7.53, 2.36) * mm, v(-7.6, 2.46) * mm, v(-7.71, 2.29) * mm]});
            skFitSpline(sketch, "E914", {"points": [v(-7.71, 2.29) * mm, v(-7.74, 2.24) * mm, v(-7.85, 2.17) * mm, v(-7.96, 2.13) * mm]});
            skFitSpline(sketch, "E915", {"points": [v(-7.96, 2.13) * mm, v(-8.2, 2.04) * mm, v(-8.59, 2.24) * mm, v(-8.85, 2.57) * mm]});
            skFitSpline(sketch, "E916", {"points": [v(-8.85, 2.57) * mm, v(-8.94, 2.68) * mm, v(-9.02, 2.76) * mm, v(-9.05, 2.76) * mm]});
            skFitSpline(sketch, "E917", {"points": [v(-9.05, 2.76) * mm, v(-9.12, 2.76) * mm, v(-9, 2.28) * mm, v(-8.88, 2.02) * mm]});
            skFitSpline(sketch, "E918", {"points": [v(-8.88, 2.02) * mm, v(-8.8, 1.89) * mm, v(-8.74, 1.7) * mm, v(-8.73, 1.6) * mm]});
            skFitSpline(sketch, "E919", {"points": [v(-8.73, 1.6) * mm, v(-8.72, 1.5) * mm, v(-8.66, 1.35) * mm, v(-8.59, 1.28) * mm]});
            skFitSpline(sketch, "E920", {"points": [v(-8.59, 1.28) * mm, v(-8.52, 1.2) * mm, v(-8.46, 1.1) * mm, v(-8.46, 1.06) * mm]});
            skFitSpline(sketch, "E921", {"points": [v(-8.46, 1.06) * mm, v(-8.46, 1.01) * mm, v(-8.42, 0.95) * mm, v(-8.37, 0.92) * mm]});
            skFitSpline(sketch, "E922", {"points": [v(-8.37, 0.92) * mm, v(-8.3, 0.88) * mm, v(-8.3, 0.92) * mm, v(-8.33, 1.06) * mm]});
            skFitSpline(sketch, "E923", {"points": [v(-8.33, 1.06) * mm, v(-8.36, 1.19) * mm, v(-8.34, 1.3) * mm, v(-8.27, 1.35) * mm]});
            skFitSpline(sketch, "E924", {"points": [v(-8.27, 1.35) * mm, v(-8.18, 1.42) * mm, v(-8.17, 1.41) * mm, v(-8.2, 1.29) * mm]});
            skFitSpline(sketch, "E925", {"points": [v(-8.2, 1.29) * mm, v(-8.24, 1.13) * mm, v(-8.1, 0.8) * mm, v(-8, 0.8) * mm]});
            skFitSpline(sketch, "E926", {"points": [v(-8, 0.8) * mm, v(-7.97, 0.8) * mm, v(-7.94, 0.94) * mm, v(-7.93, 1.1) * mm]});
            skFitSpline(sketch, "E927", {"points": [v(-7.93, 1.1) * mm, v(-7.92, 1.27) * mm, v(-7.88, 1.49) * mm, v(-7.84, 1.6) * mm]});
            skFitSpline(sketch, "E928", {"points": [v(-7.84, 1.6) * mm, v(-7.77, 1.76) * mm, v(-7.76, 1.75) * mm, v(-7.75, 1.45) * mm]});
            skFitSpline(sketch, "E929", {"points": [v(-7.75, 1.45) * mm, v(-7.75, 1.26) * mm, v(-7.7, 1.03) * mm, v(-7.66, 0.94) * mm]});
            skFitSpline(sketch, "E930", {"points": [v(-7.66, 0.94) * mm, v(-7.59, 0.82) * mm, v(-7.59, 0.77) * mm, v(-7.66, 0.74) * mm]});
            skFitSpline(sketch, "E931", {"points": [v(-7.66, 0.74) * mm, v(-7.81, 0.7) * mm, v(-7.76, 0.6) * mm, v(-7.56, 0.54) * mm]});
            skFitSpline(sketch, "E932", {"points": [v(-7.56, 0.54) * mm, v(-7.45, 0.51) * mm, v(-7.31, 0.45) * mm, v(-7.26, 0.4) * mm]});
            skFitSpline(sketch, "E933", {"points": [v(-7.26, 0.4) * mm, v(-7.2, 0.33) * mm, v(-7.08, 0.25) * mm, v(-7, 0.2) * mm]});
            skFitSpline(sketch, "E934", {"points": [v(-7, 0.2) * mm, v(-6.9, 0.15) * mm, v(-6.83, 0.07) * mm, v(-6.83, 0.01) * mm]});
            skFitSpline(sketch, "E935", {"points": [v(-6.83, 0.01) * mm, v(-6.82, -0.2) * mm, v(-6.53, -0.75) * mm, v(-6.42, -0.8) * mm]});
            skFitSpline(sketch, "E936", {"points": [v(-6.42, -0.8) * mm, v(-6.36, -0.82) * mm, v(-6.33, -0.8) * mm, v(-6.36, -0.75) * mm]});
            skFitSpline(sketch, "E937", {"points": [v(-6.36, -0.75) * mm, v(-6.44, -0.62) * mm, v(-6.42, 0.04) * mm, v(-6.32, 0.13) * mm]});
            skFitSpline(sketch, "E938", {"points": [v(-6.32, 0.13) * mm, v(-6.26, 0.19) * mm, v(-6.24, 0.03) * mm, v(-6.24, -0.43) * mm]});
            skFitSpline(sketch, "E939", {"points": [v(-6.24, -0.43) * mm, v(-6.24, -1.04) * mm, v(-6.23, -1.07) * mm, v(-6.02, -1.18) * mm]});
            skFitSpline(sketch, "E940", {"points": [v(-6.02, -1.18) * mm, v(-5.9, -1.24) * mm, v(-5.66, -1.42) * mm, v(-5.48, -1.57) * mm]});
            skFitSpline(sketch, "E941", {"points": [v(-5.48, -1.57) * mm, v(-5.3, -1.72) * mm, v(-5.14, -1.82) * mm, v(-5.11, -1.79) * mm]});
            skFitSpline(sketch, "E942", {"points": [v(-5.11, -1.79) * mm, v(-5.04, -1.7) * mm, v(-4.98, -0.91) * mm, v(-5.05, -0.91) * mm]});
            skFitSpline(sketch, "E943", {"points": [v(-5.05, -0.91) * mm, v(-5.08, -0.91) * mm, v(-5.1, -0.83) * mm, v(-5.1, -0.72) * mm]});
            skFitSpline(sketch, "E944", {"points": [v(-5.1, -0.72) * mm, v(-5.1, -0.61) * mm, v(-5.24, -0.36) * mm, v(-5.4, -0.15) * mm]});
            skFitSpline(sketch, "E945", {"points": [v(-5.4, -0.15) * mm, v(-5.9, 0.45) * mm, v(-5.9, 0.47) * mm, v(-5.48, 0.12) * mm]});
            skFitSpline(sketch, "E946", {"points": [v(-5.48, 0.12) * mm, v(-5.26, -0.06) * mm, v(-5.04, -0.21) * mm, v(-5, -0.21) * mm]});
            skFitSpline(sketch, "E947", {"points": [v(-5, -0.21) * mm, v(-4.95, -0.21) * mm, v(-4.87, -0.12) * mm, v(-4.82, -0.01) * mm]});
            skFitSpline(sketch, "E948", {"points": [v(-4.82, -0.01) * mm, v(-4.7, 0.23) * mm, v(-4.7, 0.36) * mm, v(-4.8, 0.3) * mm]});
            skFitSpline(sketch, "E949", {"points": [v(-4.8, 0.3) * mm, v(-4.88, 0.25) * mm, v(-4.97, 0.43) * mm, v(-4.97, 0.65) * mm]});
            skFitSpline(sketch, "E950", {"points": [v(-4.97, 0.65) * mm, v(-4.97, 0.8) * mm, v(-5.3, 1.09) * mm, v(-5.74, 1.3) * mm]});
            skFitSpline(sketch, "E951", {"points": [v(-5.74, 1.3) * mm, v(-6.04, 1.46) * mm, v(-6.06, 1.58) * mm, v(-5.83, 1.83) * mm]});
            skFitSpline(sketch, "E952", {"points": [v(-5.83, 1.83) * mm, v(-5.67, 2.01) * mm, v(-5.67, 1.97) * mm, v(-5.8, 1.63) * mm]});
            skFitSpline(sketch, "E953", {"points": [v(-5.8, 1.63) * mm, v(-5.84, 1.56) * mm, v(-5.72, 1.45) * mm, v(-5.47, 1.3) * mm]});
            skFitSpline(sketch, "E954", {"points": [v(-5.47, 1.3) * mm, v(-5.26, 1.18) * mm, v(-5.02, 1.01) * mm, v(-4.94, 0.93) * mm]});
            skFitSpline(sketch, "E955", {"points": [v(-4.94, 0.93) * mm, v(-4.8, 0.77) * mm, v(-4.8, 0.77) * mm, v(-4.84, 0.92) * mm]});
            skFitSpline(sketch, "E956", {"points": [v(-4.84, 0.92) * mm, v(-4.86, 1) * mm, v(-4.91, 1.33) * mm, v(-4.96, 1.63) * mm]});
            skFitSpline(sketch, "E957", {"points": [v(-4.96, 1.63) * mm, v(-5.01, 1.93) * mm, v(-5.07, 2.25) * mm, v(-5.09, 2.34) * mm]});
            skFitSpline(sketch, "E958", {"points": [v(-5.09, 2.34) * mm, v(-5.1, 2.43) * mm, v(-5.27, 2.66) * mm, v(-5.44, 2.86) * mm]});
            skFitSpline(sketch, "E959", {"points": [v(-5.44, 2.86) * mm, v(-5.77, 3.22) * mm, v(-5.77, 3.22) * mm, v(-5.65, 3.5) * mm]});
            skFitSpline(sketch, "E960", {"points": [v(-5.65, 3.5) * mm, v(-5.5, 3.83) * mm, v(-5.43, 3.87) * mm, v(-5.52, 3.56) * mm]});
            skFitSpline(sketch, "E961", {"points": [v(-5.52, 3.56) * mm, v(-5.59, 3.32) * mm, v(-5.45, 2.96) * mm, v(-5.3, 2.95) * mm]});
            skFitSpline(sketch, "E962", {"points": [v(-5.3, 2.95) * mm, v(-5.24, 2.94) * mm, v(-5.17, 2.93) * mm, v(-5.13, 2.93) * mm]});
            skFitSpline(sketch, "E963", {"points": [v(-5.13, 2.93) * mm, v(-5, 2.9) * mm, v(-4.8, 2.16) * mm, v(-4.82, 1.75) * mm]});
            skFitSpline(sketch, "E964", {"points": [v(-4.82, 1.75) * mm, v(-4.84, 1.3) * mm, v(-4.78, 1.19) * mm, v(-4.65, 1.43) * mm]});
            skFitSpline(sketch, "E965", {"points": [v(-4.65, 1.43) * mm, v(-4.59, 1.54) * mm, v(-4.57, 1.74) * mm, v(-4.6, 1.95) * mm]});
            skFitSpline(sketch, "E966", {"points": [v(-4.6, 1.95) * mm, v(-4.64, 2.15) * mm, v(-4.63, 2.3) * mm, v(-4.58, 2.3) * mm]});
            skFitSpline(sketch, "E967", {"points": [v(-4.58, 2.3) * mm, v(-4.54, 2.3) * mm, v(-4.48, 2.12) * mm, v(-4.45, 1.9) * mm]});
            skFitSpline(sketch, "E968", {"points": [v(-4.45, 1.9) * mm, v(-4.4, 1.6) * mm, v(-4.43, 1.46) * mm, v(-4.57, 1.2) * mm]});
            skFitSpline(sketch, "E969", {"points": [v(-4.57, 1.2) * mm, v(-4.68, 0.98) * mm, v(-4.72, 0.82) * mm, v(-4.68, 0.7) * mm]});
            skFitSpline(sketch, "E970", {"points": [v(-4.68, 0.7) * mm, v(-4.64, 0.6) * mm, v(-4.63, 0.48) * mm, v(-4.64, 0.42) * mm]});
            skFitSpline(sketch, "E971", {"points": [v(-4.64, 0.42) * mm, v(-4.65, 0.33) * mm, v(-4.61, 0.35) * mm, v(-4.5, 0.46) * mm]});
            skFitSpline(sketch, "E972", {"points": [v(-4.5, 0.46) * mm, v(-4.3, 0.67) * mm, v(-3.86, 1.49) * mm, v(-3.85, 1.66) * mm]});
            skFitSpline(sketch, "E973", {"points": [v(-3.85, 1.66) * mm, v(-3.85, 1.74) * mm, v(-3.82, 1.72) * mm, v(-3.77, 1.6) * mm]});
            skFitSpline(sketch, "E974", {"points": [v(-3.77, 1.6) * mm, v(-3.69, 1.4) * mm, v(-3.91, 0.84) * mm, v(-4.17, 0.61) * mm]});
            skFitSpline(sketch, "E975", {"points": [v(-4.17, 0.61) * mm, v(-4.25, 0.54) * mm, v(-4.38, 0.22) * mm, v(-4.46, -0.1) * mm]});
            skFitSpline(sketch, "E976", {"points": [v(-4.46, -0.1) * mm, v(-4.54, -0.42) * mm, v(-4.63, -0.68) * mm, v(-4.66, -0.68) * mm]});
            skFitSpline(sketch, "E977", {"points": [v(-4.66, -0.68) * mm, v(-4.7, -0.68) * mm, v(-4.72, -1.08) * mm, v(-4.7, -1.58) * mm]});
            skFitSpline(sketch, "E978", {"points": [v(-4.7, -1.58) * mm, v(-4.7, -2.07) * mm, v(-4.67, -2.47) * mm, v(-4.64, -2.46) * mm]});
            skFitSpline(sketch, "E979", {"points": [v(-4.64, -2.46) * mm, v(-4.61, -2.45) * mm, v(-4.46, -2.28) * mm, v(-4.3, -2.09) * mm]});
            skFitSpline(sketch, "E980", {"points": [v(9.22, -1.38) * mm, v(9.25, -1.34) * mm, v(9.23, -1.3) * mm, v(9.19, -1.3) * mm]});
            skFitSpline(sketch, "E981", {"points": [v(9.19, -1.3) * mm, v(9.14, -1.3) * mm, v(9.1, -1.34) * mm, v(9.1, -1.38) * mm]});
            skFitSpline(sketch, "E982", {"points": [v(9.1, -1.38) * mm, v(9.1, -1.43) * mm, v(9.12, -1.46) * mm, v(9.14, -1.46) * mm]});
            skFitSpline(sketch, "E983", {"points": [v(9.14, -1.46) * mm, v(9.16, -1.46) * mm, v(9.2, -1.43) * mm, v(9.22, -1.38) * mm]});
            skFitSpline(sketch, "E984", {"points": [v(9.34, -0.77) * mm, v(9.34, -0.72) * mm, v(9.3, -0.7) * mm, v(9.26, -0.72) * mm]});
            skFitSpline(sketch, "E985", {"points": [v(9.26, -0.72) * mm, v(9.22, -0.75) * mm, v(9.18, -0.84) * mm, v(9.18, -0.94) * mm]});
            skFitSpline(sketch, "E986", {"points": [v(9.18, -0.94) * mm, v(9.19, -1.08) * mm, v(9.2, -1.09) * mm, v(9.26, -1) * mm]});
            skFitSpline(sketch, "E987", {"points": [v(9.26, -1) * mm, v(9.3, -0.93) * mm, v(9.34, -0.83) * mm, v(9.34, -0.77) * mm]});
            skFitSpline(sketch, "E988", {"points": [v(0.03, -0.52) * mm, v(0.04, -0.42) * mm, v(0.03, -0.42) * mm, v(-0.04, -0.52) * mm]});
            skFitSpline(sketch, "E989", {"points": [v(-0.04, -0.52) * mm, v(-0.08, -0.59) * mm, v(-0.11, -0.71) * mm, v(-0.11, -0.8) * mm]});
            skFitSpline(sketch, "E990", {"points": [v(-0.11, -0.8) * mm, v(-0.1, -0.95) * mm, v(-0.1, -0.95) * mm, v(-0.04, -0.8) * mm]});
            skFitSpline(sketch, "E991", {"points": [v(-0.04, -0.8) * mm, v(0, -0.71) * mm, v(0.03, -0.59) * mm, v(0.03, -0.52) * mm]});
            skFitSpline(sketch, "E992", {"points": [v(-6.95, -0.48) * mm, v(-6.95, -0.46) * mm, v(-7.03, -0.3) * mm, v(-7.13, -0.1) * mm]});
            skFitSpline(sketch, "E993", {"points": [v(-7.13, -0.1) * mm, v(-7.24, 0.14) * mm, v(-7.38, 0.28) * mm, v(-7.54, 0.35) * mm]});
            skFitSpline(sketch, "E994", {"points": [v(-7.54, 0.35) * mm, v(-7.68, 0.4) * mm, v(-7.85, 0.49) * mm, v(-7.92, 0.55) * mm]});
            skFitSpline(sketch, "E995", {"points": [v(-7.92, 0.55) * mm, v(-8.14, 0.74) * mm, v(-8.16, 0.46) * mm, v(-7.94, 0.2) * mm]});
            skFitSpline(sketch, "E996", {"points": [v(-7.94, 0.2) * mm, v(-7.74, -0.02) * mm, v(-7.72, -0.08) * mm, v(-7.74, -0.3) * mm]});
            skFitSpline(sketch, "E997", {"points": [v(-7.74, -0.3) * mm, v(-7.76, -0.48) * mm, v(-7.5, -0.58) * mm, v(-7.18, -0.54) * mm]});
            skFitSpline(sketch, "E998", {"points": [v(-7.18, -0.54) * mm, v(-7.06, -0.52) * mm, v(-6.95, -0.5) * mm, v(-6.95, -0.48) * mm]});
            skFitSpline(sketch, "E999", {"points": [v(-8.27, -0.45) * mm, v(-8.25, -0.41) * mm, v(-8.32, -0.39) * mm, v(-8.42, -0.4) * mm]});
            skFitSpline(sketch, "E1000", {"points": [v(-8.42, -0.4) * mm, v(-8.53, -0.4) * mm, v(-8.62, -0.43) * mm, v(-8.62, -0.46) * mm]});
            skFitSpline(sketch, "E1001", {"points": [v(-8.62, -0.46) * mm, v(-8.62, -0.55) * mm, v(-8.32, -0.54) * mm, v(-8.27, -0.45) * mm]});
            skFitSpline(sketch, "E1002", {"points": [v(-6.9, -0.17) * mm, v(-6.95, -0.07) * mm, v(-7, -0.02) * mm, v(-7.02, -0.06) * mm]});
            skFitSpline(sketch, "E1003", {"points": [v(-7.02, -0.06) * mm, v(-7.04, -0.1) * mm, v(-7, -0.19) * mm, v(-6.95, -0.25) * mm]});
            skFitSpline(sketch, "E1004", {"points": [v(-6.95, -0.25) * mm, v(-6.81, -0.42) * mm, v(-6.8, -0.4) * mm, v(-6.9, -0.17) * mm]});
            skFitSpline(sketch, "E1005", {"points": [v(-3.55, -0.01) * mm, v(-3.6, 0.1) * mm, v(-3.65, 0.17) * mm, v(-3.66, 0.16) * mm]});
            skFitSpline(sketch, "E1006", {"points": [v(-3.66, 0.16) * mm, v(-3.71, 0.11) * mm, v(-3.6, -0.21) * mm, v(-3.53, -0.21) * mm]});
            skFitSpline(sketch, "E1007", {"points": [v(-3.53, -0.21) * mm, v(-3.5, -0.21) * mm, v(-3.5, -0.12) * mm, v(-3.55, -0.01) * mm]});
            skFitSpline(sketch, "E1008", {"points": [v(9.31, 0.2) * mm, v(9.3, 0.25) * mm, v(9.27, 0.2) * mm, v(9.27, 0.1) * mm]});
            skFitSpline(sketch, "E1009", {"points": [v(9.27, 0.1) * mm, v(9.27, 0) * mm, v(9.3, -0.05) * mm, v(9.31, 0) * mm]});
            skFitSpline(sketch, "E1010", {"points": [v(9.31, 0) * mm, v(9.34, 0.06) * mm, v(9.34, 0.15) * mm, v(9.31, 0.2) * mm]});
            skFitSpline(sketch, "E1011", {"points": [v(-1.3, 0.85) * mm, v(-1.16, 1.02) * mm, v(-1.24, 1.02) * mm, v(-1.43, 0.85) * mm]});
            skFitSpline(sketch, "E1012", {"points": [v(-1.43, 0.85) * mm, v(-1.54, 0.75) * mm, v(-1.63, 0.64) * mm, v(-1.63, 0.61) * mm]});
            skFitSpline(sketch, "E1013", {"points": [v(-1.63, 0.61) * mm, v(-1.63, 0.55) * mm, v(-1.39, 0.71) * mm, v(-1.3, 0.85) * mm]});
            skFitSpline(sketch, "E1014", {"points": [v(-2.2, 0.98) * mm, v(-2.23, 1.04) * mm, v(-2.25, 1.02) * mm, v(-2.26, 0.93) * mm]});
            skFitSpline(sketch, "E1015", {"points": [v(-2.26, 0.93) * mm, v(-2.26, 0.85) * mm, v(-2.24, 0.8) * mm, v(-2.22, 0.83) * mm]});
            skFitSpline(sketch, "E1016", {"points": [v(-2.22, 0.83) * mm, v(-2.19, 0.85) * mm, v(-2.19, 0.92) * mm, v(-2.2, 0.98) * mm]});
            skFitSpline(sketch, "E1017", {"points": [v(-8.86, 1.2) * mm, v(-8.86, 1.23) * mm, v(-8.98, 1.34) * mm, v(-9.12, 1.44) * mm]});
            skFitSpline(sketch, "E1018", {"points": [v(-9.14, 1.37) * mm, v(-8.9, 1.1) * mm, v(-8.86, 1.08) * mm, v(-8.86, 1.2) * mm]});
            skFitSpline(sketch, "E1019", {"points": [v(-1.39, 1.35) * mm, v(-1.39, 1.44) * mm, v(-1.4, 1.5) * mm, v(-1.42, 1.5) * mm]});
            skFitSpline(sketch, "E1020", {"points": [v(-1.42, 1.5) * mm, v(-1.44, 1.5) * mm, v(-1.47, 1.44) * mm, v(-1.5, 1.35) * mm]});
            skFitSpline(sketch, "E1021", {"points": [v(-1.5, 1.35) * mm, v(-1.51, 1.27) * mm, v(-1.5, 1.2) * mm, v(-1.46, 1.2) * mm]});
            skFitSpline(sketch, "E1022", {"points": [v(-1.46, 1.2) * mm, v(-1.42, 1.2) * mm, v(-1.39, 1.27) * mm, v(-1.39, 1.35) * mm]});
            skFitSpline(sketch, "E1023", {"points": [v(1.71, 1.66) * mm, v(1.71, 1.75) * mm, v(1.56, 1.85) * mm, v(1.5, 1.8) * mm]});
            skFitSpline(sketch, "E1024", {"points": [v(1.5, 1.8) * mm, v(1.44, 1.74) * mm, v(1.54, 1.59) * mm, v(1.64, 1.59) * mm]});
            skFitSpline(sketch, "E1025", {"points": [v(1.64, 1.59) * mm, v(1.68, 1.59) * mm, v(1.71, 1.62) * mm, v(1.71, 1.66) * mm]});
            skFitSpline(sketch, "E1026", {"points": [v(-2.58, 2.33) * mm, v(-2.48, 2.44) * mm, v(-2.41, 2.53) * mm, v(-2.43, 2.53) * mm]});
            skFitSpline(sketch, "E1027", {"points": [v(-2.43, 2.53) * mm, v(-2.46, 2.53) * mm, v(-2.56, 2.44) * mm, v(-2.66, 2.33) * mm]});
            skFitSpline(sketch, "E1028", {"points": [v(-2.66, 2.33) * mm, v(-2.76, 2.22) * mm, v(-2.83, 2.14) * mm, v(-2.8, 2.14) * mm]});
            skFitSpline(sketch, "E1029", {"points": [v(-2.8, 2.14) * mm, v(-2.79, 2.14) * mm, v(-2.68, 2.22) * mm, v(-2.58, 2.33) * mm]});
            skFitSpline(sketch, "E1030", {"points": [v(8.8, 3.86) * mm, v(8.75, 3.97) * mm, v(8.71, 4) * mm, v(8.71, 3.96) * mm]});
            skFitSpline(sketch, "E1031", {"points": [v(8.71, 3.96) * mm, v(8.7, 3.84) * mm, v(8.8, 3.6) * mm, v(8.84, 3.65) * mm]});
            skFitSpline(sketch, "E1032", {"points": [v(8.84, 3.65) * mm, v(8.85, 3.66) * mm, v(8.83, 3.76) * mm, v(8.8, 3.86) * mm]});
            skFitSpline(sketch, "E1033", {"points": [v(8, 5.37) * mm, v(8, 5.38) * mm, v(7.88, 5.53) * mm, v(7.75, 5.7) * mm]});
            skFitSpline(sketch, "E1034", {"points": [v(7.75, 5.7) * mm, v(7.62, 5.86) * mm, v(7.51, 5.95) * mm, v(7.51, 5.91) * mm]});
            skFitSpline(sketch, "E1035", {"points": [v(7.51, 5.91) * mm, v(7.51, 5.87) * mm, v(7.6, 5.73) * mm, v(7.72, 5.6) * mm]});
            skFitSpline(sketch, "E1036", {"points": [v(7.72, 5.6) * mm, v(7.92, 5.36) * mm, v(8, 5.3) * mm, v(8, 5.37) * mm]});
            skFitSpline(sketch, "E1037", {"points": [v(7.12, 6.34) * mm, v(6.89, 6.65) * mm, v(6.3, 7.28) * mm, v(6.37, 7.14) * mm]});
            skFitSpline(sketch, "E1038", {"points": [v(6.37, 7.14) * mm, v(6.44, 7.01) * mm, v(7.21, 6.12) * mm, v(7.26, 6.12) * mm]});
            skFitSpline(sketch, "E1039", {"points": [v(7.26, 6.12) * mm, v(7.27, 6.12) * mm, v(7.21, 6.22) * mm, v(7.12, 6.34) * mm]});
            skFitSpline(sketch, "E1040", {"points": [v(-5.72, 7.96) * mm, v(-5.4, 8.2) * mm, v(-5.5, 8.21) * mm, v(-5.84, 7.96) * mm]});
            skFitSpline(sketch, "E1041", {"points": [v(-5.84, 7.96) * mm, v(-5.99, 7.85) * mm, v(-6.08, 7.76) * mm, v(-6.04, 7.77) * mm]});
            skFitSpline(sketch, "E1042", {"points": [v(-6.04, 7.77) * mm, v(-6, 7.77) * mm, v(-5.85, 7.85) * mm, v(-5.72, 7.96) * mm]});
            skFitSpline(sketch, "E1043", {"points": [v(5.46, 8.02) * mm, v(5.38, 8.1) * mm, v(5.37, 8.09) * mm, v(5.41, 7.98) * mm]});
            skFitSpline(sketch, "E1044", {"points": [v(5.41, 7.98) * mm, v(5.44, 7.9) * mm, v(5.49, 7.86) * mm, v(5.51, 7.88) * mm]});
            skFitSpline(sketch, "E1045", {"points": [v(5.51, 7.88) * mm, v(5.54, 7.9) * mm, v(5.51, 7.97) * mm, v(5.46, 8.02) * mm]});
            skFitSpline(sketch, "E1046", {"points": [v(4.65, 8.03) * mm, v(4.65, 8.05) * mm, v(4.55, 8.14) * mm, v(4.42, 8.23) * mm]});
            skFitSpline(sketch, "E1047", {"points": [v(4.42, 8.23) * mm, v(4.24, 8.35) * mm, v(4.17, 8.37) * mm, v(4.13, 8.3) * mm]});
            skFitSpline(sketch, "E1048", {"points": [v(4.13, 8.3) * mm, v(4.1, 8.24) * mm, v(4.1, 8.22) * mm, v(4.13, 8.25) * mm]});
            skFitSpline(sketch, "E1049", {"points": [v(4.13, 8.25) * mm, v(4.17, 8.28) * mm, v(4.29, 8.24) * mm, v(4.4, 8.15) * mm]});
            skFitSpline(sketch, "E1050", {"points": [v(4.4, 8.15) * mm, v(4.6, 8) * mm, v(4.65, 7.97) * mm, v(4.65, 8.03) * mm]});
            skFitSpline(sketch, "E1051", {"points": [v(4.07, 8.44) * mm, v(4.05, 8.46) * mm, v(3.98, 8.47) * mm, v(3.92, 8.44) * mm]});
            skFitSpline(sketch, "E1052", {"points": [v(3.92, 8.44) * mm, v(3.86, 8.42) * mm, v(3.88, 8.4) * mm, v(3.97, 8.4) * mm]});
            skFitSpline(sketch, "E1053", {"points": [v(3.97, 8.4) * mm, v(4.05, 8.4) * mm, v(4.1, 8.41) * mm, v(4.07, 8.44) * mm]});
            skCircle(sketch, "E1054", {"center": v(0, 0) * mm, "radius": 10 * mm, "construction": true});
            skSolve(sketch);
        }
        {
            var Q0;
            Q0=qCreatedBy(makeId("Top.planeOp"),FACE);
            var sketch = newSketch(context, id + "F1", { "sketchPlane" : qUnion([Q0])});
            skFitSpline(sketch, "E1055", {"points": [v(-4.66, 5.34) * mm, v(-4.5, 4.53) * mm, v(-4.62, 3.83) * mm], "startDerivative": vector(0.95, -2.37) * mm, "endDerivative": vector(-0.36, -2.16) * mm});
            skFitSpline(sketch, "E1056", {"points": [v(-4.66, 5.34) * mm, v(-4.79, 4.55) * mm, v(-4.62, 3.83) * mm], "startDerivative": vector(-0.42, -1.58) * mm, "endDerivative": vector(0.73, -0.8) * mm});
            skFitSpline(sketch, "E1057", {"points": [v(0.18, 4.78) * mm, v(0.23, 3.94) * mm], "startDerivative": vector(0.78, 0.17) * mm, "endDerivative": vector(-0.3, -0.87) * mm});
            skFitSpline(sketch, "E1058", {"points": [v(0.18, 4.78) * mm, v(0.23, 3.94) * mm], "startDerivative": vector(-0.95, -1.54) * mm, "endDerivative": vector(1.2, -0.89) * mm});
            skFitSpline(sketch, "E1059", {"points": [v(2.36, -2.33) * mm, v(2.26, -2.74) * mm], "startDerivative": vector(-0.68, -0.67) * mm, "endDerivative": vector(0.72, -0.37) * mm});
            skLineSegment(sketch, "E1060", {"start": v(2.36, -2.33) * mm, "end": v(2.42, -2.09) * mm});
            skLineSegment(sketch, "E1061", {"start": v(2.42, -2.09) * mm, "end": v(2.26, -2.05) * mm});
            skLineSegment(sketch, "E1062", {"start": v(2.26, -2.05) * mm, "end": v(1.98, -2.55) * mm});
            skLineSegment(sketch, "E1063", {"start": v(1.98, -2.55) * mm, "end": v(2.2, -2.77) * mm});
            skLineSegment(sketch, "E1064", {"start": v(2.2, -2.77) * mm, "end": v(2.26, -2.74) * mm});
            skFitSpline(sketch, "E1065", {"points": [v(1.17, -4.25) * mm, v(0.83, -4.36) * mm], "startDerivative": vector(-0.82, 0.67) * mm, "endDerivative": vector(-0.1, -0.93) * mm});
            skLineSegment(sketch, "E1066", {"start": v(1.17, -4.25) * mm, "end": v(1.81, -4.6) * mm});
            skLineSegment(sketch, "E1067", {"start": v(1.81, -4.6) * mm, "end": v(1.88, -4.54) * mm});
            skLineSegment(sketch, "E1068", {"start": v(1.88, -4.54) * mm, "end": v(1.78, -4.33) * mm});
            skLineSegment(sketch, "E1069", {"start": v(1.78, -4.33) * mm, "end": v(1.45, -4.05) * mm});
            skLineSegment(sketch, "E1070", {"start": v(1.45, -4.05) * mm, "end": v(1.12, -3.93) * mm});
            skLineSegment(sketch, "E1071", {"start": v(1.12, -3.93) * mm, "end": v(0.88, -3.97) * mm});
            skLineSegment(sketch, "E1072", {"start": v(0.88, -3.97) * mm, "end": v(0.77, -4.1) * mm});
            skLineSegment(sketch, "E1073", {"start": v(0.77, -4.1) * mm, "end": v(0.74, -4.38) * mm});
            skLineSegment(sketch, "E1074", {"start": v(0.74, -4.38) * mm, "end": v(0.83, -4.36) * mm});
            skLineSegment(sketch, "E1075", {"start": v(-7, -6.1) * mm, "end": v(-6.83, -6.2) * mm});
            skLineSegment(sketch, "E1076", {"start": v(-6.83, -6.2) * mm, "end": v(-6.82, -6.32) * mm});
            skLineSegment(sketch, "E1077", {"start": v(-6.82, -6.32) * mm, "end": v(-6.97, -6.33) * mm});
            skLineSegment(sketch, "E1078", {"start": v(-6.97, -6.33) * mm, "end": v(-7.03, -6.24) * mm});
            skLineSegment(sketch, "E1079", {"start": v(-7.03, -6.24) * mm, "end": v(-7, -6.1) * mm});
            skFitSpline(sketch, "E1080", {"points": [v(8.45, 5.09) * mm, v(7.92, 5.78) * mm], "startDerivative": vector(-0.02, 0.86) * mm, "endDerivative": vector(-0.77, 1.09) * mm});
            skLineSegment(sketch, "E1081", {"start": v(7.92, 5.78) * mm, "end": v(7.9, 5.74) * mm});
            skLineSegment(sketch, "E1082", {"start": v(7.9, 5.74) * mm, "end": v(8.16, 5.25) * mm});
            skLineSegment(sketch, "E1083", {"start": v(8.16, 5.25) * mm, "end": v(8.45, 5.09) * mm});
            skFitSpline(sketch, "E1084", {"points": [v(6.16, 7.52) * mm, v(5.04, 8.33) * mm], "startDerivative": vector(-1.1, 1.1) * mm, "endDerivative": vector(-1.01, 0.46) * mm});
            skLineSegment(sketch, "E1085", {"start": v(5.04, 8.33) * mm, "end": v(5.04, 8.16) * mm});
            skLineSegment(sketch, "E1086", {"start": v(5.04, 8.16) * mm, "end": v(5.11, 8.02) * mm});
            skLineSegment(sketch, "E1087", {"start": v(5.11, 8.02) * mm, "end": v(5.73, 7.63) * mm});
            skLineSegment(sketch, "E1088", {"start": v(5.73, 7.63) * mm, "end": v(6.06, 7.45) * mm});
            skLineSegment(sketch, "E1089", {"start": v(6.06, 7.45) * mm, "end": v(6.16, 7.52) * mm});
            skFitSpline(sketch, "E1090", {"points": [v(-6.08, 5.8) * mm, v(-6.45, 6.07) * mm], "startDerivative": vector(-0.25, 0.7) * mm, "endDerivative": vector(-0.84, -0.46) * mm});
            skFitSpline(sketch, "E1091", {"points": [v(-5.88, 5.92) * mm, v(-5.8, 6.32) * mm], "startDerivative": vector(-0.1, 0.49) * mm, "endDerivative": vector(0.77, 0.24) * mm});
            skLineSegment(sketch, "E1092", {"start": v(-6.08, 5.8) * mm, "end": v(-5.88, 5.92) * mm});
            skLineSegment(sketch, "E1093", {"start": v(-6.45, 6.07) * mm, "end": v(-6.49, 6.13) * mm});
            skLineSegment(sketch, "E1094", {"start": v(-6.49, 6.13) * mm, "end": v(-5.81, 6.37) * mm});
            skLineSegment(sketch, "E1095", {"start": v(-5.81, 6.37) * mm, "end": v(-5.8, 6.32) * mm});
            skLineSegment(sketch, "E1096", {"start": v(-0.92, 3.54) * mm, "end": v(-1.37, 3.07) * mm});
            skLineSegment(sketch, "E1097", {"start": v(-1.37, 3.07) * mm, "end": v(-1.37, 2.9) * mm});
            skLineSegment(sketch, "E1098", {"start": v(-1.37, 2.9) * mm, "end": v(-1.13, 3.04) * mm});
            skLineSegment(sketch, "E1099", {"start": v(-1.13, 3.04) * mm, "end": v(-0.86, 3.37) * mm});
            skLineSegment(sketch, "E1100", {"start": v(-0.86, 3.37) * mm, "end": v(-0.92, 3.54) * mm});
            skLineSegment(sketch, "E1101", {"start": v(-7.05, -6.08) * mm, "end": v(-7.34, -5.9) * mm});
            skLineSegment(sketch, "E1102", {"start": v(-7.34, -5.9) * mm, "end": v(-7.31, -6.07) * mm});
            skLineSegment(sketch, "E1103", {"start": v(-7.31, -6.07) * mm, "end": v(-7.24, -6.13) * mm});
            skLineSegment(sketch, "E1104", {"start": v(-7.24, -6.13) * mm, "end": v(-7.05, -6.08) * mm});
            skLineSegment(sketch, "E1105", {"start": v(8.94, -4.25) * mm, "end": v(8.35, -5.29) * mm});
            skLineSegment(sketch, "E1106", {"start": v(8.35, -5.29) * mm, "end": v(8.51, -4.64) * mm});
            skLineSegment(sketch, "E1107", {"start": v(8.51, -4.64) * mm, "end": v(8.94, -4.25) * mm});
            skSolve(sketch);
        }
        {
            var Q0;
            Q0=makeQuery(id+"F0.imprint","IMPRINT",FACE,{"disambiguationData":[TD([[makeQuery(id+"F0.imprint","IMPRINT",EDGE,{"derivedFrom":sQuery(id+"F0.wireOp",EDGE,"E0")}),-1.0]])]});
            var Q1;
            Q1=makeQuery(id+"F0.imprint","IMPRINT",FACE,{"disambiguationData":[TD([[makeQuery(id+"F0.imprint","IMPRINT",EDGE,{"derivedFrom":sQuery(id+"F0.wireOp",EDGE,"E778")}),-1.0]])]});
            var Q2;
            {var subQ0=sQuery(id+"F0.wireOp",EDGE,"E35");Q2=makeQuery(id+"F0.imprint","IMPRINT",FACE,{"disambiguationData":[TD([[makeQuery(id+"F0.imprint","IMPRINT",EDGE,{"derivedFrom":subQ0}),-1.0]])]});}
            var Q3;
            {var subQ0=sQuery(id+"F0.wireOp",EDGE,"E735");Q3=makeQuery(id+"F0.imprint","IMPRINT",FACE,{"disambiguationData":[TD([[makeQuery(id+"F0.imprint","IMPRINT",EDGE,{"derivedFrom":subQ0}),-1.0]])]});}
            var Q4;
            Q4=makeQuery(id+"F0.imprint","IMPRINT",FACE,{"disambiguationData":[TD([[makeQuery(id+"F0.imprint","IMPRINT",EDGE,{"derivedFrom":sQuery(id+"F0.wireOp",EDGE,"E771")}),-1.0]])]});
            var Q5;
            Q5=makeQuery(id+"F0.imprint","IMPRINT",FACE,{"disambiguationData":[TD([[makeQuery(id+"F0.imprint","IMPRINT",EDGE,{"derivedFrom":sQuery(id+"F0.wireOp",EDGE,"E24")}),-1.0]])]});
            var Q6;
            Q6=makeQuery(id+"F0.imprint","IMPRINT",FACE,{"disambiguationData":[TD([[makeQuery(id+"F0.imprint","IMPRINT",EDGE,{"derivedFrom":sQuery(id+"F0.wireOp",EDGE,"E26")}),-1.0]])]});
            var Q7;
            {var subQ0=sQuery(id+"F0.wireOp",EDGE,"E30");Q7=makeQuery(id+"F0.imprint","IMPRINT",FACE,{"disambiguationData":[TD([[makeQuery(id+"F0.imprint","IMPRINT",EDGE,{"derivedFrom":subQ0}),-1.0]])]});}
            var Q8;
            Q8=makeQuery(id+"F0.imprint","IMPRINT",FACE,{"disambiguationData":[TD([[makeQuery(id+"F0.imprint","IMPRINT",EDGE,{"derivedFrom":sQuery(id+"F0.wireOp",EDGE,"E636")}),-1.0]])]});
            var Q9;
            {var subQ4=sQuery(id+"F0.wireOp",EDGE,"E8");Q9=makeQuery(id+"F0.imprint","IMPRINT",FACE,{"disambiguationData":[TD([[makeQuery(id+"F0.imprint","IMPRINT",EDGE,{"derivedFrom":subQ4}),-1.0]])]});}
            var Q10;
            {var subQ0=sQuery(id+"F0.wireOp",EDGE,"E6");Q10=makeQuery(id+"F0.imprint","IMPRINT",FACE,{"disambiguationData":[TD([[makeQuery(id+"F0.imprint","IMPRINT",EDGE,{"derivedFrom":subQ0}),-1.0]])]});}
            var Q11;
            Q11=makeQuery(id+"F0.imprint","IMPRINT",FACE,{"disambiguationData":[TD([[makeQuery(id+"F0.imprint","IMPRINT",EDGE,{"derivedFrom":sQuery(id+"F0.wireOp",EDGE,"E416")}),-1.0]])]});
            var Q12;
            Q12=makeQuery(id+"F0.imprint","IMPRINT",FACE,{"disambiguationData":[TD([[makeQuery(id+"F0.imprint","IMPRINT",EDGE,{"derivedFrom":sQuery(id+"F0.wireOp",EDGE,"E18")}),-1.0]])]});
            extrude(context, id + "F2", {"entities" : qUnion([Q0, Q1, Q2, Q3, Q4, Q5, Q6, Q7, Q8, Q9, Q10, Q11, Q12]), "depth" : 0.4 * mm, "offsetDistance" : 25 * mm});
        }
        {
            var Q0;
            Q0=makeQuery(id+"F0.imprint","IMPRINT",FACE,{"disambiguationData":[TD([[makeQuery(id+"F0.imprint","IMPRINT",EDGE,{"derivedFrom":sQuery(id+"F0.wireOp",EDGE,"c28d15f5-adc6-4a30-85c7-adcf952aa804")}),-1.0]])]});
            var Q1;
            Q1=makeQuery(id+"F0.imprint","IMPRINT",FACE,{"disambiguationData":[TD([[makeQuery(id+"F0.imprint","IMPRINT",EDGE,{"derivedFrom":sQuery(id+"F0.wireOp",EDGE,"E203")}),1.0]])]});
            var Q2;
            {var subQ4=sQuery(id+"F0.wireOp",EDGE,"E8");Q2=makeQuery(id+"F0.imprint","IMPRINT",FACE,{"disambiguationData":[TD([[makeQuery(id+"F0.imprint","IMPRINT",EDGE,{"derivedFrom":subQ4}),-1.0]])]});}
            var Q3;
            {var subQ4=sQuery(id+"F0.wireOp",EDGE,"E6");Q3=makeQuery(id+"F0.imprint","IMPRINT",FACE,{"disambiguationData":[TD([[makeQuery(id+"F0.imprint","IMPRINT",EDGE,{"derivedFrom":subQ4}),1.0]])]});}
            var Q4;
            Q4=makeQuery(id+"F0.imprint","IMPRINT",FACE,{"disambiguationData":[TD([[makeQuery(id+"F0.imprint","IMPRINT",EDGE,{"derivedFrom":sQuery(id+"F0.wireOp",EDGE,"0ef0ce9e-b47a-494d-94a9-4c5436bde830")}),-1.0]])]});
            var Q5;
            Q5=makeQuery(id+"F0.imprint","IMPRINT",FACE,{"disambiguationData":[TD([[makeQuery(id+"F0.imprint","IMPRINT",EDGE,{"derivedFrom":sQuery(id+"F0.wireOp",EDGE,"E390")}),1.0]])]});
            var Q6;
            Q6=makeQuery(id+"F0.imprint","IMPRINT",FACE,{"disambiguationData":[TD([[makeQuery(id+"F0.imprint","IMPRINT",EDGE,{"derivedFrom":sQuery(id+"F0.wireOp",EDGE,"E18")}),-1.0]])]});
            var Q7;
            Q7=makeQuery(id+"F0.imprint","IMPRINT",FACE,{"disambiguationData":[TD([[makeQuery(id+"F0.imprint","IMPRINT",EDGE,{"derivedFrom":sQuery(id+"F0.wireOp",EDGE,"9ac49af5-3e52-4d2b-944c-062c281156f2")}),-1.0]])]});
            var Q8;
            Q8=makeQuery(id+"F0.imprint","IMPRINT",FACE,{"disambiguationData":[TD([[makeQuery(id+"F0.imprint","IMPRINT",EDGE,{"derivedFrom":sQuery(id+"F0.wireOp",EDGE,"b3de240c-4638-49c5-a777-e8f02b175610")}),-1.0]])]});
            var Q9;
            Q9=makeQuery(id+"F0.imprint","IMPRINT",FACE,{"disambiguationData":[TD([[makeQuery(id+"F0.imprint","IMPRINT",EDGE,{"derivedFrom":sQuery(id+"F0.wireOp",EDGE,"E510")}),1.0]])]});
            var Q10;
            Q10=makeQuery(id+"F0.imprint","IMPRINT",FACE,{"disambiguationData":[TD([[makeQuery(id+"F0.imprint","IMPRINT",EDGE,{"derivedFrom":sQuery(id+"F0.wireOp",EDGE,"E992")}),1.0]])]});
            var Q11;
            Q11=makeQuery(id+"F0.imprint","IMPRINT",FACE,{"disambiguationData":[TD([[makeQuery(id+"F0.imprint","IMPRINT",EDGE,{"derivedFrom":sQuery(id+"F0.wireOp",EDGE,"13747a7e-a431-4110-8f3b-2dcf47320d50")}),-1.0]])]});
            var Q12;
            Q12=makeQuery(id+"F0.imprint","IMPRINT",FACE,{"disambiguationData":[TD([[makeQuery(id+"F0.imprint","IMPRINT",EDGE,{"derivedFrom":sQuery(id+"F0.wireOp",EDGE,"E621")}),1.0]])]});
            var Q13;
            Q13=makeQuery(id+"F0.imprint","IMPRINT",FACE,{"disambiguationData":[TD([[makeQuery(id+"F0.imprint","IMPRINT",EDGE,{"derivedFrom":sQuery(id+"F0.wireOp",EDGE,"E809")}),1.0]])]});
            var Q14;
            Q14=makeQuery(id+"F0.imprint","IMPRINT",FACE,{"disambiguationData":[TD([[makeQuery(id+"F0.imprint","IMPRINT",EDGE,{"derivedFrom":sQuery(id+"F0.wireOp",EDGE,"E26")}),1.0]])]});
            var Q15;
            Q15=makeQuery(id+"F0.imprint","IMPRINT",FACE,{"disambiguationData":[TD([[makeQuery(id+"F0.imprint","IMPRINT",EDGE,{"derivedFrom":sQuery(id+"F0.wireOp",EDGE,"E805")}),1.0]])]});
            var Q16;
            {var subQ8=sQuery(id+"F0.wireOp",EDGE,"E35");Q16=makeQuery(id+"F0.imprint","IMPRINT",FACE,{"disambiguationData":[TD([[makeQuery(id+"F0.imprint","IMPRINT",EDGE,{"derivedFrom":subQ8}),1.0]])]});}
            var Q17;
            Q17=makeQuery(id+"F0.imprint","IMPRINT",FACE,{"disambiguationData":[TD([[makeQuery(id+"F0.imprint","IMPRINT",EDGE,{"derivedFrom":sQuery(id+"F0.wireOp",EDGE,"E593")}),1.0]])]});
            var Q18;
            Q18=makeQuery(id+"F0.imprint","IMPRINT",FACE,{"disambiguationData":[TD([[makeQuery(id+"F0.imprint","IMPRINT",EDGE,{"derivedFrom":sQuery(id+"F0.wireOp",EDGE,"E596")}),1.0]])]});
            var Q19;
            Q19=makeQuery(id+"F0.imprint","IMPRINT",FACE,{"disambiguationData":[TD([[makeQuery(id+"F0.imprint","IMPRINT",EDGE,{"derivedFrom":sQuery(id+"F0.wireOp",EDGE,"E542")}),1.0]])]});
            var Q20;
            Q20=makeQuery(id+"F0.imprint","IMPRINT",FACE,{"disambiguationData":[TD([[makeQuery(id+"F0.imprint","IMPRINT",EDGE,{"derivedFrom":sQuery(id+"F0.wireOp",EDGE,"E327")}),1.0]])]});
            var Q21;
            Q21=makeQuery(id+"F0.imprint","IMPRINT",FACE,{"disambiguationData":[TD([[makeQuery(id+"F0.imprint","IMPRINT",EDGE,{"derivedFrom":sQuery(id+"F0.wireOp",EDGE,"E323")}),1.0]])]});
            var Q22;
            {var subQ0=sQuery(id+"F0.wireOp",EDGE,"E6");Q22=makeQuery(id+"F0.imprint","IMPRINT",FACE,{"disambiguationData":[TD([[makeQuery(id+"F0.imprint","IMPRINT",EDGE,{"derivedFrom":subQ0}),-1.0]])]});}
            var Q23;
            {var subQ0=sQuery(id+"F0.wireOp",EDGE,"E8");Q23=makeQuery(id+"F0.imprint","IMPRINT",FACE,{"disambiguationData":[TD([[makeQuery(id+"F0.imprint","IMPRINT",EDGE,{"derivedFrom":subQ0}),1.0]])]});}
            var Q24;
            Q24=makeQuery(id+"F0.imprint","IMPRINT",FACE,{"disambiguationData":[TD([[makeQuery(id+"F0.imprint","IMPRINT",EDGE,{"derivedFrom":sQuery(id+"F0.wireOp",EDGE,"E11")}),1.0]])]});
            var Q25;
            Q25=makeQuery(id+"F0.imprint","IMPRINT",FACE,{"disambiguationData":[TD([[makeQuery(id+"F0.imprint","IMPRINT",EDGE,{"derivedFrom":sQuery(id+"F0.wireOp",EDGE,"E387")}),1.0]])]});
            var Q26;
            Q26=makeQuery(id+"F0.imprint","IMPRINT",FACE,{"disambiguationData":[TD([[makeQuery(id+"F0.imprint","IMPRINT",EDGE,{"derivedFrom":sQuery(id+"F0.wireOp",EDGE,"E599")}),1.0]])]});
            var Q27;
            Q27=makeQuery(id+"F0.imprint","IMPRINT",FACE,{"disambiguationData":[TD([[makeQuery(id+"F0.imprint","IMPRINT",EDGE,{"derivedFrom":sQuery(id+"F0.wireOp",EDGE,"E602")}),1.0]])]});
            var Q28;
            Q28=makeQuery(id+"F0.imprint","IMPRINT",FACE,{"disambiguationData":[TD([[makeQuery(id+"F0.imprint","IMPRINT",EDGE,{"derivedFrom":sQuery(id+"F0.wireOp",EDGE,"5f8c673d-a409-47c4-9682-584896b4f922")}),-1.0]])]});
            var Q29;
            Q29=makeQuery(id+"F0.imprint","IMPRINT",FACE,{"disambiguationData":[TD([[makeQuery(id+"F0.imprint","IMPRINT",EDGE,{"derivedFrom":sQuery(id+"F0.wireOp",EDGE,"E413")}),1.0]])]});
            var Q30;
            Q30=makeQuery(id+"F0.imprint","IMPRINT",FACE,{"disambiguationData":[TD([[makeQuery(id+"F0.imprint","IMPRINT",EDGE,{"derivedFrom":sQuery(id+"F0.wireOp",EDGE,"E14")}),1.0]])]});
            var Q31;
            Q31=makeQuery(id+"F0.imprint","IMPRINT",FACE,{"disambiguationData":[TD([[makeQuery(id+"F0.imprint","IMPRINT",EDGE,{"derivedFrom":sQuery(id+"F0.wireOp",EDGE,"E416")}),-1.0]])]});
            var Q32;
            Q32=makeQuery(id+"F0.imprint","IMPRINT",FACE,{"disambiguationData":[TD([[makeQuery(id+"F0.imprint","IMPRINT",EDGE,{"derivedFrom":sQuery(id+"F0.wireOp",EDGE,"E980")}),1.0]])]});
            var Q33;
            Q33=makeQuery(id+"F0.imprint","IMPRINT",FACE,{"disambiguationData":[TD([[makeQuery(id+"F0.imprint","IMPRINT",EDGE,{"derivedFrom":sQuery(id+"F0.wireOp",EDGE,"E984")}),1.0]])]});
            var Q34;
            Q34=makeQuery(id+"F0.imprint","IMPRINT",FACE,{"disambiguationData":[TD([[makeQuery(id+"F0.imprint","IMPRINT",EDGE,{"derivedFrom":sQuery(id+"F0.wireOp",EDGE,"E1008")}),1.0]])]});
            var Q35;
            Q35=makeQuery(id+"F0.imprint","IMPRINT",FACE,{"disambiguationData":[TD([[makeQuery(id+"F0.imprint","IMPRINT",EDGE,{"derivedFrom":sQuery(id+"F0.wireOp",EDGE,"E1030")}),1.0]])]});
            var Q36;
            Q36=makeQuery(id+"F0.imprint","IMPRINT",FACE,{"disambiguationData":[TD([[makeQuery(id+"F0.imprint","IMPRINT",EDGE,{"derivedFrom":sQuery(id+"F0.wireOp",EDGE,"E507")}),1.0]])]});
            var Q37;
            Q37=makeQuery(id+"F0.imprint","IMPRINT",FACE,{"disambiguationData":[TD([[makeQuery(id+"F0.imprint","IMPRINT",EDGE,{"derivedFrom":sQuery(id+"F0.wireOp",EDGE,"E534")}),1.0]])]});
            var Q38;
            Q38=makeQuery(id+"F0.imprint","IMPRINT",FACE,{"disambiguationData":[TD([[makeQuery(id+"F0.imprint","IMPRINT",EDGE,{"derivedFrom":sQuery(id+"F0.wireOp",EDGE,"E20")}),1.0]])]});
            var Q39;
            Q39=makeQuery(id+"F0.imprint","IMPRINT",FACE,{"disambiguationData":[TD([[makeQuery(id+"F0.imprint","IMPRINT",EDGE,{"derivedFrom":sQuery(id+"F0.wireOp",EDGE,"E18")}),1.0]])]});
            var Q40;
            Q40=makeQuery(id+"F0.imprint","IMPRINT",FACE,{"disambiguationData":[TD([[makeQuery(id+"F0.imprint","IMPRINT",EDGE,{"derivedFrom":sQuery(id+"F0.wireOp",EDGE,"E1033")}),1.0]])]});
            var Q41;
            Q41=makeQuery(id+"F0.imprint","IMPRINT",FACE,{"disambiguationData":[TD([[makeQuery(id+"F0.imprint","IMPRINT",EDGE,{"derivedFrom":sQuery(id+"F0.wireOp",EDGE,"E1037")}),1.0]])]});
            var Q42;
            Q42=makeQuery(id+"F0.imprint","IMPRINT",FACE,{"disambiguationData":[TD([[makeQuery(id+"F0.imprint","IMPRINT",EDGE,{"derivedFrom":sQuery(id+"F0.wireOp",EDGE,"E1043")}),1.0]])]});
            var Q43;
            Q43=makeQuery(id+"F0.imprint","IMPRINT",FACE,{"disambiguationData":[TD([[makeQuery(id+"F0.imprint","IMPRINT",EDGE,{"derivedFrom":sQuery(id+"F0.wireOp",EDGE,"E1046")}),1.0]])]});
            var Q44;
            Q44=makeQuery(id+"F0.imprint","IMPRINT",FACE,{"disambiguationData":[TD([[makeQuery(id+"F0.imprint","IMPRINT",EDGE,{"derivedFrom":sQuery(id+"F0.wireOp",EDGE,"E1051")}),1.0]])]});
            var Q45;
            Q45=makeQuery(id+"F0.imprint","IMPRINT",FACE,{"disambiguationData":[TD([[makeQuery(id+"F0.imprint","IMPRINT",EDGE,{"derivedFrom":sQuery(id+"F0.wireOp",EDGE,"E538")}),1.0]])]});
            var Q46;
            Q46=makeQuery(id+"F0.imprint","IMPRINT",FACE,{"disambiguationData":[TD([[makeQuery(id+"F0.imprint","IMPRINT",EDGE,{"derivedFrom":sQuery(id+"F0.wireOp",EDGE,"E1040")}),1.0]])]});
            var Q47;
            Q47=makeQuery(id+"F0.imprint","IMPRINT",FACE,{"disambiguationData":[TD([[makeQuery(id+"F0.imprint","IMPRINT",EDGE,{"derivedFrom":sQuery(id+"F0.wireOp",EDGE,"E50")}),1.0]])]});
            var Q48;
            Q48=makeQuery(id+"F0.imprint","IMPRINT",FACE,{"disambiguationData":[TD([[makeQuery(id+"F0.imprint","IMPRINT",EDGE,{"derivedFrom":sQuery(id+"F0.wireOp",EDGE,"E1026")}),1.0]])]});
            var Q49;
            Q49=makeQuery(id+"F0.imprint","IMPRINT",FACE,{"disambiguationData":[TD([[makeQuery(id+"F0.imprint","IMPRINT",EDGE,{"derivedFrom":sQuery(id+"F0.wireOp",EDGE,"E1005")}),1.0]])]});
            var Q50;
            Q50=makeQuery(id+"F0.imprint","IMPRINT",FACE,{"disambiguationData":[TD([[makeQuery(id+"F0.imprint","IMPRINT",EDGE,{"derivedFrom":sQuery(id+"F0.wireOp",EDGE,"E48")}),1.0]])]});
            var Q51;
            Q51=makeQuery(id+"F0.imprint","IMPRINT",FACE,{"disambiguationData":[TD([[makeQuery(id+"F0.imprint","IMPRINT",EDGE,{"derivedFrom":sQuery(id+"F0.wireOp",EDGE,"E1014")}),1.0]])]});
            var Q52;
            Q52=makeQuery(id+"F0.imprint","IMPRINT",FACE,{"disambiguationData":[TD([[makeQuery(id+"F0.imprint","IMPRINT",EDGE,{"derivedFrom":sQuery(id+"F0.wireOp",EDGE,"E1019")}),1.0]])]});
            var Q53;
            Q53=makeQuery(id+"F0.imprint","IMPRINT",FACE,{"disambiguationData":[TD([[makeQuery(id+"F0.imprint","IMPRINT",EDGE,{"derivedFrom":sQuery(id+"F0.wireOp",EDGE,"E1011")}),1.0]])]});
            var Q54;
            Q54=makeQuery(id+"F0.imprint","IMPRINT",FACE,{"disambiguationData":[TD([[makeQuery(id+"F0.imprint","IMPRINT",EDGE,{"derivedFrom":sQuery(id+"F0.wireOp",EDGE,"E782")}),1.0]])]});
            var Q55;
            Q55=makeQuery(id+"F0.imprint","IMPRINT",FACE,{"disambiguationData":[TD([[makeQuery(id+"F0.imprint","IMPRINT",EDGE,{"derivedFrom":sQuery(id+"F0.wireOp",EDGE,"E778")}),-1.0]])]});
            var Q56;
            Q56=makeQuery(id+"F0.imprint","IMPRINT",FACE,{"disambiguationData":[TD([[makeQuery(id+"F0.imprint","IMPRINT",EDGE,{"derivedFrom":sQuery(id+"F0.wireOp",EDGE,"E1023")}),1.0]])]});
            var Q57;
            Q57=makeQuery(id+"F0.imprint","IMPRINT",FACE,{"disambiguationData":[TD([[makeQuery(id+"F0.imprint","IMPRINT",EDGE,{"derivedFrom":sQuery(id+"F0.wireOp",EDGE,"E988")}),1.0]])]});
            var Q58;
            Q58=makeQuery(id+"F0.imprint","IMPRINT",FACE,{"disambiguationData":[TD([[makeQuery(id+"F0.imprint","IMPRINT",EDGE,{"derivedFrom":sQuery(id+"F0.wireOp",EDGE,"E55")}),1.0]])]});
            var Q59;
            Q59=makeQuery(id+"F0.imprint","IMPRINT",FACE,{"disambiguationData":[TD([[makeQuery(id+"F0.imprint","IMPRINT",EDGE,{"derivedFrom":sQuery(id+"F0.wireOp",EDGE,"E57")}),-1.0]])]});
            var Q60;
            Q60=makeQuery(id+"F0.imprint","IMPRINT",FACE,{"disambiguationData":[TD([[makeQuery(id+"F0.imprint","IMPRINT",EDGE,{"derivedFrom":sQuery(id+"F0.wireOp",EDGE,"E999")}),1.0]])]});
            var Q61;
            Q61=makeQuery(id+"F0.imprint","IMPRINT",FACE,{"disambiguationData":[TD([[makeQuery(id+"F0.imprint","IMPRINT",EDGE,{"derivedFrom":sQuery(id+"F0.wireOp",EDGE,"E1002")}),1.0]])]});
            var Q62;
            Q62=makeQuery(id+"F0.imprint","IMPRINT",FACE,{"disambiguationData":[TD([[makeQuery(id+"F0.imprint","IMPRINT",EDGE,{"derivedFrom":sQuery(id+"F0.wireOp",EDGE,"E821")}),1.0]])]});
            var Q63;
            Q63=makeQuery(id+"F0.imprint","IMPRINT",FACE,{"disambiguationData":[TD([[makeQuery(id+"F0.imprint","IMPRINT",EDGE,{"derivedFrom":sQuery(id+"F0.wireOp",EDGE,"E44")}),1.0]])]});
            var Q64;
            Q64=makeQuery(id+"F0.imprint","IMPRINT",FACE,{"disambiguationData":[TD([[makeQuery(id+"F0.imprint","IMPRINT",EDGE,{"derivedFrom":sQuery(id+"F0.wireOp",EDGE,"E802")}),1.0]])]});
            var Q65;
            Q65=makeQuery(id+"F0.imprint","IMPRINT",FACE,{"disambiguationData":[TD([[makeQuery(id+"F0.imprint","IMPRINT",EDGE,{"derivedFrom":sQuery(id+"F0.wireOp",EDGE,"E28")}),1.0]])]});
            var Q66;
            Q66=makeQuery(id+"F0.imprint","IMPRINT",FACE,{"disambiguationData":[TD([[makeQuery(id+"F0.imprint","IMPRINT",EDGE,{"derivedFrom":sQuery(id+"F0.wireOp",EDGE,"E39")}),1.0]])]});
            var Q67;
            {var subQ0=sQuery(id+"F0.wireOp",EDGE,"E33");Q67=makeQuery(id+"F0.imprint","IMPRINT",FACE,{"disambiguationData":[TD([[makeQuery(id+"F0.imprint","IMPRINT",EDGE,{"derivedFrom":subQ0}),1.0]])]});}
            var Q68;
            {var subQ0=sQuery(id+"F0.wireOp",EDGE,"E30");Q68=makeQuery(id+"F0.imprint","IMPRINT",FACE,{"disambiguationData":[TD([[makeQuery(id+"F0.imprint","IMPRINT",EDGE,{"derivedFrom":subQ0}),-1.0]])]});}
            var Q69;
            Q69=makeQuery(id+"F0.imprint","IMPRINT",FACE,{"disambiguationData":[TD([[makeQuery(id+"F0.imprint","IMPRINT",EDGE,{"derivedFrom":sQuery(id+"F0.wireOp",EDGE,"E645")}),1.0]])]});
            var Q70;
            {var subQ5=sQuery(id+"F0.wireOp",EDGE,"E37");var subQ6=sQuery(id+"F0.wireOp",EDGE,"E36");var subQ7=makeQuery(id+"F0.imprint","INTERSECT",VERTEX,{"derivedFrom":[subQ6,subQ5]});Q70=makeQuery(id+"F0.imprint","IMPRINT",FACE,{"disambiguationData":[TD([[makeQuery(id+"F0.imprint","IMPRINT",EDGE,{"disambiguationData":[TD([[subQ7,1.0]])],"derivedFrom":subQ6}),1.0]])]});}
            var Q71;
            {var subQ0=sQuery(id+"F0.wireOp",EDGE,"E735");Q71=makeQuery(id+"F0.imprint","IMPRINT",FACE,{"disambiguationData":[TD([[makeQuery(id+"F0.imprint","IMPRINT",EDGE,{"derivedFrom":subQ0}),-1.0]])]});}
            var Q72;
            {var subQ0=sQuery(id+"F0.wireOp",EDGE,"E35");Q72=makeQuery(id+"F0.imprint","IMPRINT",FACE,{"disambiguationData":[TD([[makeQuery(id+"F0.imprint","IMPRINT",EDGE,{"derivedFrom":subQ0}),-1.0]])]});}
            var Q73;
            Q73=makeQuery(id+"F0.imprint","IMPRINT",FACE,{"disambiguationData":[TD([[makeQuery(id+"F0.imprint","IMPRINT",EDGE,{"derivedFrom":sQuery(id+"F0.wireOp",EDGE,"E771")}),-1.0]])]});
            var Q74;
            Q74=makeQuery(id+"F0.imprint","IMPRINT",FACE,{"disambiguationData":[TD([[makeQuery(id+"F0.imprint","IMPRINT",EDGE,{"derivedFrom":sQuery(id+"F0.wireOp",EDGE,"E785")}),1.0]])]});
            var Q75;
            Q75=makeQuery(id+"F0.imprint","IMPRINT",FACE,{"disambiguationData":[TD([[makeQuery(id+"F0.imprint","IMPRINT",EDGE,{"derivedFrom":sQuery(id+"F0.wireOp",EDGE,"E24")}),-1.0]])]});
            var Q76;
            Q76=makeQuery(id+"F0.imprint","IMPRINT",FACE,{"disambiguationData":[TD([[makeQuery(id+"F0.imprint","IMPRINT",EDGE,{"derivedFrom":sQuery(id+"F0.wireOp",EDGE,"E636")}),-1.0]])]});
            var Q77;
            Q77=makeQuery(id+"F0.imprint","IMPRINT",FACE,{"disambiguationData":[TD([[makeQuery(id+"F0.imprint","IMPRINT",EDGE,{"derivedFrom":sQuery(id+"F0.wireOp",EDGE,"E0")}),-1.0]])]});
            var Q78;
            Q78=makeQuery(id+"F0.imprint","IMPRINT",FACE,{"disambiguationData":[TD([[makeQuery(id+"F0.imprint","IMPRINT",EDGE,{"derivedFrom":sQuery(id+"F0.wireOp",EDGE,"E641")}),1.0]])]});
            var Q79;
            Q79=makeQuery(id+"F0.imprint","IMPRINT",FACE,{"disambiguationData":[TD([[makeQuery(id+"F0.imprint","IMPRINT",EDGE,{"derivedFrom":sQuery(id+"F0.wireOp",EDGE,"E26")}),-1.0]])]});
            var Q80;
            Q80=makeQuery(id+"F0.imprint","IMPRINT",FACE,{"disambiguationData":[TD([[makeQuery(id+"F0.imprint","IMPRINT",EDGE,{"derivedFrom":sQuery(id+"F0.wireOp",EDGE,"E41")}),1.0]])]});
            var Q81;
            Q81=makeQuery(id+"F1.imprint","IMPRINT",FACE,{"disambiguationData":[TD([[makeQuery(id+"F1.imprint","IMPRINT",EDGE,{"derivedFrom":sQuery(id+"F1.wireOp",EDGE,"E1055")}),-1.0]])]});
            var Q82;
            Q82=makeQuery(id+"F1.imprint","IMPRINT",FACE,{"disambiguationData":[TD([[makeQuery(id+"F1.imprint","IMPRINT",EDGE,{"derivedFrom":sQuery(id+"F1.wireOp",EDGE,"E1090")}),-1.0]])]});
            var Q83;
            Q83=makeQuery(id+"F1.imprint","IMPRINT",FACE,{"disambiguationData":[TD([[makeQuery(id+"F1.imprint","IMPRINT",EDGE,{"derivedFrom":sQuery(id+"F1.wireOp",EDGE,"E1057")}),-1.0]])]});
            var Q84;
            {var subQ0=sQuery(id+"F1.wireOp",EDGE,"E1059");Q84=makeQuery(id+"F1.imprint","IMPRINT",FACE,{"disambiguationData":[TD([[makeQuery(id+"F1.imprint","IMPRINT",EDGE,{"derivedFrom":subQ0}),-1.0]])]});}
            var Q85;
            Q85=makeQuery(id+"F1.imprint","IMPRINT",FACE,{"disambiguationData":[TD([[makeQuery(id+"F1.imprint","IMPRINT",EDGE,{"derivedFrom":sQuery(id+"F1.wireOp",EDGE,"E1065")}),-1.0]])]});
            var Q86;
            Q86=makeQuery(id+"F1.imprint","IMPRINT",FACE,{"disambiguationData":[TD([[makeQuery(id+"F1.imprint","IMPRINT",EDGE,{"derivedFrom":sQuery(id+"F1.wireOp",EDGE,"E1075")}),-1.0]])]});
            var Q87;
            Q87=makeQuery(id+"F1.imprint","IMPRINT",FACE,{"disambiguationData":[TD([[makeQuery(id+"F1.imprint","IMPRINT",EDGE,{"derivedFrom":sQuery(id+"F1.wireOp",EDGE,"E1080")}),1.0]])]});
            var Q88;
            Q88=makeQuery(id+"F1.imprint","IMPRINT",FACE,{"disambiguationData":[TD([[makeQuery(id+"F1.imprint","IMPRINT",EDGE,{"derivedFrom":sQuery(id+"F1.wireOp",EDGE,"E1084")}),1.0]])]});
            extrude(context, id + "F3", {"entities" : qUnion([Q0, Q1, Q2, Q3, Q4, Q5, Q6, Q7, Q8, Q9, Q10, Q11, Q12, Q13, Q14, Q15, Q16, Q17, Q18, Q19, Q20, Q21, Q22, Q23, Q24, Q25, Q26, Q27, Q28, Q29, Q30, Q31, Q32, Q33, Q34, Q35, Q36, Q37, Q38, Q39, Q40, Q41, Q42, Q43, Q44, Q45, Q46, Q47, Q48, Q49, Q50, Q51, Q52, Q53, Q54, Q55, Q56, Q57, Q58, Q59, Q60, Q61, Q62, Q63, Q64, Q65, Q66, Q67, Q68, Q69, Q70, Q71, Q72, Q73, Q74, Q75, Q76, Q77, Q78, Q79, Q80, Q81, Q82, Q83, Q84, Q85, Q86, Q87, Q88]), "oppositeDirection" : true, "depth" : 2 * mm, "offsetDistance" : 25 * mm});
        }
    });
